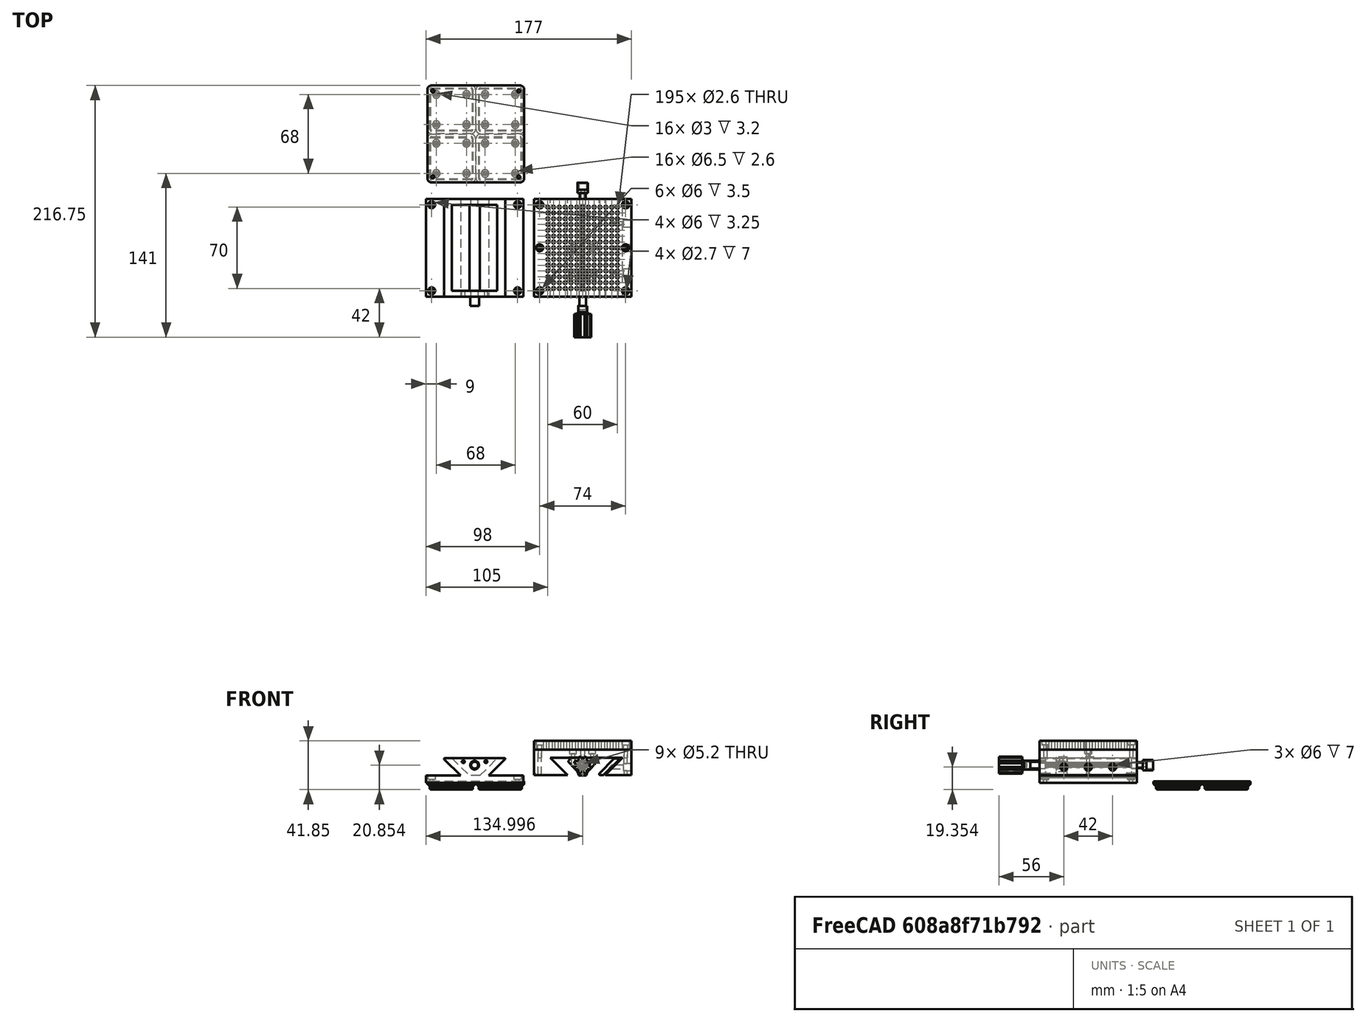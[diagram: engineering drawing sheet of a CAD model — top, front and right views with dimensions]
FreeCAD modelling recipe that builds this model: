
FCSTD DOCUMENT  (FreeCAD 1.0R39109 (Git))
Label: Linear Stage  v5
License: All rights reserved
LicenseURL: https://en.wikipedia.org/wiki/All_rights_reserved
objects: Sketcher::SketchObject×59, PartDesign::Pocket×30, PartDesign::Pad×26, PartDesign::Chamfer×17, PartDesign::Plane×11, PartDesign::ShapeBinder×10, PartDesign::Body×10, PartDesign::Fillet×6, PartDesign::Hole×3, PartDesign::FeatureBase×2, PartDesign::Point×1, Part::Part2DObjectPython×1, Part::Helix×1, PartDesign::AdditivePipe×1, PartDesign::FeaturePython×1, App::VarSet×1
note: 407 computed .brp shape members not serialized (recipe doc carries the construction recipe); baked Part::Feature solids carry a one-line shape summary decoded from their .brp

FEATURE [Sketcher::SketchObject] Sketch
  ArcFitTolerance = 1e-06
  AttachmentSupport = -> [XZ_Plane]
  FullyConstrained = true
  MakeInternals = false
  MapMode = 5
  Placement = pos=(0,0,0) rot=(1,0,0;1.5708rad)
  sketch-geometry (8):
    g0: LineSegment StartX=0 StartY=0 StartZ=0 EndX=84 EndY=0 EndZ=0
    g1: LineSegment StartX=0 StartY=0 StartZ=0 EndX=0 EndY=5 EndZ=0
    g2: LineSegment StartX=84 StartY=0 StartZ=0 EndX=84 EndY=5 EndZ=0
    g3: LineSegment StartX=0 StartY=5 StartZ=0 EndX=30 EndY=5 EndZ=0
    g4: LineSegment StartX=84 StartY=5 StartZ=0 EndX=54 EndY=5 EndZ=0
    g5: LineSegment StartX=30 StartY=5 StartZ=0 EndX=15 EndY=20 EndZ=0
    g6: LineSegment StartX=54 StartY=5 StartZ=0 EndX=69 EndY=20 EndZ=0
    g7: LineSegment StartX=15 StartY=20 StartZ=0 EndX=69 EndY=20 EndZ=0
  constraints (24):
    c: Distance(g0) = 84
    c: Distance(g1) = 5
    c: Coincident(g1,g0)
    c: PointOnObject(g1,g-2)
    c: Vertical(g1)
    c: Distance(g2) = 5
    c: Vertical(g2)
    c: Tangent(g0,g-1)
    c: PointOnObject(g2,g0)
    c: PointOnObject(g0,g2)
    c: Coincident(g3,g1)
    c: Horizontal(g3)
    c: Coincident(g4,g2)
    c: Horizontal(g4)
    c: DistanceX(g3,g3) = 30
    c: DistanceX(g4,g4) = 30
    c: Angle(g-1,g5) = 2.35619
    c: Coincident(g5,g3)
    c: Angle(g-1,g6) = 0.785398
    c: Coincident(g6,g4)
    c: DistanceY(g-1,g5) = 20
    c: DistanceY(g-1,g6) = 20
    c: Coincident(g7,g5)
    c: Coincident(g7,g6)
FEATURE [PartDesign::Pad] Pad
  Direction = (0,-1,2e-16)
  Length = 5
  Length2 = 10
  Placement = pos=(0,0,0) rot=(1,0,0;1.5708rad)
  Profile = -> Sketch
  ReferenceAxis = -> Sketch [N_Axis]
  Refine = true
  Suppressed = false
  Type = 0
FEATURE [Sketcher::SketchObject] Sketch001
  ArcFitTolerance = 1e-06
  AttachmentSupport = -> [Pad]
  ExternalGeometry = -> [Pad]
  FullyConstrained = true
  MakeInternals = false
  MapMode = 5
  Placement = pos=(0,-5,0) rot=(1,0,0;1.5708rad)
  sketch-geometry (14):
    g0: LineSegment StartX=15 StartY=20 StartZ=0 EndX=22.5 EndY=20 EndZ=0
    g1: LineSegment [constr] StartX=30 StartY=5 StartZ=0 EndX=37.5 EndY=5 EndZ=0
    g2: LineSegment StartX=22.5 StartY=20 StartZ=0 EndX=37.5 EndY=5 EndZ=0
    g3: LineSegment StartX=69 StartY=20 StartZ=0 EndX=61.5 EndY=20 EndZ=0
    g4: LineSegment [constr] StartX=54 StartY=5 StartZ=0 EndX=46.5 EndY=5 EndZ=0
    g5: LineSegment StartX=46.5 StartY=5 StartZ=0 EndX=61.5 EndY=20 EndZ=0
    g6: LineSegment StartX=46.5 StartY=5 StartZ=0 EndX=37.5 EndY=5 EndZ=0
    g7: LineSegment StartX=15 StartY=20 StartZ=0 EndX=30 EndY=5 EndZ=0
    g8: LineSegment StartX=30 StartY=5 StartZ=0 EndX=0 EndY=5 EndZ=0
    g9: LineSegment StartX=0 StartY=5 StartZ=0 EndX=0 EndY=0 EndZ=0
    g10: LineSegment StartX=0 StartY=0 StartZ=0 EndX=84 EndY=0 EndZ=0
    g11: LineSegment StartX=84 StartY=0 StartZ=0 EndX=84 EndY=5 EndZ=0
    g12: LineSegment StartX=84 StartY=5 StartZ=0 EndX=54 EndY=5 EndZ=0
    g13: LineSegment StartX=54 StartY=5 StartZ=0 EndX=69 EndY=20 EndZ=0
  constraints (32):
    c: Distance(g0) = 7.5
    c: Coincident(g0,g-4)
    c: PointOnObject(g0,g-3)
    c: Distance(g1) = 7.5
    c: Coincident(g1,g-5)
    c: Horizontal(g1)
    c: Coincident(g2,g0)
    c: Coincident(g2,g1)
    c: Distance(g3) = 7.5
    c: Coincident(g3,g-3)
    c: PointOnObject(g3,g-3)
    c: Distance(g4) = 7.5
    c: Coincident(g4,g-6)
    c: Horizontal(g4)
    c: Coincident(g5,g4)
    c: Coincident(g5,g3)
    c: Coincident(g6,g4)
    c: Coincident(g6,g1)
    c: Coincident(g7,g0)
    c: Coincident(g7,g1)
    c: Coincident(g8,g1)
    c: Coincident(g8,g-8)
    c: Coincident(g9,g8)
    c: Coincident(g9,g-1)
    c: Coincident(g10,g9)
    c: Coincident(g10,g-9)
    c: Coincident(g11,g10)
    c: Coincident(g11,g-7)
    c: Coincident(g12,g11)
    c: Coincident(g12,g4)
    c: Coincident(g13,g4)
    c: Coincident(g13,g3)
FEATURE [PartDesign::Pad] Pad001
  BaseFeature = -> Pad
  Direction = (0,-1,2e-16)
  Length = 74
  Length2 = 10
  Placement = pos=(0,0,0) rot=(1,0,0;1.5708rad)
  Profile = -> Sketch001
  ReferenceAxis = -> Sketch001 [N_Axis]
  Refine = true
  Suppressed = false
  Type = 0
FEATURE [Sketcher::SketchObject] Sketch002
  ArcFitTolerance = 1e-06
  AttachmentSupport = -> [Pad001]
  ExternalGeometry = -> [Pad001]
  FullyConstrained = true
  MakeInternals = false
  MapMode = 5
  Placement = pos=(0,-5,0) rot=(1,0,0;1.5708rad)
  sketch-geometry (2):
    g0: LineSegment [constr] StartX=42 StartY=20 StartZ=0 EndX=42 EndY=14 EndZ=0
    g1: Circle CenterX=42 CenterY=14 CenterZ=0 NormalX=0 NormalY=0 NormalZ=1 AngleXU=0 Radius=3
  constraints (5):
    c: Distance(g0) = 6
    c: Symmetric(g-3,g-3,g0)
    c: Vertical(g0)
    c: Diameter(g1) = 6
    c: Coincident(g1,g0)
FEATURE [PartDesign::Hole] Hole
  BaseFeature = -> Pad001
  CustomThreadClearance = 0
  Depth = 25
  DepthType = 0
  Diameter = 6
  DrillForDepth = false
  DrillPoint = 1
  DrillPointAngle = 118
  HoleCutCountersinkAngle = 90
  HoleCutCustomValues = false
  HoleCutDepth = 0
  HoleCutDiameter = 6.1
  HoleCutType = 0
  ModelThread = false
  Placement = pos=(0,0,0) rot=(1,0,0;1.5708rad)
  Profile = -> Sketch002
  Refine = true
  Suppressed = false
  Tapered = false
  TaperedAngle = 90
  ThreadClass = 0
  ThreadDepth = 25
  ThreadDepthType = 0
  ThreadDirection = 0
  ThreadFit = 0
  ThreadSize = 0
  ThreadType = 0
  Threaded = false
  UseCustomThreadClearance = false
FEATURE [Sketcher::SketchObject] Sketch003
  ArcFitTolerance = 1e-06
  AttachmentSupport = -> [Hole]
  ExternalGeometry = -> [Hole]
  FullyConstrained = true
  MakeInternals = false
  MapMode = 5
  Placement = pos=(0,-79,1.74e-14) rot=(1,0,0;1.5708rad)
  sketch-geometry (16):
    g0: LineSegment StartX=15 StartY=20 StartZ=0 EndX=69 EndY=20 EndZ=0
    g1: LineSegment StartX=15 StartY=20 StartZ=0 EndX=30 EndY=5 EndZ=0
    g2: LineSegment StartX=30 StartY=5 StartZ=0 EndX=0 EndY=5 EndZ=0
    g3: LineSegment StartX=0 StartY=5 StartZ=0 EndX=0 EndY=0 EndZ=0
    g4: LineSegment StartX=0 StartY=0 StartZ=0 EndX=84 EndY=0 EndZ=0
    g5: LineSegment StartX=84 StartY=0 StartZ=0 EndX=84 EndY=5 EndZ=0
    g6: LineSegment StartX=84 StartY=5 StartZ=0 EndX=54 EndY=5 EndZ=0
    g7: LineSegment StartX=54 StartY=5 StartZ=0 EndX=69 EndY=20 EndZ=0
    g8: LineSegment [constr] StartX=42 StartY=20 StartZ=0 EndX=42 EndY=14 EndZ=0
    g9: Circle CenterX=42 CenterY=14 CenterZ=0 NormalX=0 NormalY=0 NormalZ=1 AngleXU=0 Radius=3
    g10: LineSegment [constr] StartX=42 StartY=14 StartZ=0 EndX=22.5 EndY=20 EndZ=0
    g11: LineSegment [constr] StartX=42 StartY=14 StartZ=0 EndX=61.5 EndY=20 EndZ=0
    g12: GeomPoint [constr] X=32.25 Y=17 Z=0
    g13: GeomPoint [constr] X=51.75 Y=17 Z=0
    g14: Circle CenterX=32.25 CenterY=17 CenterZ=0 NormalX=0 NormalY=0 NormalZ=1 AngleXU=0 Radius=1.25
    g15: Circle CenterX=51.75 CenterY=17 CenterZ=0 NormalX=0 NormalY=0 NormalZ=1 AngleXU=0 Radius=1.25
  constraints (31):
    c: Coincident(g0,g-4)
    c: Coincident(g0,g-11)
    c: Coincident(g1,g0)
    c: Coincident(g1,g-5)
    c: Coincident(g2,g1)
    c: Coincident(g2,g-6)
    c: Coincident(g3,g2)
    c: Coincident(g3,g-1)
    c: Coincident(g4,g3)
    c: Coincident(g4,g-8)
    c: Coincident(g5,g4)
    c: Coincident(g5,g-9)
    c: Coincident(g6,g5)
    c: Coincident(g6,g-10)
    c: Coincident(g7,g6)
    c: Coincident(g7,g0)
    c: Distance(g8) = 6
    c: Symmetric(g0,g0,g8)
    c: Vertical(g8)
    c: Diameter(g9) = 6
    c: Coincident(g9,g8)
    c: Coincident(g10,g8)
    c: Coincident(g10,g-14)
    c: Coincident(g11,g8)
    c: Coincident(g11,g-12)
    c: Symmetric(g10,g10,g12)
    c: Symmetric(g11,g11,g13)
    c: Diameter(g14) = 2.5
    c: Coincident(g14,g12)
    c: Diameter(g15) = 2.5
    c: Coincident(g15,g13)
FEATURE [PartDesign::Pad] Pad002
  BaseFeature = -> Hole
  Direction = (0,-1,2e-16)
  Length = 5
  Length2 = 10
  Placement = pos=(0,0,0) rot=(1,0,0;1.5708rad)
  Profile = -> Sketch003
  ReferenceAxis = -> Sketch003 [N_Axis]
  Refine = true
  Suppressed = false
  Type = 0
FEATURE [PartDesign::Plane] DatumPlane
  AttachmentSupport = -> [Pad002]
  Length = 131.586
  MapMode = 5
  Placement = pos=(0,0,-5e-16) rot=(1,0,0;3.14159rad)
  ResizeMode = 0
  Width = 139.586
FEATURE [Sketcher::SketchObject] Sketch004
  ArcFitTolerance = 1e-06
  AttachmentSupport = -> [Pad002]
  ExternalGeometry = -> [Pad002]
  FullyConstrained = true
  MakeInternals = false
  MapMode = 5
  Placement = pos=(0,0,-5e-16) rot=(1,0,0;3.14159rad)
  sketch-geometry (23):
    g0: LineSegment [constr] StartX=0 StartY=84 StartZ=0 EndX=84 EndY=0 EndZ=0
    g1: LineSegment [constr] StartX=41.75 StartY=41.75 StartZ=0 EndX=42.25 EndY=41.75 EndZ=0
    g2: LineSegment [constr] StartX=42.25 StartY=41.75 StartZ=0 EndX=42.25 EndY=42.25 EndZ=0
    g3: LineSegment [constr] StartX=42.25 StartY=42.25 StartZ=0 EndX=41.75 EndY=42.25 EndZ=0
    g4: LineSegment [constr] StartX=41.75 StartY=42.25 StartZ=0 EndX=41.75 EndY=41.75 EndZ=0
    g5: GeomPoint [constr] X=42 Y=42 Z=0
    g6: LineSegment [constr] StartX=0 StartY=0 StartZ=0 EndX=84 EndY=84 EndZ=0
    g7: LineSegment StartX=42.25 StartY=42.25 StartZ=0 EndX=83.75 EndY=42.25 EndZ=0
    g8: LineSegment StartX=83.75 StartY=42.25 StartZ=0 EndX=83.75 EndY=83.75 EndZ=0
    g9: LineSegment StartX=83.75 StartY=83.75 StartZ=0 EndX=42.25 EndY=83.75 EndZ=0
    g10: LineSegment StartX=42.25 StartY=83.75 StartZ=0 EndX=42.25 EndY=42.25 EndZ=0
    g11: LineSegment StartX=41.75 StartY=42.25 StartZ=0 EndX=41.75 EndY=83.75 EndZ=0
    g12: LineSegment StartX=41.75 StartY=83.75 StartZ=0 EndX=0.25 EndY=83.75 EndZ=0
    g13: LineSegment StartX=0.25 StartY=83.75 StartZ=0 EndX=0.25 EndY=42.25 EndZ=0
    g14: LineSegment StartX=0.25 StartY=42.25 StartZ=0 EndX=41.75 EndY=42.25 EndZ=0
    g15: LineSegment StartX=42.25 StartY=41.75 StartZ=0 EndX=42.25 EndY=0.25 EndZ=0
    g16: LineSegment StartX=42.25 StartY=0.25 StartZ=0 EndX=83.75 EndY=0.25 EndZ=0
    g17: LineSegment StartX=83.75 StartY=0.25 StartZ=0 EndX=83.75 EndY=41.75 EndZ=0
    g18: LineSegment StartX=83.75 StartY=41.75 StartZ=0 EndX=42.25 EndY=41.75 EndZ=0
    g19: LineSegment StartX=41.75 StartY=41.75 StartZ=0 EndX=0.25 EndY=41.75 EndZ=0
    g20: LineSegment StartX=0.25 StartY=41.75 StartZ=0 EndX=0.25 EndY=0.25 EndZ=0
    g21: LineSegment StartX=0.25 StartY=0.25 StartZ=0 EndX=41.75 EndY=0.25 EndZ=0
    g22: LineSegment StartX=41.75 StartY=0.25 StartZ=0 EndX=41.75 EndY=41.75 EndZ=0
  constraints (61):
    c: Coincident(g0,g-6)
    c: Coincident(g0,g-5)
    c: Coincident(g1,g2)
    c: Coincident(g2,g3)
    c: Coincident(g3,g4)
    c: Coincident(g4,g1)
    c: Horizontal(g1)
    c: Horizontal(g3)
    c: Vertical(g2)
    c: Vertical(g4)
    c: Symmetric(g3,g1,g5)
    c: Distance(g2,g4) = 0.5
    c: Distance(g1,g3) = 0.5
    c: PointOnObject(g5,g0)
    c: Coincident(g6,g-1)
    c: Coincident(g6,g-4)
    c: PointOnObject(g5,g6)
    c: Coincident(g7,g8)
    c: Coincident(g8,g9)
    c: Coincident(g9,g10)
    c: Coincident(g10,g7)
    c: Horizontal(g7)
    c: Horizontal(g9)
    c: Vertical(g8)
    c: Vertical(g10)
    c: Distance(g8,g10) = 41.5
    c: Coincident(g7,g2)
    c: PointOnObject(g8,g6)
    c: Coincident(g11,g12)
    c: Coincident(g12,g13)
    c: Coincident(g13,g14)
    c: Coincident(g14,g11)
    c: Vertical(g11)
    c: Vertical(g13)
    c: Horizontal(g12)
    c: Horizontal(g14)
    c: Distance(g11,g13) = 41.5
    c: Coincident(g11,g3)
    c: PointOnObject(g12,g0)
    c: Coincident(g15,g16)
    c: Coincident(g16,g17)
    c: Coincident(g17,g18)
    c: Coincident(g18,g15)
    c: Vertical(g15)
    c: Vertical(g17)
    c: Horizontal(g16)
    c: Horizontal(g18)
    c: Distance(g15,g17) = 41.5
    c: Coincident(g15,g1)
    c: PointOnObject(g16,g0)
    c: Coincident(g19,g20)
    c: Coincident(g20,g21)
    c: Coincident(g21,g22)
    c: Coincident(g22,g19)
    c: Horizontal(g19)
    c: Horizontal(g21)
    c: Vertical(g20)
    c: Vertical(g22)
    c: Distance(g20,g22) = 41.5
    c: Coincident(g19,g1)
    c: PointOnObject(g20,g6)
FEATURE [PartDesign::Pad] Pad003
  BaseFeature = -> Pad002
  Direction = (0,0,-1)
  Length = 1
  Length2 = 10
  Placement = pos=(0,0,0) rot=(1,0,0;1.5708rad)
  Profile = -> Sketch004
  ReferenceAxis = -> Sketch004 [N_Axis]
  Refine = true
  Suppressed = false
  Type = 0
FEATURE [PartDesign::Plane] DatumPlane001
  AttachmentSupport = -> [Pad003]
  Length = 131.586
  MapMode = 5
  Placement = pos=(0,0,-1) rot=(1,0,0;3.14159rad)
  ResizeMode = 0
  Width = 139.586
FEATURE [Sketcher::SketchObject] Sketch005
  ArcFitTolerance = 1e-06
  AttachmentSupport = -> [DatumPlane001]
  ExternalGeometry = -> [Pad003]
  FullyConstrained = true
  MakeInternals = false
  MapMode = 5
  Placement = pos=(0,0,-1) rot=(1,0,0;3.14159rad)
  sketch-geometry (28):
    g0: LineSegment [constr] StartX=41.75 StartY=42.25 StartZ=0 EndX=0.25 EndY=83.75 EndZ=0
    g1: GeomPoint [constr] X=21 Y=63 Z=0
    g2: LineSegment StartX=2.4 StartY=44.4 StartZ=0 EndX=39.6 EndY=44.4 EndZ=0
    g3: LineSegment StartX=39.6 StartY=44.4 StartZ=0 EndX=39.6 EndY=81.6 EndZ=0
    g4: LineSegment StartX=39.6 StartY=81.6 StartZ=0 EndX=2.4 EndY=81.6 EndZ=0
    g5: LineSegment StartX=2.4 StartY=81.6 StartZ=0 EndX=2.4 EndY=44.4 EndZ=0
    g6: GeomPoint [constr] X=21 Y=63 Z=0
    g7: LineSegment [constr] StartX=42.25 StartY=83.75 StartZ=0 EndX=83.75 EndY=42.25 EndZ=0
    g8: LineSegment [constr] StartX=83.75 StartY=41.75 StartZ=0 EndX=42.25 EndY=0.25 EndZ=0
    g9: LineSegment [constr] StartX=41.75 StartY=0.25 StartZ=0 EndX=0.25 EndY=41.75 EndZ=0
    g10: GeomPoint [constr] X=63 Y=63 Z=0
    g11: GeomPoint [constr] X=63 Y=21 Z=0
    g12: GeomPoint [constr] X=21 Y=21 Z=0
    g13: LineSegment StartX=44.4 StartY=44.4 StartZ=0 EndX=81.6 EndY=44.4 EndZ=0
    g14: LineSegment StartX=81.6 StartY=44.4 StartZ=0 EndX=81.6 EndY=81.6 EndZ=0
    g15: LineSegment StartX=81.6 StartY=81.6 StartZ=0 EndX=44.4 EndY=81.6 EndZ=0
    g16: LineSegment StartX=44.4 StartY=81.6 StartZ=0 EndX=44.4 EndY=44.4 EndZ=0
    g17: GeomPoint [constr] X=63 Y=63 Z=0
    g18: LineSegment StartX=44.4 StartY=2.4 StartZ=0 EndX=81.6 EndY=2.4 EndZ=0
    g19: LineSegment StartX=81.6 StartY=2.4 StartZ=0 EndX=81.6 EndY=39.6 EndZ=0
    g20: LineSegment StartX=81.6 StartY=39.6 StartZ=0 EndX=44.4 EndY=39.6 EndZ=0
    g21: LineSegment StartX=44.4 StartY=39.6 StartZ=0 EndX=44.4 EndY=2.4 EndZ=0
    g22: GeomPoint [constr] X=63 Y=21 Z=0
    g23: LineSegment StartX=2.4 StartY=2.4 StartZ=0 EndX=39.6 EndY=2.4 EndZ=0
    g24: LineSegment StartX=39.6 StartY=2.4 StartZ=0 EndX=39.6 EndY=39.6 EndZ=0
    g25: LineSegment StartX=39.6 StartY=39.6 StartZ=0 EndX=2.4 EndY=39.6 EndZ=0
    g26: LineSegment StartX=2.4 StartY=39.6 StartZ=0 EndX=2.4 EndY=2.4 EndZ=0
    g27: GeomPoint [constr] X=21 Y=21 Z=0
  constraints (60):
    c: Coincident(g0,g-14)
    c: Coincident(g0,g-16)
    c: Symmetric(g0,g0,g1)
    c: Coincident(g2,g3)
    c: Coincident(g3,g4)
    c: Coincident(g4,g5)
    c: Coincident(g5,g2)
    c: Horizontal(g2)
    c: Horizontal(g4)
    c: Vertical(g3)
    c: Vertical(g5)
    c: Symmetric(g4,g2,g6)
    c: Distance(g3,g5) = 37.2
    c: Distance(g2,g4) = 37.2
    c: Coincident(g6,g1)
    c: Coincident(g7,g-18)
    c: Coincident(g7,g-17)
    c: Coincident(g8,g-9)
    c: Coincident(g8,g-10)
    c: Coincident(g9,g-4)
    c: Coincident(g9,g-6)
    c: Symmetric(g7,g7,g10)
    c: Symmetric(g8,g8,g11)
    c: Symmetric(g9,g9,g12)
    c: Coincident(g13,g14)
    c: Coincident(g14,g15)
    c: Coincident(g15,g16)
    c: Coincident(g16,g13)
    c: Horizontal(g13)
    c: Horizontal(g15)
    c: Vertical(g14)
    c: Vertical(g16)
    c: Symmetric(g15,g13,g17)
    c: Distance(g14,g16) = 37.2
    c: Distance(g13,g15) = 37.2
    c: Coincident(g17,g10)
    c: Coincident(g18,g19)
    c: Coincident(g19,g20)
    c: Coincident(g20,g21)
    c: Coincident(g21,g18)
    c: Horizontal(g18)
    c: Horizontal(g20)
    c: Vertical(g19)
    c: Vertical(g21)
    c: Symmetric(g20,g18,g22)
    c: Distance(g19,g21) = 37.2
    c: Coincident(g22,g11)
    c: PointOnObject(g19,g8)
    c: Coincident(g23,g24)
    c: Coincident(g24,g25)
    c: Coincident(g25,g26)
    c: Coincident(g26,g23)
    c: Horizontal(g23)
    c: Horizontal(g25)
    c: Vertical(g24)
    c: Vertical(g26)
    c: Symmetric(g25,g23,g27)
    c: Distance(g24,g26) = 37.2
    c: Distance(g23,g25) = 37.2
    c: Coincident(g27,g12)
FEATURE [PartDesign::Pad] Pad004
  BaseFeature = -> Pad003
  Direction = (0,0,-1)
  Length = 3.5
  Length2 = 10
  Placement = pos=(0,0,0) rot=(1,0,0;1.5708rad)
  Profile = -> Sketch005
  ReferenceAxis = -> Sketch005 [N_Axis]
  Refine = true
  Suppressed = false
  Type = 0
FEATURE [PartDesign::Chamfer] Chamfer
  Angle = 45
  Base = -> Pad004 [Edge114]
  BaseFeature = -> Pad004
  ChamferType = 0
  FlipDirection = false
  Placement = pos=(0,0,0) rot=(1,0,0;1.5708rad)
  Refine = true
  Size = 7
  Size2 = 1
  SupportTransform = false
  Suppressed = false
  UseAllEdges = false
FEATURE [PartDesign::Chamfer] Chamfer001
  Angle = 45
  Base = -> Chamfer [Edge23]
  BaseFeature = -> Chamfer
  ChamferType = 0
  FlipDirection = false
  Placement = pos=(0,0,0) rot=(1,0,0;1.5708rad)
  Refine = true
  Size = 7
  Size2 = 1
  SupportTransform = false
  Suppressed = false
  UseAllEdges = false
FEATURE [PartDesign::Chamfer] Chamfer002
  Angle = 45
  Base = -> Chamfer001 [Edge136,Edge28,Edge143,Edge22,Edge135,Edge128,Edge144,Edge148,Edge140,Edge127,Edge132,Edge138,Edge26,Edge130]
  BaseFeature = -> Chamfer001
  ChamferType = 0
  FlipDirection = false
  Placement = pos=(0,0,0) rot=(1,0,0;1.5708rad)
  Refine = true
  Size = 7
  Size2 = 1
  SupportTransform = false
  Suppressed = false
  UseAllEdges = false
FEATURE [PartDesign::Chamfer] Chamfer003
  Angle = 45
  Base = -> Chamfer002 [Edge77,Edge79,Edge93,Edge81,Edge95,Edge38,Edge76,Edge32,Edge92,Edge84,Edge97,Edge85,Edge87,Edge89,Edge35]
  BaseFeature = -> Chamfer002
  ChamferType = 0
  FlipDirection = false
  Placement = pos=(0,0,0) rot=(1,0,0;1.5708rad)
  Refine = true
  Size = 8
  Size2 = 1
  SupportTransform = false
  Suppressed = false
  UseAllEdges = false
FEATURE [PartDesign::Chamfer] Chamfer004
  Angle = 45
  Base = -> Chamfer003 [Edge231]
  BaseFeature = -> Chamfer003
  ChamferType = 0
  FlipDirection = false
  Placement = pos=(0,0,0) rot=(1,0,0;1.5708rad)
  Refine = true
  Size = 7
  Size2 = 1
  SupportTransform = false
  Suppressed = false
  UseAllEdges = false
FEATURE [PartDesign::Chamfer] Chamfer005
  Angle = 45
  Base = -> Chamfer004 [Edge1,Edge2,Edge4,Edge6,Edge8,Edge7,Edge5,Edge3]
  BaseFeature = -> Chamfer004
  ChamferType = 0
  FlipDirection = false
  Placement = pos=(0,0,0) rot=(1,0,0;1.5708rad)
  Refine = true
  Size = 2
  Size2 = 1
  SupportTransform = false
  Suppressed = false
  UseAllEdges = false
FEATURE [PartDesign::Chamfer] Chamfer006
  Angle = 45
  Base = -> Chamfer005 [Edge60,Edge64,Edge62,Edge58,Edge55,Edge50,Edge52,Edge56]
  BaseFeature = -> Chamfer005
  ChamferType = 0
  FlipDirection = false
  Placement = pos=(0,0,0) rot=(1,0,0;1.5708rad)
  Refine = true
  Size = 0.8
  Size2 = 1
  SupportTransform = false
  Suppressed = false
  UseAllEdges = false
FEATURE [PartDesign::Chamfer] Chamfer007
  Angle = 45
  Base = -> Chamfer006 [Edge207,Edge208,Edge205,Edge206,Edge204,Edge202,Edge203,Edge201]
  BaseFeature = -> Chamfer006
  ChamferType = 0
  FlipDirection = false
  Placement = pos=(0,0,0) rot=(1,0,0;1.5708rad)
  Refine = true
  Size = 2
  Size2 = 1
  SupportTransform = false
  Suppressed = false
  UseAllEdges = false
FEATURE [PartDesign::Chamfer] Chamfer008
  Angle = 45
  Base = -> Chamfer007 [Edge63,Edge64,Edge60,Edge57,Edge52,Edge50,Edge55,Edge59]
  BaseFeature = -> Chamfer007
  ChamferType = 0
  FlipDirection = false
  Placement = pos=(0,0,0) rot=(1,0,0;1.5708rad)
  Refine = true
  Size = 0.8
  Size2 = 1
  SupportTransform = false
  Suppressed = false
  UseAllEdges = false
FEATURE [PartDesign::Chamfer] Chamfer009
  Angle = 45
  Base = -> Chamfer008 [Edge179,Edge177,Edge178,Edge181,Edge180,Edge182,Edge184,Edge183]
  BaseFeature = -> Chamfer008
  ChamferType = 0
  FlipDirection = false
  Placement = pos=(0,0,0) rot=(1,0,0;1.5708rad)
  Refine = true
  Size = 2
  Size2 = 1
  SupportTransform = false
  Suppressed = false
  UseAllEdges = false
FEATURE [PartDesign::Chamfer] Chamfer010
  Angle = 45
  Base = -> Chamfer009 [Edge55,Edge58,Edge62,Edge64,Edge61,Edge56,Edge53,Edge50]
  BaseFeature = -> Chamfer009
  ChamferType = 0
  FlipDirection = false
  Placement = pos=(0,0,0) rot=(1,0,0;1.5708rad)
  Refine = true
  Size = 0.8
  Size2 = 1
  SupportTransform = false
  Suppressed = false
  UseAllEdges = false
FEATURE [PartDesign::Chamfer] Chamfer011
  Angle = 45
  Base = -> Chamfer010 [Edge203,Edge205,Edge201,Edge202,Edge204,Edge206,Edge208,Edge207]
  BaseFeature = -> Chamfer010
  ChamferType = 0
  FlipDirection = false
  Placement = pos=(0,0,0) rot=(1,0,0;1.5708rad)
  Refine = true
  Size = 2
  Size2 = 1
  SupportTransform = false
  Suppressed = false
  UseAllEdges = false
FEATURE [PartDesign::Chamfer] Chamfer012
  Angle = 45
  Base = -> Chamfer011 [Edge62,Edge59,Edge54,Edge50,Edge53,Edge56,Edge61,Edge64]
  BaseFeature = -> Chamfer011
  ChamferType = 0
  FlipDirection = false
  Placement = pos=(0,0,0) rot=(1,0,0;1.5708rad)
  Refine = true
  Size = 0.8
  Size2 = 1
  SupportTransform = false
  Suppressed = false
  UseAllEdges = false
FEATURE [PartDesign::Fillet] Fillet
  Base = -> Chamfer012 [Edge188,Edge187]
  BaseFeature = -> Chamfer012
  Placement = pos=(0,0,0) rot=(1,0,0;1.5708rad)
  Radius = 0.5
  Refine = true
  SupportTransform = false
  Suppressed = false
  UseAllEdges = false
FEATURE [PartDesign::ShapeBinder] ShapeBinder
  Support = -> [Fillet]
  TraceSupport = false
FEATURE [PartDesign::ShapeBinder] CopyFillet
  Placement = pos=(0,-5,2e-15) rot=(0,0,1;0rad)
  TraceSupport = false
FEATURE [PartDesign::Plane] DatumPlane002
  AttachmentSupport = -> [CopyFillet]
  Length = 111.71
  MapMode = 5
  Placement = pos=(0,-84,2e-15) rot=(1,0,0;1.5708rad)
  ResizeMode = 0
  Width = 63.9806
FEATURE [Sketcher::SketchObject] Sketch006
  ArcFitTolerance = 1e-06
  AttachmentSupport = -> [DatumPlane002]
  ExternalGeometry = -> [ShapeBinder]
  FullyConstrained = true
  MakeInternals = false
  MapMode = 5
  Placement = pos=(0,-84,2e-15) rot=(1,0,0;1.5708rad)
  sketch-geometry (16):
    g0: LineSegment [constr] StartX=68.1465 StartY=19.1464 StartZ=0 EndX=69 EndY=20 EndZ=0
    g1: LineSegment [constr] StartX=67.7929 StartY=20 StartZ=0 EndX=69 EndY=20 EndZ=0
    g2: LineSegment [constr] StartX=69 StartY=20 StartZ=0 EndX=69.5 EndY=20 EndZ=0
    g3: LineSegment [constr] StartX=69.5 StartY=20 StartZ=0 EndX=74.5 EndY=20 EndZ=0
    g4: LineSegment [constr] StartX=54 StartY=5 StartZ=0 EndX=54.5 EndY=5 EndZ=0
    g5: LineSegment [constr] StartX=54.5 StartY=5 StartZ=0 EndX=59.5 EndY=5 EndZ=0
    g6: LineSegment [constr] StartX=59.5 StartY=5 StartZ=0 EndX=74.5 EndY=20 EndZ=0
    g7: LineSegment [constr] StartX=54.5 StartY=5 StartZ=0 EndX=69.5 EndY=20 EndZ=0
    g8: LineSegment [constr] StartX=59.5 StartY=5 StartZ=0 EndX=59.8536 EndY=5.35355 EndZ=0
    g9: LineSegment [constr] StartX=54.5 StartY=5 StartZ=0 EndX=54.8536 EndY=5.35355 EndZ=0
    g10: LineSegment [constr] StartX=74.5 StartY=20 StartZ=0 EndX=74.1465 EndY=19.6464 EndZ=0
    g11: LineSegment [constr] StartX=69.5 StartY=20 StartZ=0 EndX=69.1465 EndY=19.6464 EndZ=0
    g12: LineSegment StartX=54.8536 StartY=5.35355 StartZ=0 EndX=59.8536 EndY=5.35355 EndZ=0
    g13: LineSegment StartX=59.8536 StartY=5.35355 StartZ=0 EndX=74.1465 EndY=19.6464 EndZ=0
    g14: LineSegment StartX=74.1465 StartY=19.6464 StartZ=0 EndX=69.1465 EndY=19.6464 EndZ=0
    g15: LineSegment StartX=69.1465 StartY=19.6464 StartZ=0 EndX=54.8536 EndY=5.35355 EndZ=0
  constraints (41):
    c: Coincident(g0,g-3)
    c: Coincident(g1,g-4)
    c: Coincident(g1,g0)
    c: Angle(g-4,g1) = 3.14159
    c: Angle(g-3,g0) = 3.14159
    c: Distance(g2) = 0.5
    c: Coincident(g2,g0)
    c: Horizontal(g2)
    c: Distance(g3) = 5
    c: Coincident(g3,g2)
    c: Horizontal(g3)
    c: Distance(g4) = 0.5
    c: Coincident(g4,g-3)
    c: Horizontal(g4)
    c: Distance(g5) = 5
    c: Coincident(g5,g4)
    c: Horizontal(g5)
    c: Coincident(g6,g5)
    c: Coincident(g6,g3)
    c: Coincident(g7,g4)
    c: Coincident(g7,g2)
    c: Distance(g8) = 0.5
    c: Coincident(g8,g5)
    c: PointOnObject(g8,g6)
    c: Distance(g9) = 0.5
    c: Coincident(g9,g4)
    c: PointOnObject(g9,g7)
    c: Distance(g10) = 0.5
    c: Coincident(g10,g3)
    c: PointOnObject(g10,g6)
    c: Distance(g11) = 0.5
    c: Coincident(g11,g2)
    c: PointOnObject(g11,g7)
    c: Coincident(g12,g9)
    c: Coincident(g12,g8)
    c: Coincident(g13,g8)
    c: Coincident(g13,g10)
    c: Coincident(g14,g10)
    c: Coincident(g14,g11)
    c: Coincident(g15,g11)
    c: Coincident(g15,g9)
FEATURE [PartDesign::Pad] Pad005
  Direction = (0,-1,2e-16)
  Length = 84
  Length2 = 10
  Placement = pos=(0,-84,2e-15) rot=(1,0,0;1.5708rad)
  Profile = -> Sketch006
  ReferenceAxis = -> Sketch006 [N_Axis]
  Refine = true
  Reversed = true
  Suppressed = false
  Type = 0
FEATURE [PartDesign::Plane] DatumPlane003
  AttachmentSupport = -> [Pad005]
  Length = 125.801
  MapMode = 5
  Placement = pos=(27.25,-84,-27.25) rot=(0.92388,0,0.382683;3.14159rad)
  ResizeMode = 0
  Width = 130.341
FEATURE [Sketcher::SketchObject] Sketch007
  ArcFitTolerance = 1e-06
  AttachmentSupport = -> [DatumPlane003]
  ExternalGeometry = -> [Pad005]
  FullyConstrained = true
  MakeInternals = false
  MapMode = 5
  Placement = pos=(27.25,-84,-27.25) rot=(0.92388,0,0.382683;3.14159rad)
  sketch-geometry (8):
    g0: LineSegment [constr] StartX=46.1084 StartY=-42 StartZ=0 EndX=66.3216 EndY=-42 EndZ=0
    g1: LineSegment [constr] StartX=56.215 StartY=-42 StartZ=0 EndX=56.215 EndY=-1.42e-14 EndZ=0
    g2: LineSegment [constr] StartX=56.215 StartY=-42 StartZ=0 EndX=56.215 EndY=-84 EndZ=0
    g3: GeomPoint [constr] X=56.215 Y=-63 Z=0
    g4: GeomPoint [constr] X=56.215 Y=-21 Z=0
    g5: Circle CenterX=56.215 CenterY=-21 CenterZ=0 NormalX=0 NormalY=0 NormalZ=1 AngleXU=0 Radius=1.55
    g6: Circle CenterX=56.215 CenterY=-42 CenterZ=0 NormalX=0 NormalY=0 NormalZ=1 AngleXU=0 Radius=1.55
    g7: Circle CenterX=56.215 CenterY=-63 CenterZ=0 NormalX=0 NormalY=0 NormalZ=1 AngleXU=0 Radius=1.55
  constraints (14):
    c: Symmetric(g-4,g-4,g0)
    c: Symmetric(g-3,g-3,g0)
    c: Symmetric(g0,g0,g1)
    c: Symmetric(g-5,g-5,g1)
    c: Coincident(g2,g1)
    c: Symmetric(g-6,g-6,g2)
    c: Symmetric(g2,g2,g3)
    c: Symmetric(g1,g1,g4)
    c: Diameter(g5) = 3.1
    c: Coincident(g5,g4)
    c: Diameter(g6) = 3.1
    c: Coincident(g6,g1)
    c: Diameter(g7) = 3.1
    c: Coincident(g7,g3)
FEATURE [PartDesign::Pocket] Pocket
  BaseFeature = -> Pad005
  Direction = (-0.707107,0,0.707107)
  Length = 1
  Length2 = 5
  Placement = pos=(0,-84,2e-15) rot=(1,0,0;1.5708rad)
  Profile = -> Sketch007
  ReferenceAxis = -> Sketch007 [N_Axis]
  Refine = true
  Suppressed = false
  Type = 0
FEATURE [PartDesign::Fillet] Fillet001
  Base = -> Pocket [Edge5,Edge10,Edge1,Edge2]
  BaseFeature = -> Pocket
  Placement = pos=(0,-84,2e-15) rot=(1,0,0;1.5708rad)
  Radius = 1
  Refine = true
  SupportTransform = false
  Suppressed = false
  UseAllEdges = false
FEATURE [PartDesign::Fillet] Fillet002
  Base = -> Fillet001 [Edge24,Edge25,Edge23]
  BaseFeature = -> Fillet001
  Placement = pos=(0,-84,2e-15) rot=(1,0,0;1.5708rad)
  Radius = 0.3
  Refine = true
  SupportTransform = false
  Suppressed = false
  UseAllEdges = false
FEATURE [PartDesign::Fillet] Fillet003
  Base = -> Fillet002 [Edge31,Edge37,Edge39]
  BaseFeature = -> Fillet002
  Placement = pos=(0,-84,2e-15) rot=(1,0,0;1.5708rad)
  Radius = 0.3
  Refine = true
  SupportTransform = false
  Suppressed = false
  UseAllEdges = false
FEATURE [PartDesign::Body] Body001  label="Shim"
  AllowCompound = false
  Group = -> [ShapeBinder,DatumPlane002,CopyFillet,Sketch006,Pad005,DatumPlane003,Sketch007,Pocket,Fillet001,Fillet002,Fillet003]
  Origin = -> Origin001
  Tip = -> Fillet003
FEATURE [PartDesign::ShapeBinder] ShapeBinder001
  Support = -> [Fillet]
  TraceSupport = false
FEATURE [PartDesign::ShapeBinder] CopyFillet001
  Placement = pos=(0,-5,2e-15) rot=(0,0,1;0rad)
  TraceSupport = false
FEATURE [PartDesign::Plane] DatumPlane004
  AttachmentSupport = -> [CopyFillet001]
  Length = 124.108
  MapMode = 5
  Placement = pos=(0,-84,2e-15) rot=(1,0,0;1.5708rad)
  ResizeMode = 0
  Width = 67.4619
FEATURE [Sketcher::SketchObject] Sketch008
  ArcFitTolerance = 1e-06
  AttachmentSupport = -> [DatumPlane004]
  ExternalGeometry = -> [ShapeBinder001]
  FullyConstrained = true
  MakeInternals = false
  MapMode = 5
  Placement = pos=(0,-84,2e-15) rot=(1,0,0;1.5708rad)
  sketch-geometry (21):
    g0: LineSegment [constr] StartX=54 StartY=5 StartZ=0 EndX=61 EndY=5 EndZ=0
    g1: LineSegment [constr] StartX=68.1465 StartY=19.1464 StartZ=0 EndX=69 EndY=20 EndZ=0
    g2: LineSegment [constr] StartX=67.7929 StartY=20 StartZ=0 EndX=69 EndY=20 EndZ=0
    g3: LineSegment [constr] StartX=69 StartY=20 StartZ=0 EndX=76 EndY=20 EndZ=0
    g4: LineSegment [constr] StartX=61 StartY=5 StartZ=0 EndX=61.3536 EndY=5.35355 EndZ=0
    g5: LineSegment [constr] StartX=76 StartY=20 StartZ=0 EndX=76.3536 EndY=20.3536 EndZ=0
    g6: LineSegment StartX=76.3536 StartY=20.3536 StartZ=0 EndX=61.3536 EndY=5.35355 EndZ=0
    g7: LineSegment [constr] StartX=84 StartY=5 StartZ=0 EndX=84 EndY=5.5 EndZ=0
    g8: LineSegment StartX=61.3536 StartY=5.35355 StartZ=0 EndX=84 EndY=5.35355 EndZ=0
    g9: LineSegment StartX=84 StartY=5.35355 StartZ=0 EndX=84 EndY=25.3536 EndZ=0
    g10: LineSegment [constr] StartX=30 StartY=5 StartZ=0 EndX=29.5 EndY=5 EndZ=0
    g11: LineSegment [constr] StartX=16.2071 StartY=20 StartZ=0 EndX=14.5 EndY=20 EndZ=0
    g12: LineSegment [constr] StartX=29.5 StartY=5 StartZ=0 EndX=14.5 EndY=20 EndZ=0
    g13: LineSegment [constr] StartX=14.5 StartY=20 StartZ=0 EndX=14.1465 EndY=20.3536 EndZ=0
    g14: LineSegment [constr] StartX=29.5 StartY=5 StartZ=0 EndX=29.1464 EndY=5.35355 EndZ=0
    g15: LineSegment StartX=29.1464 StartY=5.35355 StartZ=0 EndX=14.1465 EndY=20.3536 EndZ=0
    g16: LineSegment [constr] StartX=0 StartY=5 StartZ=0 EndX=0 EndY=15 EndZ=0
    g17: LineSegment StartX=29.1464 StartY=5.35355 StartZ=0 EndX=0 EndY=5.35355 EndZ=0
    g18: LineSegment StartX=0 StartY=5.35355 StartZ=0 EndX=0 EndY=25.3536 EndZ=0
    g19: LineSegment StartX=0 StartY=25.3536 StartZ=0 EndX=84 EndY=25.3536 EndZ=0
    g20: LineSegment StartX=14.1465 StartY=20.3536 StartZ=0 EndX=76.3536 EndY=20.3536 EndZ=0
  constraints (58):
    c: Distance(g0) = 7
    c: Coincident(g0,g-8)
    c: PointOnObject(g0,g-8)
    c: Coincident(g1,g-7)
    c: Coincident(g2,g-6)
    c: Coincident(g2,g1)
    c: Parallel(g2,g-6)
    c: Parallel(g1,g-7)
    c: Distance(g3) = 7
    c: Coincident(g3,g1)
    c: Parallel(g3,g-6)
    c: Distance(g4) = 0.5
    c: Coincident(g4,g0)
    c: Parallel(g-7,g4)
    c: Distance(g5) = 0.5
    c: Coincident(g5,g3)
    c: Parallel(g5,g1)
    c: Coincident(g6,g5)
    c: Coincident(g6,g4)
    c: Distance(g7) = 0.5
    c: Coincident(g7,g-9)
    c: Vertical(g7)
    c: Coincident(g8,g4)
    c: PointOnObject(g8,g7)
    c: Horizontal(g8)
    c: Distance(g9) = 20
    c: Coincident(g9,g8)
    c: Vertical(g9)
    c: Distance(g10) = 0.5
    c: Coincident(g10,g-5)
    c: PointOnObject(g10,g-3)
    c: Coincident(g11,g-6)
    c: Horizontal(g11)
    c: Coincident(g12,g10)
    c: PointOnObject(g12,g11)
    c: Parallel(g12,g-5)
    c: PointOnObject(g11,g12)
    c: Distance(g13) = 0.5
    c: Coincident(g13,g11)
    c: Parallel(g12,g13)
    c: Distance(g14) = 0.5
    c: Coincident(g14,g10)
    c: PointOnObject(g14,g12)
    c: Coincident(g15,g14)
    c: Coincident(g15,g13)
    c: Distance(g16) = 10
    c: Coincident(g16,g-4)
    c: PointOnObject(g16,g-2)
    c: Coincident(g17,g14)
    c: PointOnObject(g17,g16)
    c: Parallel(g17,g-3)
    c: Distance(g18) = 20
    c: Coincident(g18,g17)
    c: PointOnObject(g18,g-2)
    c: Coincident(g19,g18)
    c: Coincident(g19,g9)
    c: Coincident(g20,g13)
    c: Coincident(g20,g5)
FEATURE [PartDesign::Pad] Pad006
  Direction = (0,-1,2e-16)
  Length = 84
  Length2 = 10
  Placement = pos=(0,-84,2e-15) rot=(1,0,0;1.5708rad)
  Profile = -> Sketch008
  ReferenceAxis = -> Sketch008 [N_Axis]
  Refine = true
  Reversed = true
  Suppressed = false
  Type = 0
FEATURE [Sketcher::SketchObject] Sketch009
  ArcFitTolerance = 1e-06
  AttachmentSupport = -> [Pad006]
  ExternalGeometry = -> [Pad006]
  FullyConstrained = true
  MakeInternals = false
  MapMode = 5
  Placement = pos=(84,-84,2e-15) rot=(0.707107,0,0.707107;3.14159rad)
  sketch-geometry (11):
    g0: GeomPoint [constr] X=25.3536 Y=-42 Z=0
    g1: GeomPoint [constr] X=5.35355 Y=-42 Z=0
    g2: LineSegment [constr] StartX=5.35355 StartY=-42 StartZ=0 EndX=25.3536 EndY=-42 EndZ=0
    g3: LineSegment [constr] StartX=5.35355 StartY=-42 StartZ=0 EndX=12.3536 EndY=-42 EndZ=0
    g4: LineSegment [constr] StartX=12.3536 StartY=-42 StartZ=0 EndX=12.3536 EndY=-7.1e-15 EndZ=0
    g5: LineSegment [constr] StartX=12.3536 StartY=-42 StartZ=0 EndX=12.3536 EndY=-84 EndZ=0
    g6: GeomPoint [constr] X=12.3536 Y=-21 Z=0
    g7: GeomPoint [constr] X=12.3536 Y=-63 Z=0
    g8: Circle CenterX=12.3536 CenterY=-21 CenterZ=0 NormalX=0 NormalY=0 NormalZ=1 AngleXU=0 Radius=1.5
    g9: Circle CenterX=12.3536 CenterY=-42 CenterZ=0 NormalX=0 NormalY=0 NormalZ=1 AngleXU=0 Radius=1.5
    g10: Circle CenterX=12.3536 CenterY=-63 CenterZ=0 NormalX=0 NormalY=0 NormalZ=1 AngleXU=0 Radius=1.5
  constraints (21):
    c: Symmetric(g-3,g-3,g0)
    c: Symmetric(g-5,g-5,g1)
    c: Coincident(g2,g1)
    c: Coincident(g2,g0)
    c: Distance(g3) = 7
    c: Coincident(g3,g1)
    c: PointOnObject(g3,g2)
    c: Coincident(g4,g3)
    c: PointOnObject(g4,g-6)
    c: Parallel(g4,g-5)
    c: Coincident(g5,g3)
    c: PointOnObject(g5,g-4)
    c: Vertical(g5)
    c: Symmetric(g4,g4,g6)
    c: Symmetric(g5,g5,g7)
    c: Diameter(g8) = 3
    c: Coincident(g8,g6)
    c: Diameter(g9) = 3
    c: Coincident(g9,g3)
    c: Diameter(g10) = 3
    c: Coincident(g10,g7)
FEATURE [PartDesign::Pocket] Pocket001
  BaseFeature = -> Pad006
  Direction = (-1,0,2e-16)
  Length = 20
  Length2 = 5
  Placement = pos=(0,-84,2e-15) rot=(1,0,0;1.5708rad)
  Profile = -> Sketch009
  ReferenceAxis = -> Sketch009 [N_Axis]
  Refine = true
  Suppressed = false
  Type = 0
FEATURE [Sketcher::SketchObject] Sketch010
  ArcFitTolerance = 1e-06
  AttachmentSupport = -> [Pocket001]
  ExternalGeometry = -> [Pocket001]
  FullyConstrained = true
  MakeInternals = false
  MapMode = 5
  Placement = pos=(7.71195e-08,-84,20.3536) rot=(1,0,0;3.14159rad)
  sketch-geometry (8):
    g0: LineSegment [constr] StartX=14.1465 StartY=0 StartZ=0 EndX=41.9965 EndY=0 EndZ=0
    g1: LineSegment [constr] StartX=41.9965 StartY=0 StartZ=0 EndX=41.9965 EndY=-84 EndZ=0
    g2: GeomPoint [constr] X=41.9965 Y=-42 Z=0
    g3: LineSegment StartX=35.4965 StartY=-47 StartZ=0 EndX=48.4965 EndY=-47 EndZ=0
    g4: LineSegment StartX=48.4965 StartY=-47 StartZ=0 EndX=48.4965 EndY=-37 EndZ=0
    g5: LineSegment StartX=48.4965 StartY=-37 StartZ=0 EndX=35.4965 EndY=-37 EndZ=0
    g6: LineSegment StartX=35.4965 StartY=-37 StartZ=0 EndX=35.4965 EndY=-47 EndZ=0
    g7: GeomPoint [constr] X=41.9965 Y=-42 Z=0
  constraints (19):
    c: Distance(g0) = 27.85
    c: Coincident(g0,g-3)
    c: PointOnObject(g0,g-3)
    c: Coincident(g1,g0)
    c: PointOnObject(g1,g-4)
    c: Vertical(g1)
    c: Symmetric(g1,g1,g2)
    c: Coincident(g3,g4)
    c: Coincident(g4,g5)
    c: Coincident(g5,g6)
    c: Coincident(g6,g3)
    c: Horizontal(g3)
    c: Horizontal(g5)
    c: Vertical(g4)
    c: Vertical(g6)
    c: Symmetric(g5,g3,g7)
    c: Distance(g4,g6) = 13
    c: Distance(g3,g5) = 10
    c: Coincident(g7,g2)
FEATURE [PartDesign::Pocket] Pocket002
  BaseFeature = -> Pocket001
  Direction = (3.78899e-09,0,1)
  Length = 0.5
  Length2 = 5
  Placement = pos=(0,-84,2e-15) rot=(1,0,0;1.5708rad)
  Profile = -> Sketch010
  ReferenceAxis = -> Sketch010 [N_Axis]
  Refine = true
  Suppressed = false
  Type = 0
FEATURE [Sketcher::SketchObject] Sketch011
  ArcFitTolerance = 1e-06
  AttachmentSupport = -> [Pocket002]
  ExternalGeometry = -> [Pocket002]
  FullyConstrained = true
  MakeInternals = false
  MapMode = 5
  Placement = pos=(7.9014e-08,-84,20.8536) rot=(1,0,0;3.14159rad)
  sketch-geometry (2):
    g0: LineSegment [constr] StartX=41.9965 StartY=-37 StartZ=0 EndX=41.9965 EndY=-47 EndZ=0
    g1: Circle CenterX=41.9965 CenterY=-42 CenterZ=0 NormalX=0 NormalY=0 NormalZ=1 AngleXU=0 Radius=1.55
  constraints (4):
    c: Symmetric(g-3,g-3,g0)
    c: Symmetric(g-5,g-5,g0)
    c: Diameter(g1) = 3.1
    c: Symmetric(g0,g0,g1)
FEATURE [PartDesign::Pocket] Pocket003
  BaseFeature = -> Pocket002
  Direction = (3.78899e-09,0,1)
  Length = 5
  Length2 = 5
  Placement = pos=(0,-84,2e-15) rot=(1,0,0;1.5708rad)
  Profile = -> Sketch011
  ReferenceAxis = -> Sketch011 [N_Axis]
  Refine = true
  Suppressed = false
  Type = 0
FEATURE [Sketcher::SketchObject] Sketch012
  ArcFitTolerance = 1e-06
  AttachmentSupport = -> [Pocket003]
  ExternalGeometry = -> [Pocket003]
  FullyConstrained = true
  MakeInternals = false
  MapMode = 5
  Placement = pos=(7.11416e-08,-84,25.3536) rot=(0,0,1;3.14159rad)
  sketch-geometry (20):
    g0: LineSegment [constr] StartX=-84 StartY=1.42e-14 StartZ=0 EndX=-84 EndY=-5 EndZ=0
    g1: LineSegment [constr] StartX=-84 StartY=-5 StartZ=0 EndX=-79 EndY=-5 EndZ=0
    g2: LineSegment [constr] StartX=-79 StartY=-5 StartZ=0 EndX=-79 EndY=1.42e-14 EndZ=0
    g3: LineSegment [constr] StartX=-79 StartY=1.42e-14 StartZ=0 EndX=-84 EndY=1.42e-14 EndZ=0
    g4: LineSegment [constr] StartX=-84 StartY=-84 StartZ=0 EndX=-79 EndY=-84 EndZ=0
    g5: LineSegment [constr] StartX=-79 StartY=-84 StartZ=0 EndX=-79 EndY=-79 EndZ=0
    g6: LineSegment [constr] StartX=-79 StartY=-79 StartZ=0 EndX=-84 EndY=-79 EndZ=0
    g7: LineSegment [constr] StartX=-84 StartY=-79 StartZ=0 EndX=-84 EndY=-84 EndZ=0
    g8: LineSegment [constr] StartX=0 StartY=0 StartZ=0 EndX=-5 EndY=0 EndZ=0
    g9: LineSegment [constr] StartX=-5 StartY=0 StartZ=0 EndX=-5 EndY=-5 EndZ=0
    g10: LineSegment [constr] StartX=-5 StartY=-5 StartZ=0 EndX=0 EndY=-5 EndZ=0
    g11: LineSegment [constr] StartX=0 StartY=-5 StartZ=0 EndX=0 EndY=0 EndZ=0
    g12: LineSegment [constr] StartX=7.11416e-08 StartY=-84 StartZ=0 EndX=7.11416e-08 EndY=-79 EndZ=0
    g13: LineSegment [constr] StartX=7.11416e-08 StartY=-79 StartZ=0 EndX=-5 EndY=-79 EndZ=0
    g14: LineSegment [constr] StartX=-5 StartY=-79 StartZ=0 EndX=-5 EndY=-84 EndZ=0
    g15: LineSegment [constr] StartX=-5 StartY=-84 StartZ=0 EndX=7.11416e-08 EndY=-84 EndZ=0
    g16: Circle CenterX=-79 CenterY=-5 CenterZ=0 NormalX=0 NormalY=0 NormalZ=1 AngleXU=0 Radius=1.35
    g17: Circle CenterX=-79 CenterY=-79 CenterZ=0 NormalX=0 NormalY=0 NormalZ=1 AngleXU=0 Radius=1.35
    g18: Circle CenterX=-5 CenterY=-79 CenterZ=0 NormalX=0 NormalY=0 NormalZ=1 AngleXU=0 Radius=1.35
    g19: Circle CenterX=-5 CenterY=-5 CenterZ=0 NormalX=0 NormalY=0 NormalZ=1 AngleXU=0 Radius=1.35
  constraints (52):
    c: Coincident(g0,g1)
    c: Coincident(g1,g2)
    c: Coincident(g2,g3)
    c: Coincident(g3,g0)
    c: Vertical(g0)
    c: Vertical(g2)
    c: Horizontal(g1)
    c: Horizontal(g3)
    c: Distance(g0,g2) = 5
    c: Distance(g1,g3) = 5
    c: Coincident(g0,g-4)
    c: Coincident(g4,g5)
    c: Coincident(g5,g6)
    c: Coincident(g6,g7)
    c: Coincident(g7,g4)
    c: Horizontal(g4)
    c: Horizontal(g6)
    c: Vertical(g5)
    c: Vertical(g7)
    c: Distance(g5,g7) = 5
    c: Distance(g4,g6) = 5
    c: Coincident(g4,g-6)
    c: Coincident(g8,g9)
    c: Coincident(g9,g10)
    c: Coincident(g10,g11)
    c: Coincident(g11,g8)
    c: Horizontal(g8)
    c: Horizontal(g10)
    c: Vertical(g9)
    c: Vertical(g11)
    c: Distance(g9,g11) = 5
    c: Distance(g8,g10) = 5
    c: Coincident(g8,g-1)
    c: Coincident(g12,g13)
    c: Coincident(g13,g14)
    c: Coincident(g14,g15)
    c: Coincident(g15,g12)
    c: Vertical(g12)
    c: Vertical(g14)
    c: Horizontal(g13)
    c: Horizontal(g15)
    c: Distance(g12,g14) = 5
    c: Distance(g13,g15) = 5
    c: Coincident(g12,g-6)
    c: Diameter(g16) = 2.7
    c: Coincident(g16,g1)
    c: Diameter(g17) = 2.7
    c: Coincident(g17,g5)
    c: Diameter(g18) = 2.7
    c: Coincident(g18,g13)
    c: Diameter(g19) = 2.7
    c: Coincident(g19,g9)
FEATURE [PartDesign::Pocket] Pocket004
  BaseFeature = -> Pocket003
  Direction = (-2.80598e-09,0,-1)
  Length = 5
  Length2 = 5
  Placement = pos=(0,-84,2e-15) rot=(1,0,0;1.5708rad)
  Profile = -> Sketch012
  ReferenceAxis = -> Sketch012 [N_Axis]
  Refine = true
  Suppressed = false
  Type = 0
FEATURE [Sketcher::SketchObject] Sketch013
  ArcFitTolerance = 1e-06
  AttachmentSupport = -> [Pocket004]
  ExternalGeometry = -> [Pocket004]
  FullyConstrained = true
  MakeInternals = false
  MapMode = 5
  Placement = pos=(7.11416e-08,-84,25.3536) rot=(0,0,1;3.14159rad)
  sketch-geometry (4):
    g0: LineSegment [constr] StartX=7.11416e-08 StartY=-42 StartZ=0 EndX=-5 EndY=-42 EndZ=0
    g1: Circle CenterX=-5 CenterY=-42 CenterZ=0 NormalX=0 NormalY=0 NormalZ=1 AngleXU=0 Radius=1.35
    g2: LineSegment [constr] StartX=-84 StartY=-42 StartZ=0 EndX=-79 EndY=-42 EndZ=0
    g3: Circle CenterX=-79 CenterY=-42 CenterZ=0 NormalX=0 NormalY=0 NormalZ=1 AngleXU=0 Radius=1.35
  constraints (10):
    c: Distance(g0) = 5
    c: Symmetric(g-3,g-3,g0)
    c: Horizontal(g0)
    c: Diameter(g1) = 2.7
    c: Coincident(g1,g0)
    c: Distance(g2) = 5
    c: Symmetric(g-4,g-4,g2)
    c: Horizontal(g2)
    c: Diameter(g3) = 2.7
    c: Coincident(g3,g2)
FEATURE [PartDesign::Pocket] Pocket005
  BaseFeature = -> Pocket004
  Direction = (-2.80598e-09,0,-1)
  Length = 22
  Length2 = 5
  Placement = pos=(0,-84,2e-15) rot=(1,0,0;1.5708rad)
  Profile = -> Sketch013
  ReferenceAxis = -> Sketch013 [N_Axis]
  Refine = true
  Suppressed = false
  Type = 0
FEATURE [PartDesign::ShapeBinder] ShapeBinder002
  Support = -> [Pocket005]
  TraceSupport = false
FEATURE [PartDesign::ShapeBinder] CopyPocket005
  Placement = pos=(0,-84,2e-15) rot=(1,0,0;1.5708rad)
  TraceSupport = false
FEATURE [PartDesign::Plane] DatumPlane005
  AttachmentSupport = -> [CopyPocket005]
  Length = 91.117
  MapMode = 5
  Placement = pos=(7.9014e-08,-84,20.8536) rot=(1,0,0;3.14159rad)
  ResizeMode = 0
  Width = 126.87
FEATURE [Sketcher::SketchObject] Sketch014
  ArcFitTolerance = 1e-06
  AttachmentSupport = -> [DatumPlane005]
  ExternalGeometry = -> [ShapeBinder002]
  FullyConstrained = true
  MakeInternals = false
  MapMode = 5
  Placement = pos=(7.9014e-08,-84,20.8536) rot=(1,0,0;3.14159rad)
  sketch-geometry (6):
    g0: Circle CenterX=41.9965 CenterY=-42 CenterZ=0 NormalX=0 NormalY=0 NormalZ=1 AngleXU=0 Radius=1.35
    g1: LineSegment StartX=35.7465 StartY=-46.75 StartZ=0 EndX=48.2465 EndY=-46.75 EndZ=0
    g2: LineSegment StartX=48.2465 StartY=-46.75 StartZ=0 EndX=48.2465 EndY=-37.25 EndZ=0
    g3: LineSegment StartX=48.2465 StartY=-37.25 StartZ=0 EndX=35.7465 EndY=-37.25 EndZ=0
    g4: LineSegment StartX=35.7465 StartY=-37.25 StartZ=0 EndX=35.7465 EndY=-46.75 EndZ=0
    g5: GeomPoint [constr] X=41.9965 Y=-42 Z=0
  constraints (14):
    c: Diameter(g0) = 2.7
    c: Coincident(g0,g-4)
    c: Coincident(g1,g2)
    c: Coincident(g2,g3)
    c: Coincident(g3,g4)
    c: Coincident(g4,g1)
    c: Horizontal(g1)
    c: Horizontal(g3)
    c: Vertical(g2)
    c: Vertical(g4)
    c: Symmetric(g3,g1,g5)
    c: Distance(g2,g4) = 12.5
    c: Distance(g1,g3) = 9.5
    c: Coincident(g5,g0)
FEATURE [PartDesign::Pad] Pad007
  Direction = (-3.78899e-09,0,-1)
  Length = 3
  Length2 = 10
  Placement = pos=(7.9014e-08,-84,20.8536) rot=(1,0,0;3.14159rad)
  Profile = -> Sketch014
  ReferenceAxis = -> Sketch014 [N_Axis]
  Refine = true
  Suppressed = false
  Type = 0
FEATURE [Sketcher::SketchObject] Sketch015
  ArcFitTolerance = 1e-06
  AttachmentSupport = -> [Pad007]
  ExternalGeometry = -> [Pad007]
  FullyConstrained = true
  MakeInternals = false
  MapMode = 5
  Placement = pos=(6.7647e-08,-84,17.8536) rot=(1,0,0;3.14159rad)
  sketch-geometry (4):
    g0: LineSegment StartX=35.7465 StartY=-37.25 StartZ=0 EndX=35.7465 EndY=-46.75 EndZ=0
    g1: LineSegment StartX=35.7465 StartY=-46.75 StartZ=0 EndX=48.2465 EndY=-46.75 EndZ=0
    g2: LineSegment StartX=48.2465 StartY=-46.75 StartZ=0 EndX=48.2465 EndY=-37.25 EndZ=0
    g3: LineSegment StartX=48.2465 StartY=-37.25 StartZ=0 EndX=35.7465 EndY=-37.25 EndZ=0
  constraints (10):
    c: Coincident(g0,g1)
    c: Coincident(g1,g2)
    c: Coincident(g2,g3)
    c: Coincident(g3,g0)
    c: Vertical(g0)
    c: Vertical(g2)
    c: Horizontal(g1)
    c: Horizontal(g3)
    c: Coincident(g0,g-6)
    c: Coincident(g1,g-5)
FEATURE [PartDesign::Pad] Pad008
  BaseFeature = -> Pad007
  Direction = (-3.78899e-09,0,-1)
  Length = 8
  Length2 = 10
  Placement = pos=(7.9014e-08,-84,20.8536) rot=(1,0,0;3.14159rad)
  Profile = -> Sketch015
  ReferenceAxis = -> Sketch015 [N_Axis]
  Refine = true
  Suppressed = false
  Type = 0
FEATURE [Sketcher::SketchObject] Sketch016
  ArcFitTolerance = 1e-06
  AttachmentSupport = -> [Pad008]
  ExternalGeometry = -> [Pad008]
  FullyConstrained = true
  MakeInternals = false
  MapMode = 5
  Placement = pos=(7.9014e-08,-46.75,20.8536) rot=(0,0.707107,-0.707107;3.14159rad)
  sketch-geometry (2):
    g0: LineSegment [constr] StartX=-41.9965 StartY=0 StartZ=0 EndX=-41.9965 EndY=7 EndZ=0
    g1: Circle CenterX=-41.9965 CenterY=7 CenterZ=0 NormalX=0 NormalY=0 NormalZ=1 AngleXU=0 Radius=2.5
  constraints (5):
    c: Distance(g0) = 7
    c: Symmetric(g-6,g-6,g0)
    c: Vertical(g0)
    c: Diameter(g1) = 5
    c: Coincident(g1,g0)
FEATURE [PartDesign::Hole] Hole001
  BaseFeature = -> Pad008
  CustomThreadClearance = 0
  Depth = 12.72
  DepthType = 0
  Diameter = 4.2
  DrillForDepth = false
  DrillPoint = 1
  DrillPointAngle = 118
  HoleCutCountersinkAngle = 90
  HoleCutCustomValues = false
  HoleCutDepth = 0
  HoleCutDiameter = 6.1
  HoleCutType = 0
  ModelThread = false
  Placement = pos=(7.9014e-08,-84,20.8536) rot=(1,0,0;3.14159rad)
  Profile = -> Sketch016
  Refine = true
  Suppressed = false
  Tapered = false
  TaperedAngle = 90
  ThreadClass = 0
  ThreadDepth = 12.72
  ThreadDepthType = 0
  ThreadDirection = 0
  ThreadFit = 0
  ThreadSize = 13
  ThreadType = 1
  Threaded = true
  UseCustomThreadClearance = false
FEATURE [Sketcher::SketchObject] Sketch017
  ArcFitTolerance = 1e-06
  AttachmentSupport = -> [Hole001]
  ExternalGeometry = -> [Hole001]
  FullyConstrained = true
  MakeInternals = false
  MapMode = 5
  Placement = pos=(7.9014e-08,-46.75,20.8536) rot=(0,0.707107,-0.707107;3.14159rad)
  sketch-geometry (4):
    g0: LineSegment [constr] StartX=-48.2465 StartY=0 StartZ=0 EndX=-48.2465 EndY=2.5 EndZ=0
    g1: LineSegment [constr] StartX=-35.7465 StartY=0 StartZ=0 EndX=-35.7465 EndY=2.5 EndZ=0
    g2: Circle CenterX=-48.2465 CenterY=2.5 CenterZ=0 NormalX=0 NormalY=0 NormalZ=1 AngleXU=0 Radius=1
    g3: Circle CenterX=-35.7465 CenterY=2.5 CenterZ=0 NormalX=0 NormalY=0 NormalZ=1 AngleXU=0 Radius=1
  constraints (10):
    c: Distance(g0) = 2.5
    c: Coincident(g0,g-6)
    c: PointOnObject(g0,g-3)
    c: Distance(g1) = 2.5
    c: Coincident(g1,g-6)
    c: PointOnObject(g1,g-5)
    c: Diameter(g2) = 2
    c: Coincident(g2,g0)
    c: Diameter(g3) = 2
    c: Coincident(g3,g1)
FEATURE [PartDesign::Pocket] Pocket006
  BaseFeature = -> Hole001
  Direction = (0,1,2e-16)
  Length = 10
  Length2 = 5
  Placement = pos=(7.9014e-08,-84,20.8536) rot=(1,0,0;3.14159rad)
  Profile = -> Sketch017
  ReferenceAxis = -> Sketch017 [N_Axis]
  Refine = true
  Suppressed = false
  Type = 0
FEATURE [PartDesign::Chamfer] Chamfer013
  Angle = 45
  Base = -> Pocket006 [Edge30,Edge29]
  BaseFeature = -> Pocket006
  ChamferType = 0
  FlipDirection = false
  Placement = pos=(7.9014e-08,-84,20.8536) rot=(1,0,0;3.14159rad)
  Refine = true
  Size = 3
  Size2 = 1
  SupportTransform = false
  Suppressed = false
  UseAllEdges = false
FEATURE [PartDesign::Body] Body003  label="PlateThreadBlock"
  AllowCompound = false
  Group = -> [ShapeBinder002,DatumPlane005,CopyPocket005,Sketch014,Pad007,Sketch015,Pad008,Sketch016,Hole001,Sketch017,Pocket006,Chamfer013]
  Origin = -> Origin003
  Tip = -> Chamfer013
FEATURE [PartDesign::FeatureBase] Clone
  BaseFeature = -> Body003
  Suppressed = false
FEATURE [Sketcher::SketchObject] Sketch018
  ArcFitTolerance = 1e-06
  AttachmentSupport = -> [Clone]
  ExternalGeometry = -> [Clone]
  FullyConstrained = true
  MakeInternals = false
  MapMode = 5
  Placement = pos=(0,-46.75,0) rot=(1,0,0;1.5708rad)
  sketch-geometry (1):
    g0: Circle CenterX=41.9965 CenterY=13.8536 CenterZ=0 NormalX=0 NormalY=0 NormalZ=1 AngleXU=0 Radius=2.5
  constraints (2):
    c: Diameter(g0) = 5
    c: Coincident(g0,g-3)
FEATURE [PartDesign::Hole] Hole002
  BaseFeature = -> Clone
  CustomThreadClearance = 0.2
  Depth = 25
  DepthType = 0
  Diameter = 5.2
  DrillForDepth = false
  DrillPoint = 1
  DrillPointAngle = 118
  HoleCutCountersinkAngle = 90
  HoleCutCustomValues = false
  HoleCutDepth = 0
  HoleCutDiameter = 6.1
  HoleCutType = 0
  ModelThread = true
  Profile = -> Sketch018
  Refine = true
  Suppressed = false
  Tapered = false
  TaperedAngle = 90
  ThreadClass = 0
  ThreadDepth = 25
  ThreadDepthType = 0
  ThreadDirection = 0
  ThreadFit = 0
  ThreadSize = 14
  ThreadType = 1
  Threaded = true
  UseCustomThreadClearance = true
FEATURE [PartDesign::ShapeBinder] ShapeBinder003
  Placement = pos=(0,-84,2e-14) rot=(1,0,0;1.5708rad)
  Support = -> [Fillet]
  TraceSupport = false
FEATURE [PartDesign::Plane] DatumPlane006
  AttachmentSupport = -> [ShapeBinder003]
  Length = 62.1898
  MapMode = 11
  Placement = pos=(42,-84,14) rot=(0.57735,-0.57735,0.57735;2.0944rad)
  ResizeMode = 0
  Width = 86.4857
FEATURE [Sketcher::SketchObject] Sketch019
  ArcFitTolerance = 1e-06
  AttachmentSupport = -> [DatumPlane006]
  ExternalGeometry = -> [ShapeBinder003]
  FullyConstrained = true
  MakeInternals = false
  MapMode = 5
  Placement = pos=(42,-84,14) rot=(0.57735,-0.57735,0.57735;2.0944rad)
  sketch-geometry (1):
    g0: Circle CenterX=0 CenterY=0 CenterZ=0 NormalX=0 NormalY=0 NormalZ=1 AngleXU=0 Radius=2.9
  constraints (2):
    c: Diameter(g0) = 5.8
    c: Coincident(g0,g-1)
FEATURE [PartDesign::Pad] Pad009
  Direction = (0,-1,0)
  Length = 5
  Length2 = 10
  Placement = pos=(42,-84,14) rot=(0.57735,-0.57735,0.57735;2.0944rad)
  Profile = -> Sketch019
  ReferenceAxis = -> Sketch019 [N_Axis]
  Refine = true
  Reversed = true
  Suppressed = false
  Type = 0
FEATURE [Sketcher::SketchObject] Sketch020
  ArcFitTolerance = 1e-06
  AttachmentSupport = -> [Pad009]
  ExternalGeometry = -> [Pad009]
  FullyConstrained = true
  MakeInternals = false
  MapMode = 5
  Placement = pos=(42,-84,14) rot=(0.57735,-0.57735,0.57735;2.0944rad)
  sketch-geometry (1):
    g0: Circle CenterX=0 CenterY=0 CenterZ=0 NormalX=0 NormalY=0 NormalZ=1 AngleXU=0 Radius=3
  constraints (2):
    c: Diameter(g0) = 6
    c: Coincident(g0,g-1)
FEATURE [PartDesign::Pad] Pad010
  BaseFeature = -> Pad009
  Direction = (0,-1,0)
  Length = 15
  Length2 = 10
  Placement = pos=(42,-84,14) rot=(0.57735,-0.57735,0.57735;2.0944rad)
  Profile = -> Sketch020
  ReferenceAxis = -> Sketch020 [N_Axis]
  Refine = true
  Suppressed = false
  Type = 0
FEATURE [Sketcher::SketchObject] Sketch021
  ArcFitTolerance = 1e-06
  AttachmentSupport = -> [Pad010]
  ExternalGeometry = -> [Pad010]
  FullyConstrained = true
  MakeInternals = false
  MapMode = 5
  Placement = pos=(42,-99,14) rot=(0.57735,-0.57735,0.57735;2.0944rad)
  sketch-geometry (1):
    g0: Circle CenterX=0 CenterY=0 CenterZ=0 NormalX=0 NormalY=0 NormalZ=1 AngleXU=0 Radius=7.5
  constraints (2):
    c: Diameter(g0) = 15
    c: Coincident(g0,g-1)
FEATURE [PartDesign::Pad] Pad011
  BaseFeature = -> Pad010
  Direction = (0,-1,0)
  Length = 20
  Length2 = 10
  Placement = pos=(42,-84,14) rot=(0.57735,-0.57735,0.57735;2.0944rad)
  Profile = -> Sketch021
  ReferenceAxis = -> Sketch021 [N_Axis]
  Refine = true
  Suppressed = false
  Type = 0
FEATURE [Sketcher::SketchObject] Sketch022
  ArcFitTolerance = 1e-06
  AttachmentSupport = -> [Pad011]
  ExternalGeometry = -> [Pad011]
  FullyConstrained = true
  MakeInternals = false
  MapMode = 5
  Placement = pos=(42,-119,14) rot=(0.57735,-0.57735,0.57735;2.0944rad)
  sketch-geometry (17):
    g0: LineSegment [constr] StartX=-5.29923e-11 StartY=5.2929e-11 StartZ=0 EndX=-5.29923e-11 EndY=7.5 EndZ=0
    g1: LineSegment [constr] StartX=-5.29923e-11 StartY=5.2929e-11 StartZ=0 EndX=7.5 EndY=5.2929e-11 EndZ=0
    g2: LineSegment [constr] StartX=-5.29923e-11 StartY=5.2929e-11 StartZ=0 EndX=-5.29923e-11 EndY=-7.5 EndZ=0
    g3: LineSegment [constr] StartX=-5.29923e-11 StartY=5.2929e-11 StartZ=0 EndX=-7.5 EndY=5.2929e-11 EndZ=0
    g4: LineSegment [constr] StartX=-5.29923e-11 StartY=5.2929e-11 StartZ=0 EndX=-5.3033 EndY=5.3033 EndZ=0
    g5: LineSegment [constr] StartX=-5.29923e-11 StartY=5.2929e-11 StartZ=0 EndX=5.3033 EndY=5.3033 EndZ=0
    g6: LineSegment [constr] StartX=-5.29923e-11 StartY=5.2929e-11 StartZ=0 EndX=5.3033 EndY=-5.3033 EndZ=0
    g7: LineSegment [constr] StartX=-5.29923e-11 StartY=5.2929e-11 StartZ=0 EndX=-5.3033 EndY=-5.3033 EndZ=0
    g8: Circle CenterX=-5.3033 CenterY=5.3033 CenterZ=0 NormalX=0 NormalY=0 NormalZ=1 AngleXU=0 Radius=1.34e-13
    g9: Circle CenterX=-5.3033 CenterY=5.3033 CenterZ=0 NormalX=0 NormalY=0 NormalZ=1 AngleXU=0 Radius=1.75
    g10: Circle CenterX=-7.5 CenterY=5.2929e-11 CenterZ=0 NormalX=0 NormalY=0 NormalZ=1 AngleXU=0 Radius=1.75
    g11: Circle CenterX=-5.3033 CenterY=-5.3033 CenterZ=0 NormalX=0 NormalY=0 NormalZ=1 AngleXU=0 Radius=1.75
    g12: Circle CenterX=-5.29923e-11 CenterY=-7.5 CenterZ=0 NormalX=0 NormalY=0 NormalZ=1 AngleXU=0 Radius=1.75
    g13: Circle CenterX=5.3033 CenterY=-5.3033 CenterZ=0 NormalX=0 NormalY=0 NormalZ=1 AngleXU=0 Radius=1.75
    g14: Circle CenterX=7.5 CenterY=5.2929e-11 CenterZ=0 NormalX=0 NormalY=0 NormalZ=1 AngleXU=0 Radius=1.75
    g15: Circle CenterX=5.3033 CenterY=5.3033 CenterZ=0 NormalX=0 NormalY=0 NormalZ=1 AngleXU=0 Radius=1.75
    g16: Circle CenterX=-5.29923e-11 CenterY=7.5 CenterZ=0 NormalX=0 NormalY=0 NormalZ=1 AngleXU=0 Radius=1.75
  constraints (42):
    c: Coincident(g0,g-1)
    c: PointOnObject(g0,g-3)
    c: Vertical(g0)
    c: Coincident(g1,g0)
    c: PointOnObject(g1,g-3)
    c: Horizontal(g1)
    c: Coincident(g2,g0)
    c: PointOnObject(g2,g-3)
    c: Vertical(g2)
    c: Coincident(g3,g0)
    c: PointOnObject(g3,g-3)
    c: Horizontal(g3)
    c: Angle(g-1,g4) = 2.35619
    c: Coincident(g4,g0)
    c: PointOnObject(g4,g-3)
    c: Angle(g-1,g5) = 0.785398
    c: Coincident(g5,g0)
    c: PointOnObject(g5,g-3)
    c: Angle(g-1,g6) = -0.785398
    c: Coincident(g6,g0)
    c: PointOnObject(g6,g-3)
    c: Angle(g-1,g7) = -2.35619
    c: Coincident(g7,g0)
    c: PointOnObject(g7,g-3)
    c: Coincident(g8,g4)
    c: Tangent(g8,g-3)
    c: Diameter(g9) = 3.5
    c: Coincident(g9,g4)
    c: Diameter(g10) = 3.5
    c: Coincident(g10,g3)
    c: Diameter(g11) = 3.5
    c: Coincident(g11,g7)
    c: Diameter(g12) = 3.5
    c: Coincident(g12,g2)
    c: Diameter(g13) = 3.5
    c: Coincident(g13,g6)
    c: Diameter(g14) = 3.5
    c: Coincident(g14,g1)
    c: Diameter(g15) = 3.5
    c: Coincident(g15,g5)
    c: Diameter(g16) = 3.5
    c: Coincident(g16,g0)
FEATURE [PartDesign::Pocket] Pocket007
  BaseFeature = -> Pad011
  Direction = (0,1,0)
  Length = 50
  Length2 = 5
  Placement = pos=(42,-84,14) rot=(0.57735,-0.57735,0.57735;2.0944rad)
  Profile = -> Sketch022
  ReferenceAxis = -> Sketch022 [N_Axis]
  Refine = true
  Suppressed = false
  Type = 1
FEATURE [PartDesign::Fillet] Fillet004
  Base = -> Pocket007 [Edge23]
  BaseFeature = -> Pocket007
  Placement = pos=(42,-84,14) rot=(0.57735,-0.57735,0.57735;2.0944rad)
  Radius = 4
  Refine = true
  SupportTransform = false
  Suppressed = false
  UseAllEdges = false
FEATURE [PartDesign::Point] DatumPoint
  AttacherType = Attacher::AttachEnginePoint
  AttachmentSupport = -> [Fillet004]
  MapMode = 36
  Placement = pos=(42,-79,14) rot=(0.707107,0,0.707107;3.14159rad)
FEATURE [Part::Part2DObjectPython] VThreadProfile  # Draft 2D object (typed FeaturePython)
  Area = 21.5626
  Closed = true
  Continuity = C2
  Deviation = 0.1
  Height = 74
  Helix = Helix
  Instructions = Expand this with the ... button to view instructions | Sweep this object along a helix of the same pitch to produce your thread. | It is recommended to make the helix in the ThreadProfile workbench. | If there is an active Body the ThreadProfile object will be put into it.,If not it can be dragged and dropped into the body later. | If there is an active Body when the helix is made there will be made a ShapeBinder for it | For internal threads you will need to cut the Sweep object out of a cylinder, or if using Part Design sweep it as a Subtractive Pipe. | Always use Frenet mode | I have provided some presets, but it is possible there could be some errors.  Double check for mission critical applications. | Also, the tolerances might be different from what you wish to have.  I believe the internal minor diameters are all minimum and the external are all maximum.
  InternalOrExternal = 1
  MakeFace = true
  MinorDiameter = 4.773
  Parameterization = 1
  Pitch = 1
  Placement = pos=(42,-79,14) rot=(1,0,0;-1.5708rad)
  Points = (66) [(2.37314,0.228827,0),(2.31975,0.451556,0),(2.25136,0.667864,0),(2.16643,0.876642,0),(2.06474,1.07659,0),(1.94661,1.26636,0),(1.81267,1.44463,0),+59 more]
  Presets = 16
  Quality = 11
  ThreadCount = 74
  Variants = 0
  Version = 1.92
  external2S_data = [-0.00461051,-0.00886426,-0.0128148,-0.0165028,-0.0199596,-0.0232105,-0.0262759,-0.0291725,-0.0319145,-0.0345137,-0.0369805,-0.0393235,-0.0415505,-0.0436681,-0.0456823,-0.0475981,-0.0494204,-0.0511532,-0.0528003,-0.0543649,-0.0558502,+698 more]
  external3S_data = [-0.00677828,-0.0128149,-0.0182584,-0.0232106,-0.0277444,-0.0319145,-0.0357632,-0.0393236,-0.0426227,-0.0456823,-0.0485208,-0.0511533,-0.0535928,-0.0558503,-0.0579353,-0.059856,-0.0616195,-0.0632319,-0.0646984,-0.0660239,-0.0672123,+698 more]
  external45_data = [-0.00137363,-0.00271738,-0.00403219,-0.00531893,-0.00657844,-0.00781148,-0.00901878,-0.010201,-0.0113589,-0.012493,-0.0136039,-0.0146921,-0.0157583,-0.0168028,-0.0178261,-0.0188288,-0.0198112,-0.0207738,-0.0217169,-0.0226409,-0.0235462,+698 more]
  external_data = [-0.00235387,-0.00461052,-0.00677828,-0.00886428,-0.0108747,-0.0128149,-0.0146895,-0.0165028,-0.0182584,-0.0199597,-0.0216095,-0.0232106,-0.0247653,-0.0262759,-0.0277444,-0.0291725,-0.0305621,-0.0319145,-0.0332313,-0.0345138,-0.0357632,+698 more]
  internal2S_data = [0,0,0,0,0,0,0,0,0,0,0,0,0,0,0,0,0,0,0,0,0,0,0,0,0,0,0,0,0,0,0,0,0,0,0,0,0,0,0,0,0,0,0,0,0,0,0,0,0,0,0,0,0,0,0,0,0,0,0,0,0,0,0,0,0,0,0,0,0,0,0,0,0,0,0,0,0,0,0,0,0,0,0,0,0,0,0,0,0,0,0.00481128,0.00962256,0.0144338,0.0192451,0.0240564,+624 more]
  internal3S_data = [0,0,0,0,0,0,0,0,0,0,0,0,0,0,0,0,0,0,0,0,0,0,0,0,0,0,0,0,0,0,0,0,0,0,0,0,0,0,0,0,0,0,0,0,0,0,0,0,0,0,0,0,0,0,0,0,0,0,0,0,0.00721688,0.0144338,0.0216506,0.0288675,0.0360844,0.0433013,0.0505181,0.057735,0.0649519,0.0721688,0.0793857,0.0866025,+647 more]
  internal45_data = [0,0,0,0,0,0,0,0,0,0,0,0,0,0,0,0,0,0,0,0,0,0,0,0,0,0,0,0,0,0,0,0,0,0,0,0,0,0,0,0,0,0,0,0,0,0,0,0,0,0,0,0,0,0,0,0,0,0,0,0,0,0,0,0,0,0,0,0,0,0,0,0,0,0,0,0,0,0,0,0,0,0,0,0,0,0,0,0,0,0,0,0,0,0,0,0,0,0,0,0,0,0,0,0,0,0,0,0,0,0,0,0,0,0,0,0,0,0,0,0,+599 more]
  internal_data = [0,0,0,0,0,0,0,0,0,0,0,0,0,0,0,0,0,0,0,0,0,0,0,0,0,0,0,0,0,0,0,0,0,0,0,0,0,0,0,0,0,0,0,0,0,0,0,0,0,0,0,0,0,0,0,0,0,0,0,0,0,0,0,0,0,0,0,0,0,0,0,0,0,0,0,0,0,0,0,0,0,0,0,0,0,0,0,0,0,0,0,0,0,0,0,0,0,0,0,0,0,0,0,0,0,0,0,0,0,0,0,0,0,0,0,0,0,0,0,0,+599 more]
  preset_names = <blob: 3959 chars omitted>
  presets_data = [0,0,0,2.20878,24.1173,24.6888,0.25,0.693,0.729,0.25,0.793,0.829,0.25,0.893,0.929,0.3,1.032,1.075,0.35,1.171,1.221,0.35,1.371,1.421,0.4,1.509,1.567,0.45,1.648,1.713,0.45,1.948,2.013,0.5,2.387,2.459,0.6,2.764,2.85,0.7,3.141,3.242,0.75,3.58,+712 more]
FEATURE [Part::Helix] Helix
  Angle = 0
  AttacherType = Attacher::AttachEngine3D
  Height = 74
  Length = 470.808
  LocalCoord = 0
  Pitch = 1
  Placement = pos=(42,-79,14) rot=(1,0,0;-1.5708rad)
  Radius = 1
  SegmentLength = 1
  Style = 0
  expr: AttachmentOffset = VThreadProfile.AttachmentOffset
  expr: AttachmentSupport = VThreadProfile.AttachmentSupport
  expr: Height = VThreadProfile.ThreadCount * VThreadProfile.Pitch
  expr: MapMode = VThreadProfile.MapMode
  expr: MapPathParameter = VThreadProfile.MapPathParameter
  expr: MapReversed = VThreadProfile.MapReversed
  expr: Pitch = VThreadProfile.Pitch
  expr: SegmentLength = 1
FEATURE [PartDesign::AdditivePipe] AdditivePipe
  AuxilleryCurvelinear = true
  AuxillerySpineTangent = false
  BaseFeature = -> Fillet004
  Binormal = (0,0,0)
  Mode = 2
  Placement = pos=(42,-84,14) rot=(0.57735,-0.57735,0.57735;2.0944rad)
  Profile = -> VThreadProfile
  Refine = true
  Spine = -> Helix [Edge1,Edge2,Edge3,Edge4,Edge5,Edge6,Edge7,Edge8,Edge9,Edge10,Edge11,Edge12,Edge13,Edge14,Edge15,Edge16,Edge17,Edge18,Edge19,Edge20,Edge21,Edge22,Edge23,Edge24,Edge25,Edge26,Edge27,Edge28,Edge29,Edge30,Edge31,Edge32,Edge33,Edge34,Edge35,Edge36,Edge37,Edge38,Edge39,Edge40,+34 more]
  SpineTangent = false
  Suppressed = false
  Transformation = 0
  Transition = 0
FEATURE [PartDesign::ShapeBinder] ShapeBinder004
  Support = -> [Fillet]
  TraceSupport = false
FEATURE [PartDesign::Plane] DatumPlane007
  AttachmentSupport = -> [AdditivePipe]
  Length = 62.19
  MapMode = 5
  Placement = pos=(42.0014,-4.99998,14) rot=(0.577354,0.577344,0.577354;4.18878rad)
  ResizeMode = 0
  Width = 86.4884
FEATURE [Sketcher::SketchObject] Sketch023
  ArcFitTolerance = 1e-06
  AttachmentSupport = -> [DatumPlane007]
  FullyConstrained = true
  MakeInternals = false
  MapMode = 5
  Placement = pos=(42.0014,-4.99998,14) rot=(0.577354,0.577344,0.577354;4.18878rad)
  sketch-geometry (1):
    g0: Circle CenterX=0 CenterY=0 CenterZ=0 NormalX=0 NormalY=0 NormalZ=1 AngleXU=0 Radius=2.9
  constraints (2):
    c: Diameter(g0) = 5.8
    c: Coincident(g0,g-1)
FEATURE [PartDesign::Pad] Pad012
  BaseFeature = -> AdditivePipe
  Direction = (1.755e-05,1,1.0234e-10)
  Length = 10
  Length2 = 10
  Placement = pos=(42,-84,14) rot=(0.57735,-0.57735,0.57735;2.0944rad)
  Profile = -> Sketch023
  ReferenceAxis = -> Sketch023 [N_Axis]
  Refine = true
  Suppressed = false
  Type = 0
FEATURE [PartDesign::ShapeBinder] CopyPocket008
  Placement = pos=(42,-84,14) rot=(0.57735,-0.57735,0.57735;2.0944rad)
  TraceSupport = false
FEATURE [PartDesign::Plane] DatumPlane008
  AttachmentSupport = -> [CopyPocket008]
  Length = 61.9575
  MapMode = 5
  Placement = pos=(41.9985,5.00002,14) rot=(-0.577347,-0.577357,-0.577347;2.09438rad)
  ResizeMode = 0
  Width = 83.4479
FEATURE [Sketcher::SketchObject] Sketch025
  ArcFitTolerance = 1e-06
  AttachmentSupport = -> [DatumPlane008]
  ExternalGeometry = -> [CopyPocket008]
  FullyConstrained = true
  MakeInternals = false
  MapMode = 5
  Placement = pos=(41.9985,5.00002,14) rot=(-0.577347,-0.577357,-0.577347;2.09438rad)
  sketch-geometry (2):
    g0: Circle CenterX=0 CenterY=0 CenterZ=0 NormalX=0 NormalY=0 NormalZ=1 AngleXU=0 Radius=1.55
    g1: Circle CenterX=0 CenterY=0 CenterZ=0 NormalX=0 NormalY=0 NormalZ=1 AngleXU=0 Radius=4.5
  constraints (4):
    c: Diameter(g0) = 3.1
    c: Coincident(g0,g-1)
    c: Diameter(g1) = 9
    c: Coincident(g1,g0)
FEATURE [PartDesign::Pad] Pad013
  Direction = (-1.75232e-05,1,-4.99912e-10)
  Length = 3
  Length2 = 10
  Placement = pos=(41.9985,5.00002,14) rot=(-0.577347,-0.577357,-0.577347;2.09438rad)
  Profile = -> Sketch025
  ReferenceAxis = -> Sketch025 [N_Axis]
  Refine = true
  Suppressed = false
  Type = 0
FEATURE [PartDesign::Plane] DatumPlane009
  AttachmentSupport = -> [Pad013]
  Length = 61.9575
  MapMode = 5
  Placement = pos=(41.9984,8.00002,14) rot=(-0.577347,-0.577357,-0.577347;2.09438rad)
  ResizeMode = 0
  Width = 83.4479
FEATURE [Sketcher::SketchObject] Sketch026
  ArcFitTolerance = 1e-06
  AttachmentSupport = -> [DatumPlane009]
  ExternalGeometry = -> [Pad013]
  FullyConstrained = true
  MakeInternals = false
  MapMode = 5
  Placement = pos=(41.9984,8.00002,14) rot=(-0.577347,-0.577357,-0.577347;2.09438rad)
  sketch-geometry (2):
    g0: Circle CenterX=0 CenterY=0 CenterZ=0 NormalX=0 NormalY=0 NormalZ=1 AngleXU=0 Radius=4.50001
    g1: Circle CenterX=0 CenterY=0 CenterZ=0 NormalX=0 NormalY=0 NormalZ=1 AngleXU=0 Radius=3.1
  constraints (4):
    c: Coincident(g0,g-1)
    c: Tangent(g0,g-3)
    c: Diameter(g1) = 6.2
    c: Coincident(g1,g0)
FEATURE [PartDesign::Pad] Pad014
  BaseFeature = -> Pad013
  Direction = (-1.75232e-05,1,-4.99912e-10)
  Length = 6
  Length2 = 10
  Placement = pos=(41.9985,5.00002,14) rot=(-0.577347,-0.577357,-0.577347;2.09438rad)
  Profile = -> Sketch026
  ReferenceAxis = -> Sketch026 [N_Axis]
  Refine = true
  Suppressed = false
  Type = 0
FEATURE [PartDesign::Chamfer] Chamfer014
  Angle = 45
  Base = -> Pad014 [Edge11]
  BaseFeature = -> Pad014
  ChamferType = 0
  FlipDirection = false
  Placement = pos=(41.9985,5.00002,14) rot=(-0.577347,-0.577357,-0.577347;2.09438rad)
  Refine = true
  Size = 0.5
  Size2 = 1
  SupportTransform = false
  Suppressed = false
  UseAllEdges = false
FEATURE [PartDesign::Body] Body006  label="Adjustor Cap"
  AllowCompound = false
  Group = -> [DatumPlane008,CopyPocket008,Sketch025,Pad013,DatumPlane009,Sketch026,Pad014,Chamfer014]
  Origin = -> Origin006
  Tip = -> Chamfer014
FEATURE [Sketcher::SketchObject] Sketch027
  ArcFitTolerance = 1e-06
  AttachmentSupport = -> [Fillet]
  ExternalGeometry = -> [Fillet]
  FullyConstrained = true
  MakeInternals = false
  MapMode = 5
  Placement = pos=(0,-84,0) rot=(1,0,0;1.5708rad)
  sketch-geometry (2):
    g0: Circle CenterX=42 CenterY=14 CenterZ=0 NormalX=0 NormalY=0 NormalZ=1 AngleXU=0 Radius=3.125
    g1: Circle CenterX=42 CenterY=14 CenterZ=0 NormalX=0 NormalY=0 NormalZ=1 AngleXU=0 Radius=3.75
  constraints (4):
    c: Coincident(g0,g-3)
    c: Diameter(g1) = 7.5
    c: Coincident(g1,g0)
    c: Diameter(g0) = 6.25
FEATURE [PartDesign::Pad] Pad015
  BaseFeature = -> Fillet
  Direction = (0,-1,2e-16)
  Length = 8
  Length2 = 10
  Placement = pos=(0,0,0) rot=(1,0,0;1.5708rad)
  Profile = -> Sketch027
  ReferenceAxis = -> Sketch027 [N_Axis]
  Refine = true
  Suppressed = false
  Type = 0
FEATURE [PartDesign::Fillet] Fillet005
  Base = -> Pad015 [Edge70]
  BaseFeature = -> Pad015
  Placement = pos=(0,0,0) rot=(1,0,0;1.5708rad)
  Radius = 2
  Refine = true
  SupportTransform = false
  Suppressed = false
  UseAllEdges = false
FEATURE [Sketcher::SketchObject] Sketch030
  ArcFitTolerance = 1e-06
  AttachmentSupport = -> [Pocket005]
  ExternalGeometry = -> [Pocket005]
  FullyConstrained = true
  MakeInternals = false
  MapMode = 5
  Placement = pos=(7.11416e-08,-84,25.3536) rot=(0,0,1;3.14159rad)
  sketch-geometry (11):
    g0: LineSegment StartX=-84 StartY=0 StartZ=0 EndX=-84 EndY=-84 EndZ=0
    g1: LineSegment StartX=-84 StartY=-84 StartZ=0 EndX=7.11416e-08 EndY=-84 EndZ=0
    g2: LineSegment StartX=7.11416e-08 StartY=-84 StartZ=0 EndX=7.11416e-08 EndY=0 EndZ=0
    g3: LineSegment StartX=7.11416e-08 StartY=0 StartZ=0 EndX=-84 EndY=0 EndZ=0
    g4: Circle CenterX=-79 CenterY=-5 CenterZ=0 NormalX=0 NormalY=0 NormalZ=1 AngleXU=0 Radius=1.35
    g5: Circle CenterX=-79 CenterY=-42 CenterZ=0 NormalX=0 NormalY=0 NormalZ=1 AngleXU=0 Radius=1.35
    g6: Circle CenterX=-79 CenterY=-79 CenterZ=0 NormalX=0 NormalY=0 NormalZ=1 AngleXU=0 Radius=1.35
    g7: Circle CenterX=-41.9965 CenterY=-42 CenterZ=0 NormalX=0 NormalY=0 NormalZ=1 AngleXU=0 Radius=1.55
    g8: Circle CenterX=-5 CenterY=-5 CenterZ=0 NormalX=0 NormalY=0 NormalZ=1 AngleXU=0 Radius=1.35
    g9: Circle CenterX=-5 CenterY=-42 CenterZ=0 NormalX=0 NormalY=0 NormalZ=1 AngleXU=0 Radius=1.35
    g10: Circle CenterX=-5 CenterY=-79 CenterZ=0 NormalX=0 NormalY=0 NormalZ=1 AngleXU=0 Radius=1.35
  constraints (24):
    c: Coincident(g0,g1)
    c: Coincident(g1,g2)
    c: Coincident(g2,g3)
    c: Coincident(g3,g0)
    c: Vertical(g0)
    c: Vertical(g2)
    c: Horizontal(g1)
    c: Horizontal(g3)
    c: Coincident(g0,g-7)
    c: Coincident(g1,g-6)
    c: Coincident(g4,g-3)
    c: Equal(g4,g-3)
    c: Coincident(g5,g-10)
    c: Equal(g5,g-10)
    c: Coincident(g6,g-12)
    c: Equal(g6,g-12)
    c: Coincident(g7,g-9)
    c: Equal(g7,g-9)
    c: Coincident(g8,g-11)
    c: Equal(g8,g-11)
    c: Coincident(g9,g-8)
    c: Equal(g9,g-8)
    c: Coincident(g10,g-13)
    c: Equal(g10,g-13)
FEATURE [PartDesign::Pad] Pad016
  BaseFeature = -> Pocket005
  Direction = (2.80598e-09,0,1)
  Length = 2
  Length2 = 10
  Placement = pos=(0,-84,2e-15) rot=(1,0,0;1.5708rad)
  Profile = -> Sketch030
  ReferenceAxis = -> Sketch030 [N_Axis]
  Refine = true
  Suppressed = false
  Type = 0
FEATURE [Sketcher::SketchObject] Sketch031
  ArcFitTolerance = 1e-06
  AttachmentSupport = -> [Pad016]
  ExternalGeometry = -> [Pad016]
  FullyConstrained = true
  MakeInternals = false
  MapMode = 5
  Placement = pos=(7.67535e-08,-84,27.3536) rot=(0,0,1;3.14159rad)
  sketch-geometry (1):
    g0: Circle CenterX=-41.9965 CenterY=-42 CenterZ=0 NormalX=0 NormalY=0 NormalZ=1 AngleXU=0 Radius=3
  constraints (2):
    c: Diameter(g0) = 6
    c: Coincident(g0,g-3)
FEATURE [PartDesign::Pocket] Pocket011
  BaseFeature = -> Pad016
  Direction = (-2.80598e-09,0,-1)
  Length = 4
  Length2 = 5
  Placement = pos=(0,-84,2e-15) rot=(1,0,0;1.5708rad)
  Profile = -> Sketch031
  ReferenceAxis = -> Sketch031 [N_Axis]
  Refine = true
  Suppressed = false
  Type = 0
FEATURE [PartDesign::ShapeBinder] CopyPocket011
  Placement = pos=(0,-84,2e-15) rot=(1,0,0;1.5708rad)
  TraceSupport = false
FEATURE [PartDesign::Plane] DatumPlane010
  AttachmentSupport = -> [CopyPocket011]
  Length = 130.8
  MapMode = 5
  Placement = pos=(7.67535e-08,-84,27.3536) rot=(0,0,1;3.14159rad)
  ResizeMode = 0
  Width = 130.8
FEATURE [Sketcher::SketchObject] Sketch032
  ArcFitTolerance = 1e-06
  AttachmentSupport = -> [DatumPlane010]
  ExternalGeometry = -> [CopyPocket011]
  FullyConstrained = true
  MakeInternals = false
  MapMode = 5
  Placement = pos=(7.67535e-08,-84,27.3536) rot=(0,0,1;3.14159rad)
  sketch-geometry (10):
    g0: Circle CenterX=-79 CenterY=-42 CenterZ=0 NormalX=0 NormalY=0 NormalZ=1 AngleXU=0 Radius=3
    g1: Circle CenterX=-5 CenterY=-42 CenterZ=0 NormalX=0 NormalY=0 NormalZ=1 AngleXU=0 Radius=3
    g2: LineSegment StartX=-84 StartY=0 StartZ=0 EndX=-84 EndY=-84 EndZ=0
    g3: LineSegment StartX=-84 StartY=-84 StartZ=0 EndX=7.11416e-08 EndY=-84 EndZ=0
    g4: LineSegment StartX=7.11416e-08 StartY=-84 StartZ=0 EndX=7.11416e-08 EndY=0 EndZ=0
    g5: LineSegment StartX=7.11416e-08 StartY=0 StartZ=0 EndX=-84 EndY=0 EndZ=0
    g6: Circle CenterX=-79 CenterY=-5 CenterZ=0 NormalX=0 NormalY=0 NormalZ=1 AngleXU=0 Radius=1.6
    g7: Circle CenterX=-79 CenterY=-79 CenterZ=0 NormalX=0 NormalY=0 NormalZ=1 AngleXU=0 Radius=1.6
    g8: Circle CenterX=-5 CenterY=-5 CenterZ=0 NormalX=0 NormalY=0 NormalZ=1 AngleXU=0 Radius=1.6
    g9: Circle CenterX=-5 CenterY=-79 CenterZ=0 NormalX=0 NormalY=0 NormalZ=1 AngleXU=0 Radius=1.6
  constraints (22):
    c: Diameter(g0) = 6
    c: Coincident(g0,g-8)
    c: Diameter(g1) = 6
    c: Coincident(g1,g-10)
    c: Coincident(g2,g3)
    c: Coincident(g3,g4)
    c: Coincident(g4,g5)
    c: Coincident(g5,g2)
    c: Vertical(g2)
    c: Vertical(g4)
    c: Horizontal(g3)
    c: Horizontal(g5)
    c: Coincident(g2,g-4)
    c: Coincident(g3,g-6)
    c: Diameter(g6) = 3.2
    c: Coincident(g6,g-9)
    c: Coincident(g7,g-7)
    c: Diameter(g7) = 3.2
    c: Coincident(g8,g-12)
    c: Coincident(g9,g-11)
    c: Diameter(g9) = 3.2
    c: Diameter(g8) = 3.2
FEATURE [PartDesign::Pad] Pad017
  Direction = (2.80598e-09,0,1)
  Length = 4
  Length2 = 10
  Placement = pos=(7.67535e-08,-84,27.3536) rot=(0,0,1;3.14159rad)
  Profile = -> Sketch032
  ReferenceAxis = -> Sketch032 [N_Axis]
  Refine = true
  Suppressed = false
  Type = 0
FEATURE [Sketcher::SketchObject] Sketch033
  ArcFitTolerance = 1e-06
  AttachmentSupport = -> [Pad017]
  ExternalGeometry = -> [Pad017]
  FullyConstrained = true
  MakeInternals = false
  MapMode = 5
  Placement = pos=(8.79774e-08,-84,31.3536) rot=(0,0,1;3.14159rad)
  sketch-geometry (10):
    g0: Circle CenterX=-79 CenterY=-42 CenterZ=0 NormalX=0 NormalY=0 NormalZ=1 AngleXU=0 Radius=3
    g1: Circle CenterX=-5 CenterY=-42 CenterZ=0 NormalX=0 NormalY=0 NormalZ=1 AngleXU=0 Radius=3
    g2: Circle CenterX=-5 CenterY=-5 CenterZ=0 NormalX=0 NormalY=0 NormalZ=1 AngleXU=0 Radius=3
    g3: Circle CenterX=-5 CenterY=-79 CenterZ=0 NormalX=0 NormalY=0 NormalZ=1 AngleXU=0 Radius=3
    g4: Circle CenterX=-79 CenterY=-79 CenterZ=0 NormalX=0 NormalY=0 NormalZ=1 AngleXU=0 Radius=3
    g5: Circle CenterX=-79 CenterY=-5 CenterZ=0 NormalX=0 NormalY=0 NormalZ=1 AngleXU=0 Radius=3
    g6: LineSegment StartX=-84 StartY=0 StartZ=0 EndX=-84 EndY=-84 EndZ=0
    g7: LineSegment StartX=-84 StartY=-84 StartZ=0 EndX=7.11416e-08 EndY=-84 EndZ=0
    g8: LineSegment StartX=7.11416e-08 StartY=-84 StartZ=0 EndX=7.11416e-08 EndY=0 EndZ=0
    g9: LineSegment StartX=7.11416e-08 StartY=0 StartZ=0 EndX=-84 EndY=0 EndZ=0
  constraints (22):
    c: Coincident(g0,g-8)
    c: Equal(g0,g-8)
    c: Coincident(g1,g-11)
    c: Equal(g1,g-11)
    c: Diameter(g2) = 6
    c: Coincident(g2,g-10)
    c: Diameter(g3) = 6
    c: Coincident(g3,g-12)
    c: Diameter(g4) = 6
    c: Coincident(g4,g-7)
    c: Diameter(g5) = 6
    c: Coincident(g5,g-9)
    c: Coincident(g6,g7)
    c: Coincident(g7,g8)
    c: Coincident(g8,g9)
    c: Coincident(g9,g6)
    c: Vertical(g6)
    c: Vertical(g8)
    c: Horizontal(g7)
    c: Horizontal(g9)
    c: Coincident(g6,g-4)
    c: Coincident(g7,g-6)
FEATURE [PartDesign::Pad] Pad018
  BaseFeature = -> Pad017
  Direction = (2.80598e-09,0,1)
  Length = 3.5
  Length2 = 10
  Placement = pos=(7.67535e-08,-84,27.3536) rot=(0,0,1;3.14159rad)
  Profile = -> Sketch033
  ReferenceAxis = -> Sketch033 [N_Axis]
  Refine = true
  Suppressed = false
  Type = 0
FEATURE [Sketcher::SketchObject] Sketch034
  ArcFitTolerance = 1e-06
  AttachmentSupport = -> [Pad018]
  ExternalGeometry = -> [Pad018]
  FullyConstrained = false
  MakeInternals = false
  MapMode = 5
  Placement = pos=(9.77984e-08,-84,34.8536) rot=(0,0,1;3.14159rad)
  sketch-geometry (212):
    g0: LineSegment [constr] StartX=-42 StartY=-7.1e-15 StartZ=0 EndX=-42 EndY=-84 EndZ=0
    g1: GeomPoint X=-42 Y=-42 Z=0
    g2: Circle CenterX=-42 CenterY=-42 CenterZ=0 NormalX=0 NormalY=0 NormalZ=1 AngleXU=0 Radius=1.3
    g3: Circle CenterX=-37 CenterY=-42 CenterZ=0 NormalX=0 NormalY=0 NormalZ=1 AngleXU=0 Radius=1.3
    g4: Circle CenterX=-32 CenterY=-42 CenterZ=0 NormalX=0 NormalY=0 NormalZ=1 AngleXU=0 Radius=1.3
    g5: Circle CenterX=-27 CenterY=-42 CenterZ=0 NormalX=0 NormalY=0 NormalZ=1 AngleXU=0 Radius=1.3
    g6: Circle CenterX=-22 CenterY=-42 CenterZ=0 NormalX=0 NormalY=0 NormalZ=1 AngleXU=0 Radius=1.3
    g7: Circle CenterX=-17 CenterY=-42 CenterZ=0 NormalX=0 NormalY=0 NormalZ=1 AngleXU=0 Radius=1.3
    g8: Circle CenterX=-12 CenterY=-42 CenterZ=0 NormalX=0 NormalY=0 NormalZ=1 AngleXU=0 Radius=1.3
    g9: GeomPoint X=-42 Y=-37 Z=0
    g10: Circle CenterX=-42 CenterY=-37 CenterZ=0 NormalX=0 NormalY=0 NormalZ=1 AngleXU=0 Radius=1.3
    g11: Circle CenterX=-37 CenterY=-37 CenterZ=0 NormalX=0 NormalY=0 NormalZ=1 AngleXU=0 Radius=1.3
    g12: Circle CenterX=-32 CenterY=-37 CenterZ=0 NormalX=0 NormalY=0 NormalZ=1 AngleXU=0 Radius=1.3
    g13: Circle CenterX=-27 CenterY=-37 CenterZ=0 NormalX=0 NormalY=0 NormalZ=1 AngleXU=0 Radius=1.3
    g14: Circle CenterX=-22 CenterY=-37 CenterZ=0 NormalX=0 NormalY=0 NormalZ=1 AngleXU=0 Radius=1.3
    g15: Circle CenterX=-17 CenterY=-37 CenterZ=0 NormalX=0 NormalY=0 NormalZ=1 AngleXU=0 Radius=1.3
    g16: Circle CenterX=-12 CenterY=-37 CenterZ=0 NormalX=0 NormalY=0 NormalZ=1 AngleXU=0 Radius=1.3
    g17: GeomPoint X=-42 Y=-32 Z=0
    g18: Circle CenterX=-42 CenterY=-32 CenterZ=0 NormalX=0 NormalY=0 NormalZ=1 AngleXU=0 Radius=1.3
    g19: Circle CenterX=-37 CenterY=-32 CenterZ=0 NormalX=0 NormalY=0 NormalZ=1 AngleXU=0 Radius=1.3
    g20: Circle CenterX=-32 CenterY=-32 CenterZ=0 NormalX=0 NormalY=0 NormalZ=1 AngleXU=0 Radius=1.3
    g21: Circle CenterX=-27 CenterY=-32 CenterZ=0 NormalX=0 NormalY=0 NormalZ=1 AngleXU=0 Radius=1.3
    g22: Circle CenterX=-22 CenterY=-32 CenterZ=0 NormalX=0 NormalY=0 NormalZ=1 AngleXU=0 Radius=1.3
    g23: Circle CenterX=-17 CenterY=-32 CenterZ=0 NormalX=0 NormalY=0 NormalZ=1 AngleXU=0 Radius=1.3
    g24: Circle CenterX=-12 CenterY=-32 CenterZ=0 NormalX=0 NormalY=0 NormalZ=1 AngleXU=0 Radius=1.3
    g25: GeomPoint X=-42 Y=-27 Z=0
    g26: Circle CenterX=-42 CenterY=-27 CenterZ=0 NormalX=0 NormalY=0 NormalZ=1 AngleXU=0 Radius=1.3
    g27: Circle CenterX=-37 CenterY=-27 CenterZ=0 NormalX=0 NormalY=0 NormalZ=1 AngleXU=0 Radius=1.3
    g28: Circle CenterX=-32 CenterY=-27 CenterZ=0 NormalX=0 NormalY=0 NormalZ=1 AngleXU=0 Radius=1.3
    g29: Circle CenterX=-27 CenterY=-27 CenterZ=0 NormalX=0 NormalY=0 NormalZ=1 AngleXU=0 Radius=1.3
    g30: Circle CenterX=-22 CenterY=-27 CenterZ=0 NormalX=0 NormalY=0 NormalZ=1 AngleXU=0 Radius=1.3
    g31: Circle CenterX=-17 CenterY=-27 CenterZ=0 NormalX=0 NormalY=0 NormalZ=1 AngleXU=0 Radius=1.3
    g32: Circle CenterX=-12 CenterY=-27 CenterZ=0 NormalX=0 NormalY=0 NormalZ=1 AngleXU=0 Radius=1.3
    g33: GeomPoint X=-42 Y=-22 Z=0
    g34: Circle CenterX=-42 CenterY=-22 CenterZ=0 NormalX=0 NormalY=0 NormalZ=1 AngleXU=0 Radius=1.3
    g35: Circle CenterX=-37 CenterY=-22 CenterZ=0 NormalX=0 NormalY=0 NormalZ=1 AngleXU=0 Radius=1.3
    g36: Circle CenterX=-32 CenterY=-22 CenterZ=0 NormalX=0 NormalY=0 NormalZ=1 AngleXU=0 Radius=1.3
    g37: Circle CenterX=-27 CenterY=-22 CenterZ=0 NormalX=0 NormalY=0 NormalZ=1 AngleXU=0 Radius=1.3
    g38: Circle CenterX=-22 CenterY=-22 CenterZ=0 NormalX=0 NormalY=0 NormalZ=1 AngleXU=0 Radius=1.3
    g39: Circle CenterX=-17 CenterY=-22 CenterZ=0 NormalX=0 NormalY=0 NormalZ=1 AngleXU=0 Radius=1.3
    g40: Circle CenterX=-12 CenterY=-22 CenterZ=0 NormalX=0 NormalY=0 NormalZ=1 AngleXU=0 Radius=1.3
    g41: GeomPoint X=-42 Y=-17 Z=0
    g42: Circle CenterX=-42 CenterY=-17 CenterZ=0 NormalX=0 NormalY=0 NormalZ=1 AngleXU=0 Radius=1.3
    g43: Circle CenterX=-37 CenterY=-17 CenterZ=0 NormalX=0 NormalY=0 NormalZ=1 AngleXU=0 Radius=1.3
    g44: Circle CenterX=-32 CenterY=-17 CenterZ=0 NormalX=0 NormalY=0 NormalZ=1 AngleXU=0 Radius=1.3
    g45: Circle CenterX=-27 CenterY=-17 CenterZ=0 NormalX=0 NormalY=0 NormalZ=1 AngleXU=0 Radius=1.3
    g46: Circle CenterX=-22 CenterY=-17 CenterZ=0 NormalX=0 NormalY=0 NormalZ=1 AngleXU=0 Radius=1.3
    g47: Circle CenterX=-17 CenterY=-17 CenterZ=0 NormalX=0 NormalY=0 NormalZ=1 AngleXU=0 Radius=1.3
    g48: Circle CenterX=-12 CenterY=-17 CenterZ=0 NormalX=0 NormalY=0 NormalZ=1 AngleXU=0 Radius=1.3
    g49: GeomPoint X=-42 Y=-12 Z=0
    g50: Circle CenterX=-42 CenterY=-12 CenterZ=0 NormalX=0 NormalY=0 NormalZ=1 AngleXU=0 Radius=1.3
    g51: Circle CenterX=-37 CenterY=-12 CenterZ=0 NormalX=0 NormalY=0 NormalZ=1 AngleXU=0 Radius=1.3
    g52: Circle CenterX=-32 CenterY=-12 CenterZ=0 NormalX=0 NormalY=0 NormalZ=1 AngleXU=0 Radius=1.3
    g53: Circle CenterX=-27 CenterY=-12 CenterZ=0 NormalX=0 NormalY=0 NormalZ=1 AngleXU=0 Radius=1.3
    g54: Circle CenterX=-22 CenterY=-12 CenterZ=0 NormalX=0 NormalY=0 NormalZ=1 AngleXU=0 Radius=1.3
    g55: Circle CenterX=-17 CenterY=-12 CenterZ=0 NormalX=0 NormalY=0 NormalZ=1 AngleXU=0 Radius=1.3
    g56: Circle CenterX=-12 CenterY=-12 CenterZ=0 NormalX=0 NormalY=0 NormalZ=1 AngleXU=0 Radius=1.3
    g57: GeomPoint X=-42 Y=-7 Z=0
    g58: Circle CenterX=-42 CenterY=-7 CenterZ=0 NormalX=0 NormalY=0 NormalZ=1 AngleXU=0 Radius=1.3
    g59: Circle CenterX=-37 CenterY=-7 CenterZ=0 NormalX=0 NormalY=0 NormalZ=1 AngleXU=0 Radius=1.3
    g60: Circle CenterX=-32 CenterY=-7 CenterZ=0 NormalX=0 NormalY=0 NormalZ=1 AngleXU=0 Radius=1.3
    g61: Circle CenterX=-27 CenterY=-7 CenterZ=0 NormalX=0 NormalY=0 NormalZ=1 AngleXU=0 Radius=1.3
    g62: Circle CenterX=-22 CenterY=-7 CenterZ=0 NormalX=0 NormalY=0 NormalZ=1 AngleXU=0 Radius=1.3
    g63: Circle CenterX=-17 CenterY=-7 CenterZ=0 NormalX=0 NormalY=0 NormalZ=1 AngleXU=0 Radius=1.3
    g64: Circle CenterX=-12 CenterY=-7 CenterZ=0 NormalX=0 NormalY=0 NormalZ=1 AngleXU=0 Radius=1.3
    g65: LineSegment [constr] StartX=-84 StartY=-42 StartZ=0 EndX=7.11416e-08 EndY=-42 EndZ=0
    g66: Circle CenterX=-47 CenterY=-42 CenterZ=0 NormalX=0 NormalY=0 NormalZ=1 AngleXU=0 Radius=1.3
    g67: Circle CenterX=-52 CenterY=-42 CenterZ=0 NormalX=0 NormalY=0 NormalZ=1 AngleXU=0 Radius=1.3
    g68: Circle CenterX=-57 CenterY=-42 CenterZ=0 NormalX=0 NormalY=0 NormalZ=1 AngleXU=0 Radius=1.3
    g69: Circle CenterX=-62 CenterY=-42 CenterZ=0 NormalX=0 NormalY=0 NormalZ=1 AngleXU=0 Radius=1.3
    g70: Circle CenterX=-67 CenterY=-42 CenterZ=0 NormalX=0 NormalY=0 NormalZ=1 AngleXU=0 Radius=1.3
    g71: Circle CenterX=-72 CenterY=-42 CenterZ=0 NormalX=0 NormalY=0 NormalZ=1 AngleXU=0 Radius=1.3
    g72: Circle CenterX=-47 CenterY=-37 CenterZ=0 NormalX=0 NormalY=0 NormalZ=1 AngleXU=0 Radius=1.3
    g73: Circle CenterX=-52 CenterY=-37 CenterZ=0 NormalX=0 NormalY=0 NormalZ=1 AngleXU=0 Radius=1.3
    g74: Circle CenterX=-57 CenterY=-37 CenterZ=0 NormalX=0 NormalY=0 NormalZ=1 AngleXU=0 Radius=1.3
    g75: Circle CenterX=-62 CenterY=-37 CenterZ=0 NormalX=0 NormalY=0 NormalZ=1 AngleXU=0 Radius=1.3
    g76: Circle CenterX=-67 CenterY=-37 CenterZ=0 NormalX=0 NormalY=0 NormalZ=1 AngleXU=0 Radius=1.3
    g77: Circle CenterX=-72 CenterY=-37 CenterZ=0 NormalX=0 NormalY=0 NormalZ=1 AngleXU=0 Radius=1.3
    g78: Circle CenterX=-47 CenterY=-32 CenterZ=0 NormalX=0 NormalY=0 NormalZ=1 AngleXU=0 Radius=1.3
    g79: Circle CenterX=-52 CenterY=-32 CenterZ=0 NormalX=0 NormalY=0 NormalZ=1 AngleXU=0 Radius=1.3
    g80: Circle CenterX=-57 CenterY=-32 CenterZ=0 NormalX=0 NormalY=0 NormalZ=1 AngleXU=0 Radius=1.3
    g81: Circle CenterX=-62 CenterY=-32 CenterZ=0 NormalX=0 NormalY=0 NormalZ=1 AngleXU=0 Radius=1.3
    g82: Circle CenterX=-67 CenterY=-32 CenterZ=0 NormalX=0 NormalY=0 NormalZ=1 AngleXU=0 Radius=1.3
    g83: Circle CenterX=-72 CenterY=-32 CenterZ=0 NormalX=0 NormalY=0 NormalZ=1 AngleXU=0 Radius=1.3
    g84: Circle CenterX=-47 CenterY=-27 CenterZ=0 NormalX=0 NormalY=0 NormalZ=1 AngleXU=0 Radius=1.3
    g85: Circle CenterX=-52 CenterY=-27 CenterZ=0 NormalX=0 NormalY=0 NormalZ=1 AngleXU=0 Radius=1.3
    g86: Circle CenterX=-57 CenterY=-27 CenterZ=0 NormalX=0 NormalY=0 NormalZ=1 AngleXU=0 Radius=1.3
    g87: Circle CenterX=-62 CenterY=-27 CenterZ=0 NormalX=0 NormalY=0 NormalZ=1 AngleXU=0 Radius=1.3
    g88: Circle CenterX=-67 CenterY=-27 CenterZ=0 NormalX=0 NormalY=0 NormalZ=1 AngleXU=0 Radius=1.3
    g89: Circle CenterX=-72 CenterY=-27 CenterZ=0 NormalX=0 NormalY=0 NormalZ=1 AngleXU=0 Radius=1.3
    g90: Circle CenterX=-47 CenterY=-22 CenterZ=0 NormalX=0 NormalY=0 NormalZ=1 AngleXU=0 Radius=1.3
    g91: Circle CenterX=-52 CenterY=-22 CenterZ=0 NormalX=0 NormalY=0 NormalZ=1 AngleXU=0 Radius=1.3
    g92: Circle CenterX=-57 CenterY=-22 CenterZ=0 NormalX=0 NormalY=0 NormalZ=1 AngleXU=0 Radius=1.3
    g93: Circle CenterX=-62 CenterY=-22 CenterZ=0 NormalX=0 NormalY=0 NormalZ=1 AngleXU=0 Radius=1.3
    g94: Circle CenterX=-67 CenterY=-22 CenterZ=0 NormalX=0 NormalY=0 NormalZ=1 AngleXU=0 Radius=1.3
    g95: Circle CenterX=-72 CenterY=-22 CenterZ=0 NormalX=0 NormalY=0 NormalZ=1 AngleXU=0 Radius=1.3
    g96: Circle CenterX=-47 CenterY=-17 CenterZ=0 NormalX=0 NormalY=0 NormalZ=1 AngleXU=0 Radius=1.3
    g97: Circle CenterX=-52 CenterY=-17 CenterZ=0 NormalX=0 NormalY=0 NormalZ=1 AngleXU=0 Radius=1.3
    g98: Circle CenterX=-57 CenterY=-17 CenterZ=0 NormalX=0 NormalY=0 NormalZ=1 AngleXU=0 Radius=1.3
    g99: Circle CenterX=-62 CenterY=-17 CenterZ=0 NormalX=0 NormalY=0 NormalZ=1 AngleXU=0 Radius=1.3
    g100: Circle CenterX=-67 CenterY=-17 CenterZ=0 NormalX=0 NormalY=0 NormalZ=1 AngleXU=0 Radius=1.3
    g101: Circle CenterX=-72 CenterY=-17 CenterZ=0 NormalX=0 NormalY=0 NormalZ=1 AngleXU=0 Radius=1.3
    g102: Circle CenterX=-47 CenterY=-12 CenterZ=0 NormalX=0 NormalY=0 NormalZ=1 AngleXU=0 Radius=1.3
    g103: Circle CenterX=-52 CenterY=-12 CenterZ=0 NormalX=0 NormalY=0 NormalZ=1 AngleXU=0 Radius=1.3
    g104: Circle CenterX=-57 CenterY=-12 CenterZ=0 NormalX=0 NormalY=0 NormalZ=1 AngleXU=0 Radius=1.3
    g105: Circle CenterX=-62 CenterY=-12 CenterZ=0 NormalX=0 NormalY=0 NormalZ=1 AngleXU=0 Radius=1.3
    g106: Circle CenterX=-67 CenterY=-12 CenterZ=0 NormalX=0 NormalY=0 NormalZ=1 AngleXU=0 Radius=1.3
    g107: Circle CenterX=-72 CenterY=-12 CenterZ=0 NormalX=0 NormalY=0 NormalZ=1 AngleXU=0 Radius=1.3
    g108: Circle CenterX=-47 CenterY=-7 CenterZ=0 NormalX=0 NormalY=0 NormalZ=1 AngleXU=0 Radius=1.3
    g109: Circle CenterX=-52 CenterY=-7 CenterZ=0 NormalX=0 NormalY=0 NormalZ=1 AngleXU=0 Radius=1.3
    g110: Circle CenterX=-57 CenterY=-7 CenterZ=0 NormalX=0 NormalY=0 NormalZ=1 AngleXU=0 Radius=1.3
    g111: Circle CenterX=-62 CenterY=-7 CenterZ=0 NormalX=0 NormalY=0 NormalZ=1 AngleXU=0 Radius=1.3
    g112: Circle CenterX=-67 CenterY=-7 CenterZ=0 NormalX=0 NormalY=0 NormalZ=1 AngleXU=0 Radius=1.3
    g113: Circle CenterX=-72 CenterY=-7 CenterZ=0 NormalX=0 NormalY=0 NormalZ=1 AngleXU=0 Radius=1.3
    g114: GeomPoint X=-42 Y=-47 Z=0
    g115: Circle CenterX=-42 CenterY=-47 CenterZ=0 NormalX=0 NormalY=0 NormalZ=1 AngleXU=0 Radius=1.3
    g116: Circle CenterX=-37 CenterY=-47 CenterZ=0 NormalX=0 NormalY=0 NormalZ=1 AngleXU=0 Radius=1.3
    g117: Circle CenterX=-32 CenterY=-47 CenterZ=0 NormalX=0 NormalY=0 NormalZ=1 AngleXU=0 Radius=1.3
    g118: Circle CenterX=-27 CenterY=-47 CenterZ=0 NormalX=0 NormalY=0 NormalZ=1 AngleXU=0 Radius=1.3
    g119: Circle CenterX=-22 CenterY=-47 CenterZ=0 NormalX=0 NormalY=0 NormalZ=1 AngleXU=0 Radius=1.3
    g120: Circle CenterX=-17 CenterY=-47 CenterZ=0 NormalX=0 NormalY=0 NormalZ=1 AngleXU=0 Radius=1.3
    g121: Circle CenterX=-12 CenterY=-47 CenterZ=0 NormalX=0 NormalY=0 NormalZ=1 AngleXU=0 Radius=1.3
    g122: GeomPoint X=-42 Y=-52 Z=0
    g123: Circle CenterX=-42 CenterY=-52 CenterZ=0 NormalX=0 NormalY=0 NormalZ=1 AngleXU=0 Radius=1.3
    g124: Circle CenterX=-37 CenterY=-52 CenterZ=0 NormalX=0 NormalY=0 NormalZ=1 AngleXU=0 Radius=1.3
    g125: Circle CenterX=-32 CenterY=-52 CenterZ=0 NormalX=0 NormalY=0 NormalZ=1 AngleXU=0 Radius=1.3
    g126: Circle CenterX=-27 CenterY=-52 CenterZ=0 NormalX=0 NormalY=0 NormalZ=1 AngleXU=0 Radius=1.3
    g127: Circle CenterX=-22 CenterY=-52 CenterZ=0 NormalX=0 NormalY=0 NormalZ=1 AngleXU=0 Radius=1.3
    g128: Circle CenterX=-17 CenterY=-52 CenterZ=0 NormalX=0 NormalY=0 NormalZ=1 AngleXU=0 Radius=1.3
    g129: Circle CenterX=-12 CenterY=-52 CenterZ=0 NormalX=0 NormalY=0 NormalZ=1 AngleXU=0 Radius=1.3
    g130: GeomPoint X=-42 Y=-57 Z=0
    g131: Circle CenterX=-42 CenterY=-57 CenterZ=0 NormalX=0 NormalY=0 NormalZ=1 AngleXU=0 Radius=1.3
    g132: Circle CenterX=-37 CenterY=-57 CenterZ=0 NormalX=0 NormalY=0 NormalZ=1 AngleXU=0 Radius=1.3
    g133: Circle CenterX=-32 CenterY=-57 CenterZ=0 NormalX=0 NormalY=0 NormalZ=1 AngleXU=0 Radius=1.3
    g134: Circle CenterX=-27 CenterY=-57 CenterZ=0 NormalX=0 NormalY=0 NormalZ=1 AngleXU=0 Radius=1.3
    g135: Circle CenterX=-22 CenterY=-57 CenterZ=0 NormalX=0 NormalY=0 NormalZ=1 AngleXU=0 Radius=1.3
    g136: Circle CenterX=-17 CenterY=-57 CenterZ=0 NormalX=0 NormalY=0 NormalZ=1 AngleXU=0 Radius=1.3
    g137: Circle CenterX=-12 CenterY=-57 CenterZ=0 NormalX=0 NormalY=0 NormalZ=1 AngleXU=0 Radius=1.3
    g138: GeomPoint X=-42 Y=-62 Z=0
    g139: Circle CenterX=-42 CenterY=-62 CenterZ=0 NormalX=0 NormalY=0 NormalZ=1 AngleXU=0 Radius=1.3
    g140: Circle CenterX=-37 CenterY=-62 CenterZ=0 NormalX=0 NormalY=0 NormalZ=1 AngleXU=0 Radius=1.3
    g141: Circle CenterX=-32 CenterY=-62 CenterZ=0 NormalX=0 NormalY=0 NormalZ=1 AngleXU=0 Radius=1.3
    g142: Circle CenterX=-27 CenterY=-62 CenterZ=0 NormalX=0 NormalY=0 NormalZ=1 AngleXU=0 Radius=1.3
    g143: Circle CenterX=-22 CenterY=-62 CenterZ=0 NormalX=0 NormalY=0 NormalZ=1 AngleXU=0 Radius=1.3
    g144: Circle CenterX=-17 CenterY=-62 CenterZ=0 NormalX=0 NormalY=0 NormalZ=1 AngleXU=0 Radius=1.3
    g145: Circle CenterX=-12 CenterY=-62 CenterZ=0 NormalX=0 NormalY=0 NormalZ=1 AngleXU=0 Radius=1.3
    g146: GeomPoint X=-42 Y=-67 Z=0
    g147: Circle CenterX=-42 CenterY=-67 CenterZ=0 NormalX=0 NormalY=0 NormalZ=1 AngleXU=0 Radius=1.3
    g148: Circle CenterX=-37 CenterY=-67 CenterZ=0 NormalX=0 NormalY=0 NormalZ=1 AngleXU=0 Radius=1.3
    g149: Circle CenterX=-32 CenterY=-67 CenterZ=0 NormalX=0 NormalY=0 NormalZ=1 AngleXU=0 Radius=1.3
    g150: Circle CenterX=-27 CenterY=-67 CenterZ=0 NormalX=0 NormalY=0 NormalZ=1 AngleXU=0 Radius=1.3
    g151: Circle CenterX=-22 CenterY=-67 CenterZ=0 NormalX=0 NormalY=0 NormalZ=1 AngleXU=0 Radius=1.3
    g152: Circle CenterX=-17 CenterY=-67 CenterZ=0 NormalX=0 NormalY=0 NormalZ=1 AngleXU=0 Radius=1.3
    g153: Circle CenterX=-12 CenterY=-67 CenterZ=0 NormalX=0 NormalY=0 NormalZ=1 AngleXU=0 Radius=1.3
    g154: GeomPoint X=-42 Y=-72 Z=0
    g155: Circle CenterX=-42 CenterY=-72 CenterZ=0 NormalX=0 NormalY=0 NormalZ=1 AngleXU=0 Radius=1.3
    g156: Circle CenterX=-37 CenterY=-72 CenterZ=0 NormalX=0 NormalY=0 NormalZ=1 AngleXU=0 Radius=1.3
    g157: Circle CenterX=-32 CenterY=-72 CenterZ=0 NormalX=0 NormalY=0 NormalZ=1 AngleXU=0 Radius=1.3
    g158: Circle CenterX=-27 CenterY=-72 CenterZ=0 NormalX=0 NormalY=0 NormalZ=1 AngleXU=0 Radius=1.3
    g159: Circle CenterX=-22 CenterY=-72 CenterZ=0 NormalX=0 NormalY=0 NormalZ=1 AngleXU=0 Radius=1.3
    g160: Circle CenterX=-17 CenterY=-72 CenterZ=0 NormalX=0 NormalY=0 NormalZ=1 AngleXU=0 Radius=1.3
    g161: Circle CenterX=-12 CenterY=-72 CenterZ=0 NormalX=0 NormalY=0 NormalZ=1 AngleXU=0 Radius=1.3
    g162: GeomPoint X=-42 Y=-77 Z=0
    g163: Circle CenterX=-42 CenterY=-77 CenterZ=0 NormalX=0 NormalY=0 NormalZ=1 AngleXU=0 Radius=1.3
    g164: Circle CenterX=-37 CenterY=-77 CenterZ=0 NormalX=0 NormalY=0 NormalZ=1 AngleXU=0 Radius=1.3
    g165: Circle CenterX=-32 CenterY=-77 CenterZ=0 NormalX=0 NormalY=0 NormalZ=1 AngleXU=0 Radius=1.3
    g166: Circle CenterX=-27 CenterY=-77 CenterZ=0 NormalX=0 NormalY=0 NormalZ=1 AngleXU=0 Radius=1.3
    g167: Circle CenterX=-22 CenterY=-77 CenterZ=0 NormalX=0 NormalY=0 NormalZ=1 AngleXU=0 Radius=1.3
    g168: Circle CenterX=-17 CenterY=-77 CenterZ=0 NormalX=0 NormalY=0 NormalZ=1 AngleXU=0 Radius=1.3
    g169: Circle CenterX=-12 CenterY=-77 CenterZ=0 NormalX=0 NormalY=0 NormalZ=1 AngleXU=0 Radius=1.3
    g170: Circle CenterX=-47 CenterY=-47 CenterZ=0 NormalX=0 NormalY=0 NormalZ=1 AngleXU=0 Radius=1.3
    g171: Circle CenterX=-52 CenterY=-47 CenterZ=0 NormalX=0 NormalY=0 NormalZ=1 AngleXU=0 Radius=1.3
    g172: Circle CenterX=-57 CenterY=-47 CenterZ=0 NormalX=0 NormalY=0 NormalZ=1 AngleXU=0 Radius=1.3
    g173: Circle CenterX=-62 CenterY=-47 CenterZ=0 NormalX=0 NormalY=0 NormalZ=1 AngleXU=0 Radius=1.3
    g174: Circle CenterX=-67 CenterY=-47 CenterZ=0 NormalX=0 NormalY=0 NormalZ=1 AngleXU=0 Radius=1.3
    g175: Circle CenterX=-72 CenterY=-47 CenterZ=0 NormalX=0 NormalY=0 NormalZ=1 AngleXU=0 Radius=1.3
    g176: Circle CenterX=-47 CenterY=-52 CenterZ=0 NormalX=0 NormalY=0 NormalZ=1 AngleXU=0 Radius=1.3
    g177: Circle CenterX=-52 CenterY=-52 CenterZ=0 NormalX=0 NormalY=0 NormalZ=1 AngleXU=0 Radius=1.3
    g178: Circle CenterX=-57 CenterY=-52 CenterZ=0 NormalX=0 NormalY=0 NormalZ=1 AngleXU=0 Radius=1.3
    g179: Circle CenterX=-62 CenterY=-52 CenterZ=0 NormalX=0 NormalY=0 NormalZ=1 AngleXU=0 Radius=1.3
    g180: Circle CenterX=-67 CenterY=-52 CenterZ=0 NormalX=0 NormalY=0 NormalZ=1 AngleXU=0 Radius=1.3
    g181: Circle CenterX=-72 CenterY=-52 CenterZ=0 NormalX=0 NormalY=0 NormalZ=1 AngleXU=0 Radius=1.3
    g182: Circle CenterX=-47 CenterY=-57 CenterZ=0 NormalX=0 NormalY=0 NormalZ=1 AngleXU=0 Radius=1.3
    g183: Circle CenterX=-52 CenterY=-57 CenterZ=0 NormalX=0 NormalY=0 NormalZ=1 AngleXU=0 Radius=1.3
    g184: Circle CenterX=-57 CenterY=-57 CenterZ=0 NormalX=0 NormalY=0 NormalZ=1 AngleXU=0 Radius=1.3
    g185: Circle CenterX=-62 CenterY=-57 CenterZ=0 NormalX=0 NormalY=0 NormalZ=1 AngleXU=0 Radius=1.3
    g186: Circle CenterX=-67 CenterY=-57 CenterZ=0 NormalX=0 NormalY=0 NormalZ=1 AngleXU=0 Radius=1.3
    g187: Circle CenterX=-72 CenterY=-57 CenterZ=0 NormalX=0 NormalY=0 NormalZ=1 AngleXU=0 Radius=1.3
    g188: Circle CenterX=-47 CenterY=-62 CenterZ=0 NormalX=0 NormalY=0 NormalZ=1 AngleXU=0 Radius=1.3
    g189: Circle CenterX=-52 CenterY=-62 CenterZ=0 NormalX=0 NormalY=0 NormalZ=1 AngleXU=0 Radius=1.3
    g190: Circle CenterX=-57 CenterY=-62 CenterZ=0 NormalX=0 NormalY=0 NormalZ=1 AngleXU=0 Radius=1.3
    g191: Circle CenterX=-62 CenterY=-62 CenterZ=0 NormalX=0 NormalY=0 NormalZ=1 AngleXU=0 Radius=1.3
    g192: Circle CenterX=-67 CenterY=-62 CenterZ=0 NormalX=0 NormalY=0 NormalZ=1 AngleXU=0 Radius=1.3
    g193: Circle CenterX=-72 CenterY=-62 CenterZ=0 NormalX=0 NormalY=0 NormalZ=1 AngleXU=0 Radius=1.3
    g194: Circle CenterX=-47 CenterY=-67 CenterZ=0 NormalX=0 NormalY=0 NormalZ=1 AngleXU=0 Radius=1.3
    g195: Circle CenterX=-52 CenterY=-67 CenterZ=0 NormalX=0 NormalY=0 NormalZ=1 AngleXU=0 Radius=1.3
    g196: Circle CenterX=-57 CenterY=-67 CenterZ=0 NormalX=0 NormalY=0 NormalZ=1 AngleXU=0 Radius=1.3
    g197: Circle CenterX=-62 CenterY=-67 CenterZ=0 NormalX=0 NormalY=0 NormalZ=1 AngleXU=0 Radius=1.3
    g198: Circle CenterX=-67 CenterY=-67 CenterZ=0 NormalX=0 NormalY=0 NormalZ=1 AngleXU=0 Radius=1.3
    g199: Circle CenterX=-72 CenterY=-67 CenterZ=0 NormalX=0 NormalY=0 NormalZ=1 AngleXU=0 Radius=1.3
    g200: Circle CenterX=-47 CenterY=-72 CenterZ=0 NormalX=0 NormalY=0 NormalZ=1 AngleXU=0 Radius=1.3
    g201: Circle CenterX=-52 CenterY=-72 CenterZ=0 NormalX=0 NormalY=0 NormalZ=1 AngleXU=0 Radius=1.3
    g202: Circle CenterX=-57 CenterY=-72 CenterZ=0 NormalX=0 NormalY=0 NormalZ=1 AngleXU=0 Radius=1.3
    g203: Circle CenterX=-62 CenterY=-72 CenterZ=0 NormalX=0 NormalY=0 NormalZ=1 AngleXU=0 Radius=1.3
    g204: Circle CenterX=-67 CenterY=-72 CenterZ=0 NormalX=0 NormalY=0 NormalZ=1 AngleXU=0 Radius=1.3
    g205: Circle CenterX=-72 CenterY=-72 CenterZ=0 NormalX=0 NormalY=0 NormalZ=1 AngleXU=0 Radius=1.3
    g206: Circle CenterX=-47 CenterY=-77 CenterZ=0 NormalX=0 NormalY=0 NormalZ=1 AngleXU=0 Radius=1.3
    g207: Circle CenterX=-52 CenterY=-77 CenterZ=0 NormalX=0 NormalY=0 NormalZ=1 AngleXU=0 Radius=1.3
    g208: Circle CenterX=-57 CenterY=-77 CenterZ=0 NormalX=0 NormalY=0 NormalZ=1 AngleXU=0 Radius=1.3
    g209: Circle CenterX=-62 CenterY=-77 CenterZ=0 NormalX=0 NormalY=0 NormalZ=1 AngleXU=0 Radius=1.3
    g210: Circle CenterX=-67 CenterY=-77 CenterZ=0 NormalX=0 NormalY=0 NormalZ=1 AngleXU=0 Radius=1.3
    g211: Circle CenterX=-72 CenterY=-77 CenterZ=0 NormalX=0 NormalY=0 NormalZ=1 AngleXU=0 Radius=1.3
  constraints (215):
    c: Symmetric(g-4,g-4,g0)
    c: Symmetric(g-6,g-6,g0)
    c: Symmetric(g0,g0,g1)
    c: Diameter(g2) = 2.6
    c: Coincident(g2,g1)
    c: Diameter(g3) = 2.6
    c: Diameter(g4) = 2.6
    c: Diameter(g5) = 2.6
    c: Diameter(g6) = 2.6
    c: Diameter(g7) = 2.6
    c: Diameter(g8) = 2.6
    c: Diameter(g10) = 2.6
    c: Diameter(g18) = 2.6
    c: Diameter(g26) = 2.6
    c: Diameter(g34) = 2.6
    c: Diameter(g42) = 2.6
    c: Diameter(g50) = 2.6
    c: Diameter(g58) = 2.6
    c: Coincident(g10,g9)
    c: Coincident(g18,g17)
    c: Coincident(g26,g25)
    c: Coincident(g34,g33)
    c: Coincident(g42,g41)
    c: Coincident(g50,g49)
    c: Coincident(g58,g57)
    c: Diameter(g11) = 2.6
    c: Diameter(g19) = 2.6
    c: Diameter(g27) = 2.6
    c: Diameter(g35) = 2.6
    c: Diameter(g43) = 2.6
    c: Diameter(g51) = 2.6
    c: Diameter(g59) = 2.6
    c: Diameter(g12) = 2.6
    c: Diameter(g20) = 2.6
    c: Diameter(g28) = 2.6
    c: Diameter(g36) = 2.6
    c: Diameter(g44) = 2.6
    c: Diameter(g52) = 2.6
    c: Diameter(g60) = 2.6
    c: Diameter(g13) = 2.6
    c: Diameter(g21) = 2.6
    c: Diameter(g29) = 2.6
    c: Diameter(g37) = 2.6
    c: Diameter(g45) = 2.6
    c: Diameter(g53) = 2.6
    c: Diameter(g61) = 2.6
    c: Diameter(g14) = 2.6
    c: Diameter(g22) = 2.6
    c: Diameter(g30) = 2.6
    c: Diameter(g38) = 2.6
    c: Diameter(g46) = 2.6
    c: Diameter(g54) = 2.6
    c: Diameter(g62) = 2.6
    c: Diameter(g15) = 2.6
    c: Diameter(g23) = 2.6
    c: Diameter(g31) = 2.6
    c: Diameter(g39) = 2.6
    c: Diameter(g47) = 2.6
    c: Diameter(g55) = 2.6
    c: Diameter(g63) = 2.6
    c: Diameter(g16) = 2.6
    c: Diameter(g24) = 2.6
    c: Diameter(g32) = 2.6
    c: Diameter(g40) = 2.6
    c: Diameter(g48) = 2.6
    c: Diameter(g56) = 2.6
    c: Diameter(g64) = 2.6
    c: Symmetric(g-3,g-3,g65)
    c: Symmetric(g-5,g-5,g65)
    c: Diameter(g66) = 2.6
    c: Diameter(g67) = 2.6
    c: Diameter(g68) = 2.6
    c: Diameter(g69) = 2.6
    c: Diameter(g70) = 2.6
    c: Diameter(g71) = 2.6
    c: Diameter(g72) = 2.6
    c: Diameter(g78) = 2.6
    c: Diameter(g84) = 2.6
    c: Diameter(g90) = 2.6
    c: Diameter(g96) = 2.6
    c: Diameter(g102) = 2.6
    c: Diameter(g108) = 2.6
    c: Diameter(g73) = 2.6
    c: Diameter(g79) = 2.6
    c: Diameter(g85) = 2.6
    c: Diameter(g91) = 2.6
    c: Diameter(g97) = 2.6
    c: Diameter(g103) = 2.6
    c: Diameter(g109) = 2.6
    c: Diameter(g74) = 2.6
    c: Diameter(g80) = 2.6
    c: Diameter(g86) = 2.6
    c: Diameter(g92) = 2.6
    c: Diameter(g98) = 2.6
    c: Diameter(g104) = 2.6
    c: Diameter(g110) = 2.6
    c: Diameter(g75) = 2.6
    c: Diameter(g81) = 2.6
    c: Diameter(g87) = 2.6
    c: Diameter(g93) = 2.6
    c: Diameter(g99) = 2.6
    c: Diameter(g105) = 2.6
    c: Diameter(g111) = 2.6
    c: Diameter(g76) = 2.6
    c: Diameter(g82) = 2.6
    c: Diameter(g88) = 2.6
    c: Diameter(g94) = 2.6
    c: Diameter(g100) = 2.6
    c: Diameter(g106) = 2.6
    c: Diameter(g112) = 2.6
    c: Diameter(g77) = 2.6
    c: Diameter(g83) = 2.6
    c: Diameter(g89) = 2.6
    c: Diameter(g95) = 2.6
    c: Diameter(g101) = 2.6
    c: Diameter(g107) = 2.6
    c: Diameter(g113) = 2.6
    c: Diameter(g115) = 2.6
    c: Diameter(g123) = 2.6
    c: Diameter(g131) = 2.6
    c: Diameter(g139) = 2.6
    c: Diameter(g147) = 2.6
    c: Diameter(g155) = 2.6
    c: Diameter(g163) = 2.6
    c: Coincident(g115,g114)
    c: Coincident(g123,g122)
    c: Coincident(g131,g130)
    c: Coincident(g139,g138)
    c: Coincident(g147,g146)
    c: Coincident(g155,g154)
    c: Coincident(g163,g162)
    c: Diameter(g116) = 2.6
    c: Diameter(g124) = 2.6
    c: Diameter(g132) = 2.6
    c: Diameter(g140) = 2.6
    c: Diameter(g148) = 2.6
    c: Diameter(g156) = 2.6
    c: Diameter(g164) = 2.6
    c: Diameter(g117) = 2.6
    c: Diameter(g125) = 2.6
    c: Diameter(g133) = 2.6
    c: Diameter(g141) = 2.6
    c: Diameter(g149) = 2.6
    c: Diameter(g157) = 2.6
    c: Diameter(g165) = 2.6
    c: Diameter(g118) = 2.6
    c: Diameter(g126) = 2.6
    c: Diameter(g134) = 2.6
    c: Diameter(g142) = 2.6
    c: Diameter(g150) = 2.6
    c: Diameter(g158) = 2.6
    c: Diameter(g166) = 2.6
    c: Diameter(g119) = 2.6
    c: Diameter(g127) = 2.6
    c: Diameter(g135) = 2.6
    c: Diameter(g143) = 2.6
    c: Diameter(g151) = 2.6
    c: Diameter(g159) = 2.6
    c: Diameter(g167) = 2.6
    c: Diameter(g120) = 2.6
    c: Diameter(g128) = 2.6
    c: Diameter(g136) = 2.6
    c: Diameter(g144) = 2.6
    c: Diameter(g152) = 2.6
    c: Diameter(g160) = 2.6
    c: Diameter(g168) = 2.6
    c: Diameter(g121) = 2.6
    c: Diameter(g129) = 2.6
    c: Diameter(g137) = 2.6
    c: Diameter(g145) = 2.6
    c: Diameter(g153) = 2.6
    c: Diameter(g161) = 2.6
    c: Diameter(g169) = 2.6
    c: Diameter(g170) = 2.6
    c: Diameter(g176) = 2.6
    c: Diameter(g182) = 2.6
    c: Diameter(g188) = 2.6
    c: Diameter(g194) = 2.6
    c: Diameter(g200) = 2.6
    c: Diameter(g206) = 2.6
    c: Diameter(g171) = 2.6
    c: Diameter(g177) = 2.6
    c: Diameter(g183) = 2.6
    c: Diameter(g189) = 2.6
    c: Diameter(g195) = 2.6
    c: Diameter(g201) = 2.6
    c: Diameter(g207) = 2.6
    c: Diameter(g172) = 2.6
    c: Diameter(g178) = 2.6
    c: Diameter(g184) = 2.6
    c: Diameter(g190) = 2.6
    c: Diameter(g196) = 2.6
    c: Diameter(g202) = 2.6
    c: Diameter(g208) = 2.6
    c: Diameter(g173) = 2.6
    c: Diameter(g179) = 2.6
    c: Diameter(g185) = 2.6
    c: Diameter(g191) = 2.6
    c: Diameter(g197) = 2.6
    c: Diameter(g203) = 2.6
    c: Diameter(g209) = 2.6
    c: Diameter(g174) = 2.6
    c: Diameter(g180) = 2.6
    c: Diameter(g186) = 2.6
    c: Diameter(g192) = 2.6
    c: Diameter(g198) = 2.6
    c: Diameter(g204) = 2.6
    c: Diameter(g210) = 2.6
    c: Diameter(g175) = 2.6
    c: Diameter(g181) = 2.6
    c: Diameter(g187) = 2.6
    c: Diameter(g193) = 2.6
    c: Diameter(g199) = 2.6
    c: Diameter(g205) = 2.6
    c: Diameter(g211) = 2.6
FEATURE [PartDesign::Pocket] Pocket012
  BaseFeature = -> Pad018
  Direction = (-2.80598e-09,0,-1)
  Length = 8
  Length2 = 5
  Placement = pos=(7.67535e-08,-84,27.3536) rot=(0,0,1;3.14159rad)
  Profile = -> Sketch034
  ReferenceAxis = -> Sketch034 [N_Axis]
  Refine = true
  Suppressed = false
  Type = 0
FEATURE [PartDesign::Body] Body008  label="Mounting Plate"
  AllowCompound = false
  Group = -> [DatumPlane010,CopyPocket011,Sketch032,Pad017,Sketch033,Pad018,Sketch034,Pocket012]
  Origin = -> Origin008
  Tip = -> Pocket012
FEATURE [Sketcher::SketchObject] Sketch035
  ArcFitTolerance = 1e-06
  AttachmentSupport = -> [Pad012]
  FullyConstrained = true
  MakeInternals = false
  MapMode = 5
  Placement = pos=(42.0016,5.00002,14) rot=(0.577354,0.577344,0.577354;4.18878rad)
  sketch-geometry (1):
    g0: Circle CenterX=0 CenterY=0 CenterZ=0 NormalX=0 NormalY=0 NormalZ=1 AngleXU=0 Radius=1.35
  constraints (2):
    c: Diameter(g0) = 2.7
    c: Coincident(g0,g-1)
FEATURE [PartDesign::Pocket] Pocket013
  BaseFeature = -> Pad012
  Direction = (-1.755e-05,-1,-1.0234e-10)
  Length = 5
  Length2 = 5
  Placement = pos=(42,-84,14) rot=(0.57735,-0.57735,0.57735;2.0944rad)
  Profile = -> Sketch035
  ReferenceAxis = -> Sketch035 [N_Axis]
  Refine = true
  Suppressed = false
  Type = 0
FEATURE [Sketcher::SketchObject] Sketch036
  ArcFitTolerance = 1e-06
  AttachmentSupport = -> [Pocket013]
  ExternalGeometry = -> [Pocket013]
  FullyConstrained = true
  MakeInternals = false
  MapMode = 5
  Placement = pos=(42.0016,5.00002,14) rot=(0.577354,0.577344,0.577354;4.18878rad)
  sketch-geometry (2):
    g0: Circle CenterX=0 CenterY=0 CenterZ=0 NormalX=0 NormalY=0 NormalZ=1 AngleXU=0 Radius=2.5
    g1: Circle CenterX=0 CenterY=0 CenterZ=0 NormalX=0 NormalY=0 NormalZ=1 AngleXU=0 Radius=2.9
  constraints (4):
    c: Diameter(g0) = 5
    c: Coincident(g0,g-1)
    c: Coincident(g1,g0)
    c: Tangent(g1,g-3)
FEATURE [PartDesign::Pocket] Pocket014
  BaseFeature = -> Pocket013
  Direction = (-1.755e-05,-1,-1.0234e-10)
  Length = 10
  Length2 = 5
  Placement = pos=(42,-84,14) rot=(0.57735,-0.57735,0.57735;2.0944rad)
  Profile = -> Sketch036
  ReferenceAxis = -> Sketch036 [N_Axis]
  Refine = true
  Suppressed = false
  Type = 0
FEATURE [Sketcher::SketchObject] Sketch037
  ArcFitTolerance = 1e-06
  AttachmentSupport = -> [Pocket011]
  ExternalGeometry = -> [Pocket011]
  FullyConstrained = true
  MakeInternals = false
  MapMode = 5
  Placement = pos=(84,-84,-1.80021e-08) rot=(0.707107,0,0.707107;3.14159rad)
  sketch-geometry (3):
    g0: Circle CenterX=12.3536 CenterY=-21 CenterZ=0 NormalX=0 NormalY=0 NormalZ=1 AngleXU=0 Radius=3
    g1: Circle CenterX=12.3536 CenterY=-42 CenterZ=0 NormalX=0 NormalY=0 NormalZ=1 AngleXU=0 Radius=3
    g2: Circle CenterX=12.3536 CenterY=-63 CenterZ=0 NormalX=0 NormalY=0 NormalZ=1 AngleXU=0 Radius=3
  constraints (6):
    c: Diameter(g0) = 6
    c: Coincident(g0,g-3)
    c: Diameter(g1) = 6
    c: Coincident(g1,g-4)
    c: Diameter(g2) = 6
    c: Coincident(g2,g-5)
FEATURE [PartDesign::Pocket] Pocket015
  BaseFeature = -> Pocket011
  Direction = (-1,0,2.14311e-10)
  Length = 7
  Length2 = 5
  Placement = pos=(0,-84,2e-15) rot=(1,0,0;1.5708rad)
  Profile = -> Sketch037
  ReferenceAxis = -> Sketch037 [N_Axis]
  Refine = true
  Suppressed = false
  Type = 0
FEATURE [Sketcher::SketchObject] Sketch038
  ArcFitTolerance = 1e-06
  AttachmentSupport = -> [Fillet005]
  ExternalGeometry = -> [Fillet005]
  FullyConstrained = false
  MakeInternals = false
  MapMode = 5
  Placement = pos=(0,0,0) rot=(0.707107,0,-0.707107;3.14159rad)
  sketch-geometry (332):
    g0: LineSegment [constr] StartX=-5 StartY=0 StartZ=0 EndX=-5 EndY=1 EndZ=0
    g1: LineSegment StartX=-5 StartY=1 StartZ=0 EndX=-3.00761 EndY=1.17431 EndZ=0
    g2: LineSegment StartX=-5 StartY=1 StartZ=0 EndX=-3.00761 EndY=0.825689 EndZ=0
    g3: LineSegment StartX=-3.00761 StartY=0.825689 StartZ=0 EndX=-3.00761 EndY=1.17431 EndZ=0
    g4: LineSegment [constr] StartX=-5 StartY=1 StartZ=0 EndX=-5 EndY=2 EndZ=0
    g5: LineSegment StartX=-5 StartY=2 StartZ=0 EndX=-3.00761 EndY=2.17431 EndZ=0
    g6: LineSegment StartX=-5 StartY=2 StartZ=0 EndX=-3.00761 EndY=1.82569 EndZ=0
    g7: LineSegment StartX=-3.00761 StartY=1.82569 StartZ=0 EndX=-3.00761 EndY=2.17431 EndZ=0
    g8: LineSegment [constr] StartX=-5 StartY=2 StartZ=0 EndX=-5 EndY=3 EndZ=0
    g9: LineSegment StartX=-5 StartY=3 StartZ=0 EndX=-3.00761 EndY=3.17431 EndZ=0
    g10: LineSegment StartX=-5 StartY=3 StartZ=0 EndX=-3.00761 EndY=2.82569 EndZ=0
    g11: LineSegment StartX=-3.00761 StartY=2.82569 StartZ=0 EndX=-3.00761 EndY=3.17431 EndZ=0
    g12: LineSegment [constr] StartX=-5 StartY=3 StartZ=0 EndX=-5 EndY=4 EndZ=0
    g13: LineSegment StartX=-5 StartY=4 StartZ=0 EndX=-3.00761 EndY=4.17431 EndZ=0
    g14: LineSegment StartX=-5 StartY=4 StartZ=0 EndX=-3.00761 EndY=3.82569 EndZ=0
    g15: LineSegment StartX=-3.00761 StartY=3.82569 StartZ=0 EndX=-3.00761 EndY=4.17431 EndZ=0
    g16: LineSegment [constr] StartX=-5 StartY=4 StartZ=0 EndX=-5 EndY=5 EndZ=0
    g17: LineSegment StartX=-5 StartY=5 StartZ=0 EndX=-3.00761 EndY=5.17431 EndZ=0
    g18: LineSegment StartX=-5 StartY=5 StartZ=0 EndX=-3.00761 EndY=4.82569 EndZ=0
    g19: LineSegment StartX=-3.00761 StartY=4.82569 StartZ=0 EndX=-3.00761 EndY=5.17431 EndZ=0
    g20: LineSegment [constr] StartX=-5 StartY=5 StartZ=0 EndX=-5 EndY=6 EndZ=0
    g21: LineSegment StartX=-5 StartY=6 StartZ=0 EndX=-3.00761 EndY=6.17431 EndZ=0
    g22: LineSegment StartX=-5 StartY=6 StartZ=0 EndX=-3.00761 EndY=5.82569 EndZ=0
    g23: LineSegment StartX=-3.00761 StartY=5.82569 StartZ=0 EndX=-3.00761 EndY=6.17431 EndZ=0
    g24: LineSegment [constr] StartX=-5 StartY=6 StartZ=0 EndX=-5 EndY=7 EndZ=0
    g25: LineSegment StartX=-5 StartY=7 StartZ=0 EndX=-3.00761 EndY=7.17431 EndZ=0
    g26: LineSegment StartX=-5 StartY=7 StartZ=0 EndX=-3.00761 EndY=6.82569 EndZ=0
    g27: LineSegment StartX=-3.00761 StartY=6.82569 StartZ=0 EndX=-3.00761 EndY=7.17431 EndZ=0
    g28: LineSegment [constr] StartX=-5 StartY=7 StartZ=0 EndX=-5 EndY=8 EndZ=0
    g29: LineSegment StartX=-5 StartY=8 StartZ=0 EndX=-3.00761 EndY=8.17431 EndZ=0
    g30: LineSegment StartX=-5 StartY=8 StartZ=0 EndX=-3.00761 EndY=7.82569 EndZ=0
    g31: LineSegment StartX=-3.00761 StartY=7.82569 StartZ=0 EndX=-3.00761 EndY=8.17431 EndZ=0
    g32: LineSegment [constr] StartX=-5 StartY=8 StartZ=0 EndX=-5 EndY=9 EndZ=0
    g33: LineSegment StartX=-5 StartY=9 StartZ=0 EndX=-3.00761 EndY=9.17431 EndZ=0
    g34: LineSegment StartX=-5 StartY=9 StartZ=0 EndX=-3.00761 EndY=8.82569 EndZ=0
    g35: LineSegment StartX=-3.00761 StartY=8.82569 StartZ=0 EndX=-3.00761 EndY=9.17431 EndZ=0
    g36: LineSegment [constr] StartX=-5 StartY=9 StartZ=0 EndX=-5 EndY=10 EndZ=0
    g37: LineSegment StartX=-5 StartY=10 StartZ=0 EndX=-3.00761 EndY=10.1743 EndZ=0
    g38: LineSegment StartX=-5 StartY=10 StartZ=0 EndX=-3.00761 EndY=9.82569 EndZ=0
    g39: LineSegment StartX=-3.00761 StartY=9.82569 StartZ=0 EndX=-3.00761 EndY=10.1743 EndZ=0
    g40: LineSegment [constr] StartX=-5 StartY=10 StartZ=0 EndX=-5 EndY=11 EndZ=0
    g41: LineSegment StartX=-5 StartY=11 StartZ=0 EndX=-3.00761 EndY=11.1743 EndZ=0
    g42: LineSegment StartX=-5 StartY=11 StartZ=0 EndX=-3.00761 EndY=10.8257 EndZ=0
    g43: LineSegment StartX=-3.00761 StartY=10.8257 StartZ=0 EndX=-3.00761 EndY=11.1743 EndZ=0
    g44: LineSegment [constr] StartX=-5 StartY=11 StartZ=0 EndX=-5 EndY=12 EndZ=0
    g45: LineSegment StartX=-5 StartY=12 StartZ=0 EndX=-3.00761 EndY=12.1743 EndZ=0
    g46: LineSegment StartX=-5 StartY=12 StartZ=0 EndX=-3.00761 EndY=11.8257 EndZ=0
    g47: LineSegment StartX=-3.00761 StartY=11.8257 StartZ=0 EndX=-3.00761 EndY=12.1743 EndZ=0
    g48: LineSegment [constr] StartX=-5 StartY=12 StartZ=0 EndX=-5 EndY=13 EndZ=0
    g49: LineSegment StartX=-5 StartY=13 StartZ=0 EndX=-3.00761 EndY=13.1743 EndZ=0
    g50: LineSegment StartX=-5 StartY=13 StartZ=0 EndX=-3.00761 EndY=12.8257 EndZ=0
    g51: LineSegment StartX=-3.00761 StartY=12.8257 StartZ=0 EndX=-3.00761 EndY=13.1743 EndZ=0
    g52: LineSegment [constr] StartX=-5 StartY=13 StartZ=0 EndX=-5 EndY=14 EndZ=0
    g53: LineSegment StartX=-5 StartY=14 StartZ=0 EndX=-3.00761 EndY=14.1743 EndZ=0
    g54: LineSegment StartX=-5 StartY=14 StartZ=0 EndX=-3.00761 EndY=13.8257 EndZ=0
    g55: LineSegment StartX=-3.00761 StartY=13.8257 StartZ=0 EndX=-3.00761 EndY=14.1743 EndZ=0
    g56: LineSegment [constr] StartX=-5 StartY=14 StartZ=0 EndX=-5 EndY=15 EndZ=0
    g57: LineSegment StartX=-5 StartY=15 StartZ=0 EndX=-3.00761 EndY=15.1743 EndZ=0
    g58: LineSegment StartX=-5 StartY=15 StartZ=0 EndX=-3.00761 EndY=14.8257 EndZ=0
    g59: LineSegment StartX=-3.00761 StartY=14.8257 StartZ=0 EndX=-3.00761 EndY=15.1743 EndZ=0
    g60: LineSegment [constr] StartX=-5 StartY=15 StartZ=0 EndX=-5 EndY=16 EndZ=0
    g61: LineSegment StartX=-5 StartY=16 StartZ=0 EndX=-3.00761 EndY=16.1743 EndZ=0
    g62: LineSegment StartX=-5 StartY=16 StartZ=0 EndX=-3.00761 EndY=15.8257 EndZ=0
    g63: LineSegment StartX=-3.00761 StartY=15.8257 StartZ=0 EndX=-3.00761 EndY=16.1743 EndZ=0
    g64: LineSegment [constr] StartX=-5 StartY=16 StartZ=0 EndX=-5 EndY=17 EndZ=0
    g65: LineSegment StartX=-5 StartY=17 StartZ=0 EndX=-3.00761 EndY=17.1743 EndZ=0
    g66: LineSegment StartX=-5 StartY=17 StartZ=0 EndX=-3.00761 EndY=16.8257 EndZ=0
    g67: LineSegment StartX=-3.00761 StartY=16.8257 StartZ=0 EndX=-3.00761 EndY=17.1743 EndZ=0
    g68: LineSegment [constr] StartX=-5 StartY=17 StartZ=0 EndX=-5 EndY=18 EndZ=0
    g69: LineSegment StartX=-5 StartY=18 StartZ=0 EndX=-3.00761 EndY=18.1743 EndZ=0
    g70: LineSegment StartX=-5 StartY=18 StartZ=0 EndX=-3.00761 EndY=17.8257 EndZ=0
    g71: LineSegment StartX=-3.00761 StartY=17.8257 StartZ=0 EndX=-3.00761 EndY=18.1743 EndZ=0
    g72: LineSegment [constr] StartX=-5 StartY=18 StartZ=0 EndX=-5 EndY=19 EndZ=0
    g73: LineSegment StartX=-5 StartY=19 StartZ=0 EndX=-3.00761 EndY=19.1743 EndZ=0
    g74: LineSegment StartX=-5 StartY=19 StartZ=0 EndX=-3.00761 EndY=18.8257 EndZ=0
    g75: LineSegment StartX=-3.00761 StartY=18.8257 StartZ=0 EndX=-3.00761 EndY=19.1743 EndZ=0
    g76: LineSegment [constr] StartX=-5 StartY=19 StartZ=0 EndX=-5 EndY=20 EndZ=0
    g77: LineSegment StartX=-5 StartY=20 StartZ=0 EndX=-3.00761 EndY=20.1743 EndZ=0
    g78: LineSegment StartX=-5 StartY=20 StartZ=0 EndX=-3.00761 EndY=19.8257 EndZ=0
    g79: LineSegment StartX=-3.00761 StartY=19.8257 StartZ=0 EndX=-3.00761 EndY=20.1743 EndZ=0
    g80: LineSegment [constr] StartX=-5 StartY=20 StartZ=0 EndX=-5 EndY=21 EndZ=0
    g81: LineSegment StartX=-5 StartY=21 StartZ=0 EndX=-3.00761 EndY=21.1743 EndZ=0
    g82: LineSegment StartX=-5 StartY=21 StartZ=0 EndX=-3.00761 EndY=20.8257 EndZ=0
    g83: LineSegment StartX=-3.00761 StartY=20.8257 StartZ=0 EndX=-3.00761 EndY=21.1743 EndZ=0
    g84: LineSegment [constr] StartX=-5 StartY=21 StartZ=0 EndX=-5 EndY=22 EndZ=0
    g85: LineSegment StartX=-5 StartY=22 StartZ=0 EndX=-3.00761 EndY=22.1743 EndZ=0
    g86: LineSegment StartX=-5 StartY=22 StartZ=0 EndX=-3.00761 EndY=21.8257 EndZ=0
    g87: LineSegment StartX=-3.00761 StartY=21.8257 StartZ=0 EndX=-3.00761 EndY=22.1743 EndZ=0
    g88: LineSegment [constr] StartX=-5 StartY=22 StartZ=0 EndX=-5 EndY=23 EndZ=0
    g89: LineSegment StartX=-5 StartY=23 StartZ=0 EndX=-3.00761 EndY=23.1743 EndZ=0
    g90: LineSegment StartX=-5 StartY=23 StartZ=0 EndX=-3.00761 EndY=22.8257 EndZ=0
    g91: LineSegment StartX=-3.00761 StartY=22.8257 StartZ=0 EndX=-3.00761 EndY=23.1743 EndZ=0
    g92: LineSegment [constr] StartX=-5 StartY=23 StartZ=0 EndX=-5 EndY=24 EndZ=0
    g93: LineSegment StartX=-5 StartY=24 StartZ=0 EndX=-3.00761 EndY=24.1743 EndZ=0
    g94: LineSegment StartX=-5 StartY=24 StartZ=0 EndX=-3.00761 EndY=23.8257 EndZ=0
    g95: LineSegment StartX=-3.00761 StartY=23.8257 StartZ=0 EndX=-3.00761 EndY=24.1743 EndZ=0
    g96: LineSegment [constr] StartX=-5 StartY=24 StartZ=0 EndX=-5 EndY=25 EndZ=0
    g97: LineSegment StartX=-5 StartY=25 StartZ=0 EndX=-3.00761 EndY=25.1743 EndZ=0
    g98: LineSegment StartX=-5 StartY=25 StartZ=0 EndX=-3.00761 EndY=24.8257 EndZ=0
    g99: LineSegment StartX=-3.00761 StartY=24.8257 StartZ=0 EndX=-3.00761 EndY=25.1743 EndZ=0
    g100: LineSegment [constr] StartX=-5 StartY=25 StartZ=0 EndX=-5 EndY=26 EndZ=0
    g101: LineSegment StartX=-5 StartY=26 StartZ=0 EndX=-3.00761 EndY=26.1743 EndZ=0
    g102: LineSegment StartX=-5 StartY=26 StartZ=0 EndX=-3.00761 EndY=25.8257 EndZ=0
    g103: LineSegment StartX=-3.00761 StartY=25.8257 StartZ=0 EndX=-3.00761 EndY=26.1743 EndZ=0
    g104: LineSegment [constr] StartX=-5 StartY=26 StartZ=0 EndX=-5 EndY=27 EndZ=0
    g105: LineSegment StartX=-5 StartY=27 StartZ=0 EndX=-3.00761 EndY=27.1743 EndZ=0
    g106: LineSegment StartX=-5 StartY=27 StartZ=0 EndX=-3.00761 EndY=26.8257 EndZ=0
    g107: LineSegment StartX=-3.00761 StartY=26.8257 StartZ=0 EndX=-3.00761 EndY=27.1743 EndZ=0
    g108: LineSegment [constr] StartX=-5 StartY=27 StartZ=0 EndX=-5 EndY=28 EndZ=0
    g109: LineSegment StartX=-5 StartY=28 StartZ=0 EndX=-3.00761 EndY=28.1743 EndZ=0
    g110: LineSegment StartX=-5 StartY=28 StartZ=0 EndX=-3.00761 EndY=27.8257 EndZ=0
    g111: LineSegment StartX=-3.00761 StartY=27.8257 StartZ=0 EndX=-3.00761 EndY=28.1743 EndZ=0
    g112: LineSegment [constr] StartX=-5 StartY=28 StartZ=0 EndX=-5 EndY=29 EndZ=0
    g113: LineSegment StartX=-5 StartY=29 StartZ=0 EndX=-3.00761 EndY=29.1743 EndZ=0
    g114: LineSegment StartX=-5 StartY=29 StartZ=0 EndX=-3.00761 EndY=28.8257 EndZ=0
    g115: LineSegment StartX=-3.00761 StartY=28.8257 StartZ=0 EndX=-3.00761 EndY=29.1743 EndZ=0
    g116: LineSegment [constr] StartX=-5 StartY=29 StartZ=0 EndX=-5 EndY=30 EndZ=0
    g117: LineSegment StartX=-5 StartY=30 StartZ=0 EndX=-3.00761 EndY=30.1743 EndZ=0
    g118: LineSegment StartX=-5 StartY=30 StartZ=0 EndX=-3.00761 EndY=29.8257 EndZ=0
    g119: LineSegment StartX=-3.00761 StartY=29.8257 StartZ=0 EndX=-3.00761 EndY=30.1743 EndZ=0
    g120: LineSegment [constr] StartX=-5 StartY=30 StartZ=0 EndX=-5 EndY=31 EndZ=0
    g121: LineSegment StartX=-5 StartY=31 StartZ=0 EndX=-3.00761 EndY=31.1743 EndZ=0
    g122: LineSegment StartX=-5 StartY=31 StartZ=0 EndX=-3.00761 EndY=30.8257 EndZ=0
    g123: LineSegment StartX=-3.00761 StartY=30.8257 StartZ=0 EndX=-3.00761 EndY=31.1743 EndZ=0
    g124: LineSegment [constr] StartX=-5 StartY=31 StartZ=0 EndX=-5 EndY=32 EndZ=0
    g125: LineSegment StartX=-5 StartY=32 StartZ=0 EndX=-3.00761 EndY=32.1743 EndZ=0
    g126: LineSegment StartX=-5 StartY=32 StartZ=0 EndX=-3.00761 EndY=31.8257 EndZ=0
    g127: LineSegment StartX=-3.00761 StartY=31.8257 StartZ=0 EndX=-3.00761 EndY=32.1743 EndZ=0
    g128: LineSegment [constr] StartX=-5 StartY=32 StartZ=0 EndX=-5 EndY=33 EndZ=0
    g129: LineSegment StartX=-5 StartY=33 StartZ=0 EndX=-3.00761 EndY=33.1743 EndZ=0
    g130: LineSegment StartX=-5 StartY=33 StartZ=0 EndX=-3.00761 EndY=32.8257 EndZ=0
    g131: LineSegment StartX=-3.00761 StartY=32.8257 StartZ=0 EndX=-3.00761 EndY=33.1743 EndZ=0
    g132: LineSegment [constr] StartX=-5 StartY=33 StartZ=0 EndX=-5 EndY=34 EndZ=0
    g133: LineSegment StartX=-5 StartY=34 StartZ=0 EndX=-3.00761 EndY=34.1743 EndZ=0
    g134: LineSegment StartX=-5 StartY=34 StartZ=0 EndX=-3.00761 EndY=33.8257 EndZ=0
    g135: LineSegment StartX=-3.00761 StartY=33.8257 StartZ=0 EndX=-3.00761 EndY=34.1743 EndZ=0
    g136: LineSegment [constr] StartX=-5 StartY=34 StartZ=0 EndX=-5 EndY=35 EndZ=0
    g137: LineSegment StartX=-5 StartY=35 StartZ=0 EndX=-3.00761 EndY=35.1743 EndZ=0
    g138: LineSegment StartX=-5 StartY=35 StartZ=0 EndX=-3.00761 EndY=34.8257 EndZ=0
    g139: LineSegment StartX=-3.00761 StartY=34.8257 StartZ=0 EndX=-3.00761 EndY=35.1743 EndZ=0
    g140: LineSegment [constr] StartX=-5 StartY=35 StartZ=0 EndX=-5 EndY=36 EndZ=0
    g141: LineSegment StartX=-5 StartY=36 StartZ=0 EndX=-3.00761 EndY=36.1743 EndZ=0
    g142: LineSegment StartX=-5 StartY=36 StartZ=0 EndX=-3.00761 EndY=35.8257 EndZ=0
    g143: LineSegment StartX=-3.00761 StartY=35.8257 StartZ=0 EndX=-3.00761 EndY=36.1743 EndZ=0
    g144: LineSegment [constr] StartX=-5 StartY=36 StartZ=0 EndX=-5 EndY=37 EndZ=0
    g145: LineSegment StartX=-5 StartY=37 StartZ=0 EndX=-3.00761 EndY=37.1743 EndZ=0
    g146: LineSegment StartX=-5 StartY=37 StartZ=0 EndX=-3.00761 EndY=36.8257 EndZ=0
    g147: LineSegment StartX=-3.00761 StartY=36.8257 StartZ=0 EndX=-3.00761 EndY=37.1743 EndZ=0
    g148: LineSegment [constr] StartX=-5 StartY=37 StartZ=0 EndX=-5 EndY=38 EndZ=0
    g149: LineSegment StartX=-5 StartY=38 StartZ=0 EndX=-3.00761 EndY=38.1743 EndZ=0
    g150: LineSegment StartX=-5 StartY=38 StartZ=0 EndX=-3.00761 EndY=37.8257 EndZ=0
    g151: LineSegment StartX=-3.00761 StartY=37.8257 StartZ=0 EndX=-3.00761 EndY=38.1743 EndZ=0
    g152: LineSegment [constr] StartX=-5 StartY=38 StartZ=0 EndX=-5 EndY=39 EndZ=0
    g153: LineSegment StartX=-5 StartY=39 StartZ=0 EndX=-3.00761 EndY=39.1743 EndZ=0
    g154: LineSegment StartX=-5 StartY=39 StartZ=0 EndX=-3.00761 EndY=38.8257 EndZ=0
    g155: LineSegment StartX=-3.00761 StartY=38.8257 StartZ=0 EndX=-3.00761 EndY=39.1743 EndZ=0
    g156: LineSegment [constr] StartX=-5 StartY=39 StartZ=0 EndX=-5 EndY=40 EndZ=0
    g157: LineSegment StartX=-5 StartY=40 StartZ=0 EndX=-3.00761 EndY=40.1743 EndZ=0
    g158: LineSegment StartX=-5 StartY=40 StartZ=0 EndX=-3.00761 EndY=39.8257 EndZ=0
    g159: LineSegment StartX=-3.00761 StartY=39.8257 StartZ=0 EndX=-3.00761 EndY=40.1743 EndZ=0
    g160: LineSegment [constr] StartX=-5 StartY=40 StartZ=0 EndX=-5 EndY=41 EndZ=0
    g161: LineSegment StartX=-5 StartY=41 StartZ=0 EndX=-3.00761 EndY=41.1743 EndZ=0
    g162: LineSegment StartX=-5 StartY=41 StartZ=0 EndX=-3.00761 EndY=40.8257 EndZ=0
    g163: LineSegment StartX=-3.00761 StartY=40.8257 StartZ=0 EndX=-3.00761 EndY=41.1743 EndZ=0
    g164: LineSegment [constr] StartX=-5 StartY=41 StartZ=0 EndX=-5 EndY=42 EndZ=0
    g165: LineSegment StartX=-5 StartY=42 StartZ=0 EndX=-3.00761 EndY=42.1743 EndZ=0
    g166: LineSegment StartX=-5 StartY=42 StartZ=0 EndX=-3.00761 EndY=41.8257 EndZ=0
    g167: LineSegment StartX=-3.00761 StartY=41.8257 StartZ=0 EndX=-3.00761 EndY=42.1743 EndZ=0
    g168: LineSegment [constr] StartX=-5 StartY=42 StartZ=0 EndX=-5 EndY=43 EndZ=0
    g169: LineSegment StartX=-5 StartY=43 StartZ=0 EndX=-3.00761 EndY=43.1743 EndZ=0
    g170: LineSegment StartX=-5 StartY=43 StartZ=0 EndX=-3.00761 EndY=42.8257 EndZ=0
    g171: LineSegment StartX=-3.00761 StartY=42.8257 StartZ=0 EndX=-3.00761 EndY=43.1743 EndZ=0
    g172: LineSegment [constr] StartX=-5 StartY=43 StartZ=0 EndX=-5 EndY=44 EndZ=0
    g173: LineSegment StartX=-5 StartY=44 StartZ=0 EndX=-3.00761 EndY=44.1743 EndZ=0
    g174: LineSegment StartX=-5 StartY=44 StartZ=0 EndX=-3.00761 EndY=43.8257 EndZ=0
    g175: LineSegment StartX=-3.00761 StartY=43.8257 StartZ=0 EndX=-3.00761 EndY=44.1743 EndZ=0
    g176: LineSegment [constr] StartX=-5 StartY=44 StartZ=0 EndX=-5 EndY=45 EndZ=0
    g177: LineSegment StartX=-5 StartY=45 StartZ=0 EndX=-3.00761 EndY=45.1743 EndZ=0
    g178: LineSegment StartX=-5 StartY=45 StartZ=0 EndX=-3.00761 EndY=44.8257 EndZ=0
    g179: LineSegment StartX=-3.00761 StartY=44.8257 StartZ=0 EndX=-3.00761 EndY=45.1743 EndZ=0
    g180: LineSegment [constr] StartX=-5 StartY=45 StartZ=0 EndX=-5 EndY=46 EndZ=0
    g181: LineSegment StartX=-5 StartY=46 StartZ=0 EndX=-3.00761 EndY=46.1743 EndZ=0
    g182: LineSegment StartX=-5 StartY=46 StartZ=0 EndX=-3.00761 EndY=45.8257 EndZ=0
    g183: LineSegment StartX=-3.00761 StartY=45.8257 StartZ=0 EndX=-3.00761 EndY=46.1743 EndZ=0
    g184: LineSegment [constr] StartX=-5 StartY=46 StartZ=0 EndX=-5 EndY=47 EndZ=0
    g185: LineSegment StartX=-5 StartY=47 StartZ=0 EndX=-3.00761 EndY=47.1743 EndZ=0
    g186: LineSegment StartX=-5 StartY=47 StartZ=0 EndX=-3.00761 EndY=46.8257 EndZ=0
    g187: LineSegment StartX=-3.00761 StartY=46.8257 StartZ=0 EndX=-3.00761 EndY=47.1743 EndZ=0
    g188: LineSegment [constr] StartX=-5 StartY=47 StartZ=0 EndX=-5 EndY=48 EndZ=0
    g189: LineSegment StartX=-5 StartY=48 StartZ=0 EndX=-3.00761 EndY=48.1743 EndZ=0
    g190: LineSegment StartX=-5 StartY=48 StartZ=0 EndX=-3.00761 EndY=47.8257 EndZ=0
    g191: LineSegment StartX=-3.00761 StartY=47.8257 StartZ=0 EndX=-3.00761 EndY=48.1743 EndZ=0
    g192: LineSegment [constr] StartX=-5 StartY=48 StartZ=0 EndX=-5 EndY=49 EndZ=0
    g193: LineSegment StartX=-5 StartY=49 StartZ=0 EndX=-3.00761 EndY=49.1743 EndZ=0
    g194: LineSegment StartX=-5 StartY=49 StartZ=0 EndX=-3.00761 EndY=48.8257 EndZ=0
    g195: LineSegment StartX=-3.00761 StartY=48.8257 StartZ=0 EndX=-3.00761 EndY=49.1743 EndZ=0
    g196: LineSegment [constr] StartX=-5 StartY=49 StartZ=0 EndX=-5 EndY=50 EndZ=0
    g197: LineSegment StartX=-5 StartY=50 StartZ=0 EndX=-3.00761 EndY=50.1743 EndZ=0
    g198: LineSegment StartX=-5 StartY=50 StartZ=0 EndX=-3.00761 EndY=49.8257 EndZ=0
    g199: LineSegment StartX=-3.00761 StartY=49.8257 StartZ=0 EndX=-3.00761 EndY=50.1743 EndZ=0
    g200: LineSegment [constr] StartX=-5 StartY=50 StartZ=0 EndX=-5 EndY=51 EndZ=0
    g201: LineSegment StartX=-5 StartY=51 StartZ=0 EndX=-3.00761 EndY=51.1743 EndZ=0
    g202: LineSegment StartX=-5 StartY=51 StartZ=0 EndX=-3.00761 EndY=50.8257 EndZ=0
    g203: LineSegment StartX=-3.00761 StartY=50.8257 StartZ=0 EndX=-3.00761 EndY=51.1743 EndZ=0
    g204: LineSegment [constr] StartX=-5 StartY=51 StartZ=0 EndX=-5 EndY=52 EndZ=0
    g205: LineSegment StartX=-5 StartY=52 StartZ=0 EndX=-3.00761 EndY=52.1743 EndZ=0
    g206: LineSegment StartX=-5 StartY=52 StartZ=0 EndX=-3.00761 EndY=51.8257 EndZ=0
    g207: LineSegment StartX=-3.00761 StartY=51.8257 StartZ=0 EndX=-3.00761 EndY=52.1743 EndZ=0
    g208: LineSegment [constr] StartX=-5 StartY=52 StartZ=0 EndX=-5 EndY=53 EndZ=0
    g209: LineSegment StartX=-5 StartY=53 StartZ=0 EndX=-3.00761 EndY=53.1743 EndZ=0
    g210: LineSegment StartX=-5 StartY=53 StartZ=0 EndX=-3.00761 EndY=52.8257 EndZ=0
    g211: LineSegment StartX=-3.00761 StartY=52.8257 StartZ=0 EndX=-3.00761 EndY=53.1743 EndZ=0
    g212: LineSegment [constr] StartX=-5 StartY=53 StartZ=0 EndX=-5 EndY=54 EndZ=0
    g213: LineSegment StartX=-5 StartY=54 StartZ=0 EndX=-3.00761 EndY=54.1743 EndZ=0
    g214: LineSegment StartX=-5 StartY=54 StartZ=0 EndX=-3.00761 EndY=53.8257 EndZ=0
    g215: LineSegment StartX=-3.00761 StartY=53.8257 StartZ=0 EndX=-3.00761 EndY=54.1743 EndZ=0
    g216: LineSegment [constr] StartX=-5 StartY=54 StartZ=0 EndX=-5 EndY=55 EndZ=0
    g217: LineSegment StartX=-5 StartY=55 StartZ=0 EndX=-3.00761 EndY=55.1743 EndZ=0
    g218: LineSegment StartX=-5 StartY=55 StartZ=0 EndX=-3.00761 EndY=54.8257 EndZ=0
    g219: LineSegment StartX=-3.00761 StartY=54.8257 StartZ=0 EndX=-3.00761 EndY=55.1743 EndZ=0
    g220: LineSegment [constr] StartX=-5 StartY=55 StartZ=0 EndX=-5 EndY=56 EndZ=0
    g221: LineSegment StartX=-5 StartY=56 StartZ=0 EndX=-3.00761 EndY=56.1743 EndZ=0
    g222: LineSegment StartX=-5 StartY=56 StartZ=0 EndX=-3.00761 EndY=55.8257 EndZ=0
    g223: LineSegment StartX=-3.00761 StartY=55.8257 StartZ=0 EndX=-3.00761 EndY=56.1743 EndZ=0
    g224: LineSegment [constr] StartX=-5 StartY=56 StartZ=0 EndX=-5 EndY=57 EndZ=0
    g225: LineSegment StartX=-5 StartY=57 StartZ=0 EndX=-3.00761 EndY=57.1743 EndZ=0
    g226: LineSegment StartX=-5 StartY=57 StartZ=0 EndX=-3.00761 EndY=56.8257 EndZ=0
    g227: LineSegment StartX=-3.00761 StartY=56.8257 StartZ=0 EndX=-3.00761 EndY=57.1743 EndZ=0
    g228: LineSegment [constr] StartX=-5 StartY=57 StartZ=0 EndX=-5 EndY=58 EndZ=0
    g229: LineSegment StartX=-5 StartY=58 StartZ=0 EndX=-3.00761 EndY=58.1743 EndZ=0
    g230: LineSegment StartX=-5 StartY=58 StartZ=0 EndX=-3.00761 EndY=57.8257 EndZ=0
    g231: LineSegment StartX=-3.00761 StartY=57.8257 StartZ=0 EndX=-3.00761 EndY=58.1743 EndZ=0
    g232: LineSegment [constr] StartX=-5 StartY=58 StartZ=0 EndX=-5 EndY=59 EndZ=0
    g233: LineSegment StartX=-5 StartY=59 StartZ=0 EndX=-3.00761 EndY=59.1743 EndZ=0
    g234: LineSegment StartX=-5 StartY=59 StartZ=0 EndX=-3.00761 EndY=58.8257 EndZ=0
    g235: LineSegment StartX=-3.00761 StartY=58.8257 StartZ=0 EndX=-3.00761 EndY=59.1743 EndZ=0
    g236: LineSegment [constr] StartX=-5 StartY=59 StartZ=0 EndX=-5 EndY=60 EndZ=0
    g237: LineSegment StartX=-5 StartY=60 StartZ=0 EndX=-3.00761 EndY=60.1743 EndZ=0
    g238: LineSegment StartX=-5 StartY=60 StartZ=0 EndX=-3.00761 EndY=59.8257 EndZ=0
    g239: LineSegment StartX=-3.00761 StartY=59.8257 StartZ=0 EndX=-3.00761 EndY=60.1743 EndZ=0
    g240: LineSegment [constr] StartX=-5 StartY=60 StartZ=0 EndX=-5 EndY=61 EndZ=0
    g241: LineSegment StartX=-5 StartY=61 StartZ=0 EndX=-3.00761 EndY=61.1743 EndZ=0
    g242: LineSegment StartX=-5 StartY=61 StartZ=0 EndX=-3.00761 EndY=60.8257 EndZ=0
    g243: LineSegment StartX=-3.00761 StartY=60.8257 StartZ=0 EndX=-3.00761 EndY=61.1743 EndZ=0
    g244: LineSegment [constr] StartX=-5 StartY=61 StartZ=0 EndX=-5 EndY=62 EndZ=0
    g245: LineSegment StartX=-5 StartY=62 StartZ=0 EndX=-3.00761 EndY=62.1743 EndZ=0
    g246: LineSegment StartX=-5 StartY=62 StartZ=0 EndX=-3.00761 EndY=61.8257 EndZ=0
    g247: LineSegment StartX=-3.00761 StartY=61.8257 StartZ=0 EndX=-3.00761 EndY=62.1743 EndZ=0
    g248: LineSegment [constr] StartX=-5 StartY=62 StartZ=0 EndX=-5 EndY=63 EndZ=0
    g249: LineSegment StartX=-5 StartY=63 StartZ=0 EndX=-3.00761 EndY=63.1743 EndZ=0
    g250: LineSegment StartX=-5 StartY=63 StartZ=0 EndX=-3.00761 EndY=62.8257 EndZ=0
    g251: LineSegment StartX=-3.00761 StartY=62.8257 StartZ=0 EndX=-3.00761 EndY=63.1743 EndZ=0
    g252: LineSegment [constr] StartX=-5 StartY=63 StartZ=0 EndX=-5 EndY=64 EndZ=0
    g253: LineSegment StartX=-5 StartY=64 StartZ=0 EndX=-3.00761 EndY=64.1743 EndZ=0
    g254: LineSegment StartX=-5 StartY=64 StartZ=0 EndX=-3.00761 EndY=63.8257 EndZ=0
    g255: LineSegment StartX=-3.00761 StartY=63.8257 StartZ=0 EndX=-3.00761 EndY=64.1743 EndZ=0
    g256: LineSegment [constr] StartX=-5 StartY=64 StartZ=0 EndX=-5 EndY=65 EndZ=0
    g257: LineSegment StartX=-5 StartY=65 StartZ=0 EndX=-3.00761 EndY=65.1743 EndZ=0
    g258: LineSegment StartX=-5 StartY=65 StartZ=0 EndX=-3.00761 EndY=64.8257 EndZ=0
    g259: LineSegment StartX=-3.00761 StartY=64.8257 StartZ=0 EndX=-3.00761 EndY=65.1743 EndZ=0
    g260: LineSegment [constr] StartX=-5 StartY=65 StartZ=0 EndX=-5 EndY=66 EndZ=0
    g261: LineSegment StartX=-5 StartY=66 StartZ=0 EndX=-3.00761 EndY=66.1743 EndZ=0
    g262: LineSegment StartX=-5 StartY=66 StartZ=0 EndX=-3.00761 EndY=65.8257 EndZ=0
    g263: LineSegment StartX=-3.00761 StartY=65.8257 StartZ=0 EndX=-3.00761 EndY=66.1743 EndZ=0
    g264: LineSegment [constr] StartX=-5 StartY=66 StartZ=0 EndX=-5 EndY=67 EndZ=0
    g265: LineSegment StartX=-5 StartY=67 StartZ=0 EndX=-3.00761 EndY=67.1743 EndZ=0
    g266: LineSegment StartX=-5 StartY=67 StartZ=0 EndX=-3.00761 EndY=66.8257 EndZ=0
    g267: LineSegment StartX=-3.00761 StartY=66.8257 StartZ=0 EndX=-3.00761 EndY=67.1743 EndZ=0
    g268: LineSegment [constr] StartX=-5 StartY=67 StartZ=0 EndX=-5 EndY=68 EndZ=0
    g269: LineSegment StartX=-5 StartY=68 StartZ=0 EndX=-3.00761 EndY=68.1743 EndZ=0
    g270: LineSegment StartX=-5 StartY=68 StartZ=0 EndX=-3.00761 EndY=67.8257 EndZ=0
    g271: LineSegment StartX=-3.00761 StartY=67.8257 StartZ=0 EndX=-3.00761 EndY=68.1743 EndZ=0
    g272: LineSegment [constr] StartX=-5 StartY=68 StartZ=0 EndX=-5 EndY=69 EndZ=0
    g273: LineSegment StartX=-5 StartY=69 StartZ=0 EndX=-3.00761 EndY=69.1743 EndZ=0
    g274: LineSegment StartX=-5 StartY=69 StartZ=0 EndX=-3.00761 EndY=68.8257 EndZ=0
    g275: LineSegment StartX=-3.00761 StartY=68.8257 StartZ=0 EndX=-3.00761 EndY=69.1743 EndZ=0
    g276: LineSegment [constr] StartX=-5 StartY=69 StartZ=0 EndX=-5 EndY=70 EndZ=0
    g277: LineSegment StartX=-5 StartY=70 StartZ=0 EndX=-3.00761 EndY=70.1743 EndZ=0
    g278: LineSegment StartX=-5 StartY=70 StartZ=0 EndX=-3.00761 EndY=69.8257 EndZ=0
    g279: LineSegment StartX=-3.00761 StartY=69.8257 StartZ=0 EndX=-3.00761 EndY=70.1743 EndZ=0
    g280: LineSegment [constr] StartX=-5 StartY=70 StartZ=0 EndX=-5 EndY=71 EndZ=0
    g281: LineSegment StartX=-5 StartY=71 StartZ=0 EndX=-3.00761 EndY=71.1743 EndZ=0
    g282: LineSegment StartX=-5 StartY=71 StartZ=0 EndX=-3.00761 EndY=70.8257 EndZ=0
    g283: LineSegment StartX=-3.00761 StartY=70.8257 StartZ=0 EndX=-3.00761 EndY=71.1743 EndZ=0
    g284: LineSegment [constr] StartX=-5 StartY=71 StartZ=0 EndX=-5 EndY=72 EndZ=0
    g285: LineSegment StartX=-5 StartY=72 StartZ=0 EndX=-3.00761 EndY=72.1743 EndZ=0
    g286: LineSegment StartX=-5 StartY=72 StartZ=0 EndX=-3.00761 EndY=71.8257 EndZ=0
    g287: LineSegment StartX=-3.00761 StartY=71.8257 StartZ=0 EndX=-3.00761 EndY=72.1743 EndZ=0
    g288: LineSegment [constr] StartX=-5 StartY=72 StartZ=0 EndX=-5 EndY=73 EndZ=0
    g289: LineSegment StartX=-5 StartY=73 StartZ=0 EndX=-3.00761 EndY=73.1743 EndZ=0
    g290: LineSegment StartX=-5 StartY=73 StartZ=0 EndX=-3.00761 EndY=72.8257 EndZ=0
    g291: LineSegment StartX=-3.00761 StartY=72.8257 StartZ=0 EndX=-3.00761 EndY=73.1743 EndZ=0
    g292: LineSegment [constr] StartX=-5 StartY=73 StartZ=0 EndX=-5 EndY=74 EndZ=0
    g293: LineSegment StartX=-5 StartY=74 StartZ=0 EndX=-3.00761 EndY=74.1743 EndZ=0
    g294: LineSegment StartX=-5 StartY=74 StartZ=0 EndX=-3.00761 EndY=73.8257 EndZ=0
    g295: LineSegment StartX=-3.00761 StartY=73.8257 StartZ=0 EndX=-3.00761 EndY=74.1743 EndZ=0
    g296: LineSegment [constr] StartX=-5 StartY=74 StartZ=0 EndX=-5 EndY=75 EndZ=0
    g297: LineSegment StartX=-5 StartY=75 StartZ=0 EndX=-3.00761 EndY=75.1743 EndZ=0
    g298: LineSegment StartX=-5 StartY=75 StartZ=0 EndX=-3.00761 EndY=74.8257 EndZ=0
    g299: LineSegment StartX=-3.00761 StartY=74.8257 StartZ=0 EndX=-3.00761 EndY=75.1743 EndZ=0
    g300: LineSegment [constr] StartX=-5 StartY=75 StartZ=0 EndX=-5 EndY=76 EndZ=0
    g301: LineSegment StartX=-5 StartY=76 StartZ=0 EndX=-3.00761 EndY=76.1743 EndZ=0
    g302: LineSegment StartX=-5 StartY=76 StartZ=0 EndX=-3.00761 EndY=75.8257 EndZ=0
    g303: LineSegment StartX=-3.00761 StartY=75.8257 StartZ=0 EndX=-3.00761 EndY=76.1743 EndZ=0
    g304: LineSegment [constr] StartX=-5 StartY=76 StartZ=0 EndX=-5 EndY=77 EndZ=0
    g305: LineSegment StartX=-5 StartY=77 StartZ=0 EndX=-3.00761 EndY=77.1743 EndZ=0
    g306: LineSegment StartX=-5 StartY=77 StartZ=0 EndX=-3.00761 EndY=76.8257 EndZ=0
    g307: LineSegment StartX=-3.00761 StartY=76.8257 StartZ=0 EndX=-3.00761 EndY=77.1743 EndZ=0
    g308: LineSegment [constr] StartX=-5 StartY=77 StartZ=0 EndX=-5 EndY=78 EndZ=0
    g309: LineSegment StartX=-5 StartY=78 StartZ=0 EndX=-3.00761 EndY=78.1743 EndZ=0
    g310: LineSegment StartX=-5 StartY=78 StartZ=0 EndX=-3.00761 EndY=77.8257 EndZ=0
    g311: LineSegment StartX=-3.00761 StartY=77.8257 StartZ=0 EndX=-3.00761 EndY=78.1743 EndZ=0
    g312: LineSegment [constr] StartX=-5 StartY=78 StartZ=0 EndX=-5 EndY=79 EndZ=0
    g313: LineSegment StartX=-5 StartY=79 StartZ=0 EndX=-3.00761 EndY=79.1743 EndZ=0
    g314: LineSegment StartX=-5 StartY=79 StartZ=0 EndX=-3.00761 EndY=78.8257 EndZ=0
    g315: LineSegment StartX=-3.00761 StartY=78.8257 StartZ=0 EndX=-3.00761 EndY=79.1743 EndZ=0
    g316: LineSegment [constr] StartX=-5 StartY=79 StartZ=0 EndX=-5 EndY=80 EndZ=0
    g317: LineSegment StartX=-5 StartY=80 StartZ=0 EndX=-3.00761 EndY=80.1743 EndZ=0
    g318: LineSegment StartX=-5 StartY=80 StartZ=0 EndX=-3.00761 EndY=79.8257 EndZ=0
    g319: LineSegment StartX=-3.00761 StartY=79.8257 StartZ=0 EndX=-3.00761 EndY=80.1743 EndZ=0
    g320: LineSegment [constr] StartX=-5 StartY=80 StartZ=0 EndX=-5 EndY=81 EndZ=0
    g321: LineSegment StartX=-5 StartY=81 StartZ=0 EndX=-3.00761 EndY=81.1743 EndZ=0
    g322: LineSegment StartX=-5 StartY=81 StartZ=0 EndX=-3.00761 EndY=80.8257 EndZ=0
    g323: LineSegment StartX=-3.00761 StartY=80.8257 StartZ=0 EndX=-3.00761 EndY=81.1743 EndZ=0
    g324: LineSegment [constr] StartX=-5 StartY=81 StartZ=0 EndX=-5 EndY=82 EndZ=0
    g325: LineSegment StartX=-5 StartY=82 StartZ=0 EndX=-3.00761 EndY=82.1743 EndZ=0
    g326: LineSegment StartX=-5 StartY=82 StartZ=0 EndX=-3.00761 EndY=81.8257 EndZ=0
    g327: LineSegment StartX=-3.00761 StartY=81.8257 StartZ=0 EndX=-3.00761 EndY=82.1743 EndZ=0
    g328: LineSegment [constr] StartX=-5 StartY=82 StartZ=0 EndX=-5 EndY=83 EndZ=0
    g329: LineSegment StartX=-5 StartY=83 StartZ=0 EndX=-3.00761 EndY=83.1743 EndZ=0
    g330: LineSegment StartX=-5 StartY=83 StartZ=0 EndX=-3.00761 EndY=82.8257 EndZ=0
    g331: LineSegment StartX=-3.00761 StartY=82.8257 StartZ=0 EndX=-3.00761 EndY=83.1743 EndZ=0
  constraints (339):
    c: Distance(g0) = 1
    c: Coincident(g0,g-4)
    c: PointOnObject(g0,g-3)
    c: Distance(g1) = 2
    c: Angle(g-1,g1) = 0.0872665
    c: Coincident(g1,g0)
    c: Distance(g2) = 2
    c: Angle(g-1,g2) = -0.0872665
    c: Coincident(g2,g0)
    c: Coincident(g3,g2)
    c: Coincident(g3,g1)
    c: Coincident(g5,g4)
    c: Coincident(g9,g8)
    c: Coincident(g13,g12)
    c: Coincident(g17,g16)
    c: Coincident(g21,g20)
    c: Coincident(g25,g24)
    c: Coincident(g29,g28)
    c: Coincident(g33,g32)
    c: Coincident(g37,g36)
    c: Coincident(g41,g40)
    c: Coincident(g45,g44)
    c: Coincident(g49,g48)
    c: Coincident(g53,g52)
    c: Coincident(g57,g56)
    c: Coincident(g61,g60)
    c: Coincident(g65,g64)
    c: Coincident(g69,g68)
    c: Coincident(g73,g72)
    c: Coincident(g77,g76)
    c: Coincident(g81,g80)
    c: Coincident(g85,g84)
    c: Coincident(g89,g88)
    c: Coincident(g93,g92)
    c: Coincident(g97,g96)
    c: Coincident(g101,g100)
    c: Coincident(g105,g104)
    c: Coincident(g109,g108)
    c: Coincident(g113,g112)
    c: Coincident(g117,g116)
    c: Coincident(g121,g120)
    c: Coincident(g125,g124)
    c: Coincident(g129,g128)
    c: Coincident(g133,g132)
    c: Coincident(g137,g136)
    c: Coincident(g141,g140)
    c: Coincident(g145,g144)
    c: Coincident(g149,g148)
    c: Coincident(g153,g152)
    c: Coincident(g157,g156)
    c: Coincident(g161,g160)
    c: Coincident(g165,g164)
    c: Coincident(g169,g168)
    c: Coincident(g173,g172)
    c: Coincident(g177,g176)
    c: Coincident(g181,g180)
    c: Coincident(g185,g184)
    c: Coincident(g189,g188)
    c: Coincident(g193,g192)
    c: Coincident(g197,g196)
    c: Coincident(g201,g200)
    c: Coincident(g205,g204)
    c: Coincident(g209,g208)
    c: Coincident(g213,g212)
    c: Coincident(g217,g216)
    c: Coincident(g221,g220)
    c: Coincident(g225,g224)
    c: Coincident(g229,g228)
    c: Coincident(g233,g232)
    c: Coincident(g237,g236)
    c: Coincident(g241,g240)
    c: Coincident(g245,g244)
    c: Coincident(g249,g248)
    c: Coincident(g253,g252)
    c: Coincident(g257,g256)
    c: Coincident(g261,g260)
    c: Coincident(g265,g264)
    c: Coincident(g269,g268)
    c: Coincident(g273,g272)
    c: Coincident(g277,g276)
    c: Coincident(g281,g280)
    c: Coincident(g285,g284)
    c: Coincident(g289,g288)
    c: Coincident(g293,g292)
    c: Coincident(g297,g296)
    c: Coincident(g301,g300)
    c: Coincident(g305,g304)
    c: Coincident(g309,g308)
    c: Coincident(g313,g312)
    c: Coincident(g317,g316)
    c: Coincident(g321,g320)
    c: Coincident(g325,g324)
    c: Coincident(g329,g328)
    c: Coincident(g6,g4)
    c: Coincident(g10,g8)
    c: Coincident(g14,g12)
    c: Coincident(g18,g16)
    c: Coincident(g22,g20)
    c: Coincident(g26,g24)
    c: Coincident(g30,g28)
    c: Coincident(g34,g32)
    c: Coincident(g38,g36)
    c: Coincident(g42,g40)
    c: Coincident(g46,g44)
    c: Coincident(g50,g48)
    c: Coincident(g54,g52)
    c: Coincident(g58,g56)
    c: Coincident(g62,g60)
    c: Coincident(g66,g64)
    c: Coincident(g70,g68)
    c: Coincident(g74,g72)
    c: Coincident(g78,g76)
    c: Coincident(g82,g80)
    c: Coincident(g86,g84)
    c: Coincident(g90,g88)
    c: Coincident(g94,g92)
    c: Coincident(g98,g96)
    c: Coincident(g102,g100)
    c: Coincident(g106,g104)
    c: Coincident(g110,g108)
    c: Coincident(g114,g112)
    c: Coincident(g118,g116)
    c: Coincident(g122,g120)
    c: Coincident(g126,g124)
    c: Coincident(g130,g128)
    c: Coincident(g134,g132)
    c: Coincident(g138,g136)
    c: Coincident(g142,g140)
    c: Coincident(g146,g144)
    c: Coincident(g150,g148)
    c: Coincident(g154,g152)
    c: Coincident(g158,g156)
    c: Coincident(g162,g160)
    c: Coincident(g166,g164)
    c: Coincident(g170,g168)
    c: Coincident(g174,g172)
    c: Coincident(g178,g176)
    c: Coincident(g182,g180)
    c: Coincident(g186,g184)
    c: Coincident(g190,g188)
    c: Coincident(g194,g192)
    c: Coincident(g198,g196)
    c: Coincident(g202,g200)
    c: Coincident(g206,g204)
    c: Coincident(g210,g208)
    c: Coincident(g214,g212)
    c: Coincident(g218,g216)
    c: Coincident(g222,g220)
    c: Coincident(g226,g224)
    c: Coincident(g230,g228)
    c: Coincident(g234,g232)
    c: Coincident(g238,g236)
    c: Coincident(g242,g240)
    c: Coincident(g246,g244)
    c: Coincident(g250,g248)
    c: Coincident(g254,g252)
    c: Coincident(g258,g256)
    c: Coincident(g262,g260)
    c: Coincident(g266,g264)
    c: Coincident(g270,g268)
    c: Coincident(g274,g272)
    c: Coincident(g278,g276)
    c: Coincident(g282,g280)
    c: Coincident(g286,g284)
    c: Coincident(g290,g288)
    c: Coincident(g294,g292)
    c: Coincident(g298,g296)
    c: Coincident(g302,g300)
    c: Coincident(g306,g304)
    c: Coincident(g310,g308)
    c: Coincident(g314,g312)
    c: Coincident(g318,g316)
    c: Coincident(g322,g320)
    c: Coincident(g326,g324)
    c: Coincident(g330,g328)
    c: Coincident(g7,g6)
    c: Coincident(g11,g10)
    c: Coincident(g15,g14)
    c: Coincident(g19,g18)
    c: Coincident(g23,g22)
    c: Coincident(g27,g26)
    c: Coincident(g31,g30)
    c: Coincident(g35,g34)
    c: Coincident(g39,g38)
    c: Coincident(g43,g42)
    c: Coincident(g47,g46)
    c: Coincident(g51,g50)
    c: Coincident(g55,g54)
    c: Coincident(g59,g58)
    c: Coincident(g63,g62)
    c: Coincident(g67,g66)
    c: Coincident(g71,g70)
    c: Coincident(g75,g74)
    c: Coincident(g79,g78)
    c: Coincident(g83,g82)
    c: Coincident(g87,g86)
    c: Coincident(g91,g90)
    c: Coincident(g95,g94)
    c: Coincident(g99,g98)
    c: Coincident(g103,g102)
    c: Coincident(g107,g106)
    c: Coincident(g111,g110)
    c: Coincident(g115,g114)
    c: Coincident(g119,g118)
    c: Coincident(g123,g122)
    c: Coincident(g127,g126)
    c: Coincident(g131,g130)
    c: Coincident(g135,g134)
    c: Coincident(g139,g138)
    c: Coincident(g143,g142)
    c: Coincident(g147,g146)
    c: Coincident(g151,g150)
    c: Coincident(g155,g154)
    c: Coincident(g159,g158)
    c: Coincident(g163,g162)
    c: Coincident(g167,g166)
    c: Coincident(g171,g170)
    c: Coincident(g175,g174)
    c: Coincident(g179,g178)
    c: Coincident(g183,g182)
    c: Coincident(g187,g186)
    c: Coincident(g191,g190)
    c: Coincident(g195,g194)
    c: Coincident(g199,g198)
    c: Coincident(g203,g202)
    c: Coincident(g207,g206)
    c: Coincident(g211,g210)
    c: Coincident(g215,g214)
    c: Coincident(g219,g218)
    c: Coincident(g223,g222)
    c: Coincident(g227,g226)
    c: Coincident(g231,g230)
    c: Coincident(g235,g234)
    c: Coincident(g239,g238)
    c: Coincident(g243,g242)
    c: Coincident(g247,g246)
    c: Coincident(g251,g250)
    c: Coincident(g255,g254)
    c: Coincident(g259,g258)
    c: Coincident(g263,g262)
    c: Coincident(g267,g266)
    c: Coincident(g271,g270)
    c: Coincident(g275,g274)
    c: Coincident(g279,g278)
    c: Coincident(g283,g282)
    c: Coincident(g287,g286)
    c: Coincident(g291,g290)
    c: Coincident(g295,g294)
    c: Coincident(g299,g298)
    c: Coincident(g303,g302)
    c: Coincident(g307,g306)
    c: Coincident(g311,g310)
    c: Coincident(g315,g314)
    c: Coincident(g319,g318)
    c: Coincident(g323,g322)
    c: Coincident(g327,g326)
    c: Coincident(g331,g330)
    c: Coincident(g7,g5)
    c: Coincident(g11,g9)
    c: Coincident(g15,g13)
    c: Coincident(g19,g17)
    c: Coincident(g23,g21)
    c: Coincident(g27,g25)
    c: Coincident(g31,g29)
    c: Coincident(g35,g33)
    c: Coincident(g39,g37)
    c: Coincident(g43,g41)
    c: Coincident(g47,g45)
    c: Coincident(g51,g49)
    c: Coincident(g55,g53)
    c: Coincident(g59,g57)
    c: Coincident(g63,g61)
    c: Coincident(g67,g65)
    c: Coincident(g71,g69)
    c: Coincident(g75,g73)
    c: Coincident(g79,g77)
    c: Coincident(g83,g81)
    c: Coincident(g87,g85)
    c: Coincident(g91,g89)
    c: Coincident(g95,g93)
    c: Coincident(g99,g97)
    c: Coincident(g103,g101)
    c: Coincident(g107,g105)
    c: Coincident(g111,g109)
    c: Coincident(g115,g113)
    c: Coincident(g119,g117)
    c: Coincident(g123,g121)
    c: Coincident(g127,g125)
    c: Coincident(g131,g129)
    c: Coincident(g135,g133)
    c: Coincident(g139,g137)
    c: Coincident(g143,g141)
    c: Coincident(g147,g145)
    c: Coincident(g151,g149)
    c: Coincident(g155,g153)
    c: Coincident(g159,g157)
    c: Coincident(g163,g161)
    c: Coincident(g167,g165)
    c: Coincident(g171,g169)
    c: Coincident(g175,g173)
    c: Coincident(g179,g177)
    c: Coincident(g183,g181)
    c: Coincident(g187,g185)
    c: Coincident(g191,g189)
    c: Coincident(g195,g193)
    c: Coincident(g199,g197)
    c: Coincident(g203,g201)
    c: Coincident(g207,g205)
    c: Coincident(g211,g209)
    c: Coincident(g215,g213)
    c: Coincident(g219,g217)
    c: Coincident(g223,g221)
    c: Coincident(g227,g225)
    c: Coincident(g231,g229)
    c: Coincident(g235,g233)
    c: Coincident(g239,g237)
    c: Coincident(g243,g241)
    c: Coincident(g247,g245)
    c: Coincident(g251,g249)
    c: Coincident(g255,g253)
    c: Coincident(g259,g257)
    c: Coincident(g263,g261)
    c: Coincident(g267,g265)
    c: Coincident(g271,g269)
    c: Coincident(g275,g273)
    c: Coincident(g279,g277)
    c: Coincident(g283,g281)
    c: Coincident(g287,g285)
    c: Coincident(g291,g289)
    c: Coincident(g295,g293)
    c: Coincident(g299,g297)
    c: Coincident(g303,g301)
    c: Coincident(g307,g305)
    c: Coincident(g311,g309)
    c: Coincident(g315,g313)
    c: Coincident(g319,g317)
    c: Coincident(g323,g321)
    c: Coincident(g327,g325)
    c: Coincident(g331,g329)
FEATURE [PartDesign::Pocket] Pocket016
  BaseFeature = -> Fillet005
  Direction = (1,0,2e-16)
  Length = 0.5
  Length2 = 5
  Placement = pos=(0,0,0) rot=(1,0,0;1.5708rad)
  Profile = -> Sketch038
  ReferenceAxis = -> Sketch038 [N_Axis]
  Refine = true
  Suppressed = false
  Type = 0
FEATURE [PartDesign::Body] Body  label="Base2U"
  AllowCompound = false
  Group = -> [Sketch,Pad,Sketch001,Pad001,Sketch002,Hole,Sketch003,Pad002,DatumPlane,Sketch004,Pad003,DatumPlane001,Sketch005,Pad004,Chamfer,Chamfer001,Chamfer002,Chamfer003,Chamfer004,Chamfer005,Chamfer006,Chamfer007,Chamfer008,Chamfer009,Chamfer010,Chamfer011,Chamfer012,Fillet,Sketch027,Pad015,Fillet005,Sketch038,Pocket016]
  Origin = -> Origin
  Tip = -> Pocket016
FEATURE [PartDesign::FeatureBase] Clone001
  BaseFeature = -> Body
  Suppressed = false
FEATURE [Sketcher::SketchObject] Sketch028
  ArcFitTolerance = 1e-06
  AttachmentSupport = -> [Clone001]
  ExternalGeometry = -> [Clone001]
  FullyConstrained = true
  MakeInternals = false
  MapMode = 5
  Placement = pos=(0,1.7e-15,0) rot=(0,0.707107,0.707107;3.14159rad)
  sketch-geometry (4):
    g0: LineSegment StartX=-84 StartY=0 StartZ=0 EndX=-84 EndY=-7 EndZ=0
    g1: LineSegment StartX=-84 StartY=-7 StartZ=0 EndX=0 EndY=-7 EndZ=0
    g2: LineSegment StartX=0 StartY=-7 StartZ=0 EndX=0 EndY=0 EndZ=0
    g3: LineSegment StartX=0 StartY=0 StartZ=0 EndX=-84 EndY=0 EndZ=0
  constraints (11):
    c: Coincident(g0,g1)
    c: Coincident(g1,g2)
    c: Coincident(g2,g3)
    c: Coincident(g3,g0)
    c: Vertical(g0)
    c: Vertical(g2)
    c: Horizontal(g1)
    c: Horizontal(g3)
    c: Distance(g1,g3) = 7
    c: Coincident(g0,g-4)
    c: PointOnObject(g1,g-2)
FEATURE [PartDesign::Pocket] Pocket009
  BaseFeature = -> Clone001
  Direction = (0,-1,2e-16)
  Length = 5
  Length2 = 5
  Profile = -> Sketch028
  ReferenceAxis = -> Sketch028 [N_Axis]
  Refine = true
  Suppressed = false
  Type = 1
FEATURE [Sketcher::SketchObject] Sketch029
  ArcFitTolerance = 1e-06
  AttachmentSupport = -> [Pocket009]
  ExternalGeometry = -> [Pocket009]
  FullyConstrained = true
  MakeInternals = false
  MapMode = 5
  Placement = pos=(0,0,-5e-16) rot=(1,0,0;3.14159rad)
  sketch-geometry (20):
    g0: LineSegment [constr] StartX=0 StartY=84 StartZ=0 EndX=0 EndY=79 EndZ=0
    g1: LineSegment [constr] StartX=0 StartY=79 StartZ=0 EndX=5 EndY=79 EndZ=0
    g2: LineSegment [constr] StartX=5 StartY=79 StartZ=0 EndX=5 EndY=84 EndZ=0
    g3: LineSegment [constr] StartX=5 StartY=84 StartZ=0 EndX=0 EndY=84 EndZ=0
    g4: LineSegment [constr] StartX=0 StartY=0 StartZ=0 EndX=5 EndY=0 EndZ=0
    g5: LineSegment [constr] StartX=5 StartY=0 StartZ=0 EndX=5 EndY=5 EndZ=0
    g6: LineSegment [constr] StartX=5 StartY=5 StartZ=0 EndX=0 EndY=5 EndZ=0
    g7: LineSegment [constr] StartX=0 StartY=5 StartZ=0 EndX=0 EndY=0 EndZ=0
    g8: LineSegment [constr] StartX=84 StartY=0 StartZ=0 EndX=84 EndY=5 EndZ=0
    g9: LineSegment [constr] StartX=84 StartY=5 StartZ=0 EndX=79 EndY=5 EndZ=0
    g10: LineSegment [constr] StartX=79 StartY=5 StartZ=0 EndX=79 EndY=0 EndZ=0
    g11: LineSegment [constr] StartX=79 StartY=0 StartZ=0 EndX=84 EndY=0 EndZ=0
    g12: LineSegment [constr] StartX=84 StartY=84 StartZ=0 EndX=79 EndY=84 EndZ=0
    g13: LineSegment [constr] StartX=79 StartY=84 StartZ=0 EndX=79 EndY=79 EndZ=0
    g14: LineSegment [constr] StartX=79 StartY=79 StartZ=0 EndX=84 EndY=79 EndZ=0
    g15: LineSegment [constr] StartX=84 StartY=79 StartZ=0 EndX=84 EndY=84 EndZ=0
    g16: Circle CenterX=5 CenterY=79 CenterZ=0 NormalX=0 NormalY=0 NormalZ=1 AngleXU=0 Radius=1.5
    g17: Circle CenterX=5 CenterY=5 CenterZ=0 NormalX=0 NormalY=0 NormalZ=1 AngleXU=0 Radius=1.5
    g18: Circle CenterX=79 CenterY=5 CenterZ=0 NormalX=0 NormalY=0 NormalZ=1 AngleXU=0 Radius=1.5
    g19: Circle CenterX=79 CenterY=79 CenterZ=0 NormalX=0 NormalY=0 NormalZ=1 AngleXU=0 Radius=1.5
  constraints (52):
    c: Coincident(g0,g1)
    c: Coincident(g1,g2)
    c: Coincident(g2,g3)
    c: Coincident(g3,g0)
    c: Vertical(g0)
    c: Vertical(g2)
    c: Horizontal(g1)
    c: Horizontal(g3)
    c: Distance(g0,g2) = 5
    c: Distance(g1,g3) = 5
    c: Coincident(g0,g-4)
    c: Coincident(g4,g5)
    c: Coincident(g5,g6)
    c: Coincident(g6,g7)
    c: Coincident(g7,g4)
    c: Horizontal(g4)
    c: Horizontal(g6)
    c: Vertical(g5)
    c: Vertical(g7)
    c: Distance(g5,g7) = 5
    c: Distance(g4,g6) = 5
    c: Coincident(g4,g-1)
    c: Coincident(g8,g9)
    c: Coincident(g9,g10)
    c: Coincident(g10,g11)
    c: Coincident(g11,g8)
    c: Vertical(g8)
    c: Vertical(g10)
    c: Horizontal(g9)
    c: Horizontal(g11)
    c: Distance(g8,g10) = 5
    c: Distance(g9,g11) = 5
    c: Coincident(g8,g-6)
    c: Coincident(g12,g13)
    c: Coincident(g13,g14)
    c: Coincident(g14,g15)
    c: Coincident(g15,g12)
    c: Horizontal(g12)
    c: Horizontal(g14)
    c: Vertical(g13)
    c: Vertical(g15)
    c: Distance(g13,g15) = 5
    c: Distance(g12,g14) = 5
    c: Coincident(g12,g-6)
    c: Diameter(g16) = 3
    c: Coincident(g16,g1)
    c: Diameter(g17) = 3
    c: Coincident(g17,g5)
    c: Diameter(g18) = 3
    c: Coincident(g18,g9)
    c: Diameter(g19) = 3
    c: Coincident(g19,g13)
FEATURE [PartDesign::Pocket] Pocket010
  BaseFeature = -> Pocket009
  Direction = (0,0,1)
  Length = 4
  Length2 = 5
  Profile = -> Sketch029
  ReferenceAxis = -> Sketch029 [N_Axis]
  Refine = true
  Suppressed = false
  Type = 0
FEATURE [Sketcher::SketchObject] Sketch039
  ArcFitTolerance = 1e-06
  AttachmentSupport = -> [Pocket015]
  ExternalGeometry = -> [Pocket015]
  FullyConstrained = false
  MakeInternals = false
  MapMode = 5
  Placement = pos=(-1.2282e-09,-84,2e-15) rot=(-0.707107,0,0.707107;3.14159rad)
  sketch-geometry (68):
    g0: LineSegment [constr] StartX=-5.35355 StartY=-84 StartZ=0 EndX=-5.35355 EndY=-75 EndZ=0
    g1: LineSegment StartX=-5.35355 StartY=-75 StartZ=0 EndX=-7.34594 EndY=-74.8257 EndZ=0
    g2: LineSegment StartX=-5.35355 StartY=-75 StartZ=0 EndX=-7.34594 EndY=-75.1743 EndZ=0
    g3: LineSegment StartX=-7.34594 StartY=-75.1743 StartZ=0 EndX=-7.34594 EndY=-74.8257 EndZ=0
    g4: LineSegment StartX=-5.35355 StartY=-75.9 StartZ=0 EndX=-7.34594 EndY=-75.7257 EndZ=0
    g5: LineSegment StartX=-5.35355 StartY=-75.9 StartZ=0 EndX=-7.34594 EndY=-76.0743 EndZ=0
    g6: LineSegment StartX=-7.34594 StartY=-76.0743 StartZ=0 EndX=-7.34594 EndY=-75.7257 EndZ=0
    g7: LineSegment StartX=-5.35355 StartY=-76.8 StartZ=0 EndX=-7.34594 EndY=-76.6257 EndZ=0
    g8: LineSegment StartX=-5.35355 StartY=-76.8 StartZ=0 EndX=-7.34594 EndY=-76.9743 EndZ=0
    g9: LineSegment StartX=-7.34594 StartY=-76.9743 StartZ=0 EndX=-7.34594 EndY=-76.6257 EndZ=0
    g10: LineSegment StartX=-5.35355 StartY=-77.7 StartZ=0 EndX=-7.34594 EndY=-77.5257 EndZ=0
    g11: LineSegment StartX=-5.35355 StartY=-77.7 StartZ=0 EndX=-7.34594 EndY=-77.8743 EndZ=0
    g12: LineSegment StartX=-7.34594 StartY=-77.8743 StartZ=0 EndX=-7.34594 EndY=-77.5257 EndZ=0
    g13: LineSegment StartX=-5.35355 StartY=-78.6 StartZ=0 EndX=-7.34594 EndY=-78.4257 EndZ=0
    g14: LineSegment StartX=-5.35355 StartY=-78.6 StartZ=0 EndX=-7.34594 EndY=-78.7743 EndZ=0
    g15: LineSegment StartX=-7.34594 StartY=-78.7743 StartZ=0 EndX=-7.34594 EndY=-78.4257 EndZ=0
    g16: LineSegment StartX=-5.35355 StartY=-79.5 StartZ=0 EndX=-7.34594 EndY=-79.3257 EndZ=0
    g17: LineSegment StartX=-5.35355 StartY=-79.5 StartZ=0 EndX=-7.34594 EndY=-79.6743 EndZ=0
    g18: LineSegment StartX=-7.34594 StartY=-79.6743 StartZ=0 EndX=-7.34594 EndY=-79.3257 EndZ=0
    g19: LineSegment StartX=-5.35355 StartY=-80.4 StartZ=0 EndX=-7.34594 EndY=-80.2257 EndZ=0
    g20: LineSegment StartX=-5.35355 StartY=-80.4 StartZ=0 EndX=-7.34594 EndY=-80.5743 EndZ=0
    g21: LineSegment StartX=-7.34594 StartY=-80.5743 StartZ=0 EndX=-7.34594 EndY=-80.2257 EndZ=0
    g22: LineSegment StartX=-5.35355 StartY=-81.3 StartZ=0 EndX=-7.34594 EndY=-81.1257 EndZ=0
    g23: LineSegment StartX=-5.35355 StartY=-81.3 StartZ=0 EndX=-7.34594 EndY=-81.4743 EndZ=0
    g24: LineSegment StartX=-7.34594 StartY=-81.4743 StartZ=0 EndX=-7.34594 EndY=-81.1257 EndZ=0
    g25: LineSegment StartX=-5.35355 StartY=-82.2 StartZ=0 EndX=-7.34594 EndY=-82.0257 EndZ=0
    g26: LineSegment StartX=-5.35355 StartY=-82.2 StartZ=0 EndX=-7.34594 EndY=-82.3743 EndZ=0
    g27: LineSegment StartX=-7.34594 StartY=-82.3743 StartZ=0 EndX=-7.34594 EndY=-82.0257 EndZ=0
    g28: LineSegment StartX=-5.35355 StartY=-83.1 StartZ=0 EndX=-7.34594 EndY=-82.9257 EndZ=0
    g29: LineSegment StartX=-5.35355 StartY=-83.1 StartZ=0 EndX=-7.34594 EndY=-83.2743 EndZ=0
    g30: LineSegment StartX=-7.34594 StartY=-83.2743 StartZ=0 EndX=-7.34594 EndY=-82.9257 EndZ=0
    g31: LineSegment [constr] StartX=-5.35355 StartY=0 StartZ=0 EndX=-5.35355 EndY=-9 EndZ=0
    g32: LineSegment StartX=-5.35355 StartY=-9 StartZ=0 EndX=-7.34594 EndY=-9.17431 EndZ=0
    g33: LineSegment StartX=-5.35355 StartY=-9 StartZ=0 EndX=-7.34594 EndY=-8.82569 EndZ=0
    g34: LineSegment StartX=-7.34594 StartY=-8.82569 StartZ=0 EndX=-7.34594 EndY=-9.17431 EndZ=0
    g35: LineSegment StartX=-5.35355 StartY=-8.1 StartZ=0 EndX=-7.34594 EndY=-8.27431 EndZ=0
    g36: LineSegment StartX=-5.35355 StartY=-8.1 StartZ=0 EndX=-7.34594 EndY=-7.92569 EndZ=0
    g37: LineSegment StartX=-7.34594 StartY=-7.92569 StartZ=0 EndX=-7.34594 EndY=-8.27431 EndZ=0
    g38: LineSegment StartX=-5.35355 StartY=-7.2 StartZ=0 EndX=-7.34594 EndY=-7.37431 EndZ=0
    g39: LineSegment StartX=-5.35355 StartY=-7.2 StartZ=0 EndX=-7.34594 EndY=-7.02569 EndZ=0
    g40: LineSegment StartX=-7.34594 StartY=-7.02569 StartZ=0 EndX=-7.34594 EndY=-7.37431 EndZ=0
    g41: LineSegment StartX=-5.35355 StartY=-6.3 StartZ=0 EndX=-7.34594 EndY=-6.47431 EndZ=0
    g42: LineSegment StartX=-5.35355 StartY=-6.3 StartZ=0 EndX=-7.34594 EndY=-6.12569 EndZ=0
    g43: LineSegment StartX=-7.34594 StartY=-6.12569 StartZ=0 EndX=-7.34594 EndY=-6.47431 EndZ=0
    g44: LineSegment StartX=-5.35355 StartY=-5.4 StartZ=0 EndX=-7.34594 EndY=-5.57431 EndZ=0
    g45: LineSegment StartX=-5.35355 StartY=-5.4 StartZ=0 EndX=-7.34594 EndY=-5.22569 EndZ=0
    g46: LineSegment StartX=-7.34594 StartY=-5.22569 StartZ=0 EndX=-7.34594 EndY=-5.57431 EndZ=0
    g47: LineSegment StartX=-5.35355 StartY=-4.5 StartZ=0 EndX=-7.34594 EndY=-4.67431 EndZ=0
    g48: LineSegment StartX=-5.35355 StartY=-4.5 StartZ=0 EndX=-7.34594 EndY=-4.32569 EndZ=0
    g49: LineSegment StartX=-7.34594 StartY=-4.32569 StartZ=0 EndX=-7.34594 EndY=-4.67431 EndZ=0
    g50: LineSegment StartX=-5.35355 StartY=-3.6 StartZ=0 EndX=-7.34594 EndY=-3.77431 EndZ=0
    g51: LineSegment StartX=-5.35355 StartY=-3.6 StartZ=0 EndX=-7.34594 EndY=-3.42569 EndZ=0
    g52: LineSegment StartX=-7.34594 StartY=-3.42569 StartZ=0 EndX=-7.34594 EndY=-3.77431 EndZ=0
    g53: LineSegment StartX=-5.35355 StartY=-2.7 StartZ=0 EndX=-7.34594 EndY=-2.87431 EndZ=0
    g54: LineSegment StartX=-5.35355 StartY=-2.7 StartZ=0 EndX=-7.34594 EndY=-2.52569 EndZ=0
    g55: LineSegment StartX=-7.34594 StartY=-2.52569 StartZ=0 EndX=-7.34594 EndY=-2.87431 EndZ=0
    g56: LineSegment StartX=-5.35355 StartY=-1.8 StartZ=0 EndX=-7.34594 EndY=-1.97431 EndZ=0
    g57: LineSegment StartX=-5.35355 StartY=-1.8 StartZ=0 EndX=-7.34594 EndY=-1.62569 EndZ=0
    g58: LineSegment StartX=-7.34594 StartY=-1.62569 StartZ=0 EndX=-7.34594 EndY=-1.97431 EndZ=0
    g59: LineSegment StartX=-5.35355 StartY=-0.9 StartZ=0 EndX=-7.34594 EndY=-1.07431 EndZ=0
    g60: LineSegment StartX=-5.35355 StartY=-0.9 StartZ=0 EndX=-7.34594 EndY=-0.725689 EndZ=0
    g61: LineSegment StartX=-7.34594 StartY=-0.725689 StartZ=0 EndX=-7.34594 EndY=-1.07431 EndZ=0
    g62: LineSegment StartX=-5.35355 StartY=-84 StartZ=0 EndX=-7.34594 EndY=-83.8257 EndZ=0
    g63: LineSegment StartX=-7.34594 StartY=-83.8257 StartZ=0 EndX=-7.34594 EndY=-84 EndZ=0
    g64: LineSegment StartX=-7.34594 StartY=-84 StartZ=0 EndX=-5.35355 EndY=-84 EndZ=0
    g65: LineSegment StartX=-5.35355 StartY=0 StartZ=0 EndX=-7.34594 EndY=-0.174312 EndZ=0
    g66: LineSegment StartX=-7.34594 StartY=-0.174312 StartZ=0 EndX=-7.34594 EndY=0 EndZ=0
    g67: LineSegment StartX=-7.34594 StartY=0 StartZ=0 EndX=-5.35355 EndY=0 EndZ=0
  constraints (74):
    c: Distance(g0) = 9
    c: Coincident(g0,g-4)
    c: PointOnObject(g0,g-3)
    c: Distance(g1) = 2
    c: Angle(g-1,g1) = 3.05433
    c: Coincident(g1,g0)
    c: Distance(g2) = 2
    c: Angle(g-1,g2) = -3.05433
    c: Coincident(g2,g0)
    c: Coincident(g3,g2)
    c: Coincident(g3,g1)
    c: Coincident(g6,g5)
    c: Coincident(g9,g8)
    c: Coincident(g12,g11)
    c: Coincident(g15,g14)
    c: Coincident(g18,g17)
    c: Coincident(g21,g20)
    c: Coincident(g24,g23)
    c: Coincident(g27,g26)
    c: Coincident(g30,g29)
    c: Coincident(g6,g4)
    c: Coincident(g9,g7)
    c: Coincident(g12,g10)
    c: Coincident(g15,g13)
    c: Coincident(g18,g16)
    c: Coincident(g21,g19)
    c: Coincident(g24,g22)
    c: Coincident(g27,g25)
    c: Coincident(g30,g28)
    c: Distance(g31) = 9
    c: Coincident(g31,g-3)
    c: PointOnObject(g31,g-3)
    c: Distance(g32) = 2
    c: Angle(g-1,g32) = -3.05433
    c: Coincident(g32,g31)
    c: Distance(g33) = 2
    c: Angle(g-1,g33) = 3.05433
    c: Coincident(g33,g31)
    c: Coincident(g34,g33)
    c: Coincident(g34,g32)
    c: Coincident(g37,g36)
    c: Coincident(g40,g39)
    c: Coincident(g43,g42)
    c: Coincident(g46,g45)
    c: Coincident(g49,g48)
    c: Coincident(g52,g51)
    c: Coincident(g55,g54)
    c: Coincident(g58,g57)
    c: Coincident(g61,g60)
    c: Coincident(g37,g35)
    c: Coincident(g40,g38)
    c: Coincident(g43,g41)
    c: Coincident(g46,g44)
    c: Coincident(g49,g47)
    c: Coincident(g52,g50)
    c: Coincident(g55,g53)
    c: Coincident(g58,g56)
    c: Coincident(g61,g59)
    c: Distance(g62) = 2
    c: Angle(g-1,g62) = 3.05433
    c: Coincident(g62,g0)
    c: Coincident(g63,g62)
    c: PointOnObject(g63,g-4)
    c: Vertical(g63)
    c: Coincident(g64,g63)
    c: Coincident(g64,g0)
    c: Distance(g65) = 2
    c: Angle(g-1,g65) = -3.05433
    c: Coincident(g65,g31)
    c: Coincident(g66,g65)
    c: Vertical(g66)
    c: Coincident(g67,g66)
    c: Coincident(g67,g31)
    c: Horizontal(g67)
FEATURE [PartDesign::Pocket] Pocket017
  BaseFeature = -> Pocket015
  Direction = (1,0,-2.14311e-10)
  Length = 0.5
  Length2 = 5
  Placement = pos=(0,-84,2e-15) rot=(1,0,0;1.5708rad)
  Profile = -> Sketch039
  ReferenceAxis = -> Sketch039 [N_Axis]
  Refine = true
  Suppressed = false
  Type = 0
FEATURE [Sketcher::SketchObject] Sketch040
  ArcFitTolerance = 1e-06
  AttachmentSupport = -> [Hole002]
  ExternalGeometry = -> [Hole002]
  FullyConstrained = true
  MakeInternals = false
  MapMode = 5
  Placement = pos=(3.7335e-08,0,9.85355) rot=(1,0,0;3.14159rad)
  sketch-geometry (4):
    g0: LineSegment StartX=38.7465 StartY=46.75 StartZ=0 EndX=38.7465 EndY=37.25 EndZ=0
    g1: LineSegment StartX=38.7465 StartY=37.25 StartZ=0 EndX=45.2465 EndY=37.25 EndZ=0
    g2: LineSegment StartX=45.2465 StartY=37.25 StartZ=0 EndX=45.2465 EndY=46.75 EndZ=0
    g3: LineSegment StartX=45.2465 StartY=46.75 StartZ=0 EndX=38.7465 EndY=46.75 EndZ=0
  constraints (10):
    c: Coincident(g0,g1)
    c: Coincident(g1,g2)
    c: Coincident(g2,g3)
    c: Coincident(g3,g0)
    c: Vertical(g0)
    c: Vertical(g2)
    c: Horizontal(g1)
    c: Horizontal(g3)
    c: Coincident(g0,g-5)
    c: Coincident(g1,g-6)
FEATURE [PartDesign::Pad] Pad019
  BaseFeature = -> Hole002
  Direction = (-3.78899e-09,0,-1)
  Length = 4.65
  Length2 = 10
  Profile = -> Sketch040
  ReferenceAxis = -> Sketch040 [N_Axis]
  Refine = true
  Suppressed = false
  Type = 0
FEATURE [PartDesign::Chamfer] Chamfer015
  Angle = 45
  Base = -> Pad019 [Edge6]
  BaseFeature = -> Pad019
  ChamferType = 0
  FlipDirection = false
  Refine = true
  Size = 4
  Size2 = 1
  SupportTransform = false
  Suppressed = false
  UseAllEdges = false
FEATURE [PartDesign::Chamfer] Chamfer016
  Angle = 45
  Base = -> Chamfer015 [Edge47]
  BaseFeature = -> Chamfer015
  ChamferType = 0
  FlipDirection = false
  Refine = true
  Size = 4
  Size2 = 1
  SupportTransform = false
  Suppressed = false
  UseAllEdges = false
FEATURE [Sketcher::SketchObject] Sketch041
  ArcFitTolerance = 1e-06
  AttachmentSupport = -> [Chamfer016]
  ExternalGeometry = -> [Chamfer016]
  FullyConstrained = true
  MakeInternals = false
  MapMode = 5
  Placement = pos=(0,-37.25,-2.38e-14) rot=(0,0.707107,0.707107;3.14159rad)
  sketch-geometry (4):
    g0: LineSegment StartX=-48.2465 StartY=20.8536 StartZ=0 EndX=-48.2465 EndY=6.85355 EndZ=0
    g1: LineSegment StartX=-48.2465 StartY=6.85355 StartZ=0 EndX=-46.2465 EndY=6.85355 EndZ=0
    g2: LineSegment StartX=-46.2465 StartY=6.85355 StartZ=0 EndX=-46.2465 EndY=20.8536 EndZ=0
    g3: LineSegment StartX=-46.2465 StartY=20.8536 StartZ=0 EndX=-48.2465 EndY=20.8536 EndZ=0
  constraints (11):
    c: Coincident(g0,g1)
    c: Coincident(g1,g2)
    c: Coincident(g2,g3)
    c: Coincident(g3,g0)
    c: Vertical(g0)
    c: Vertical(g2)
    c: Horizontal(g1)
    c: Horizontal(g3)
    c: Distance(g0,g2) = 2
    c: Distance(g1,g3) = 14
    c: Coincident(g0,g-11)
FEATURE [PartDesign::Pocket] Pocket018
  BaseFeature = -> Chamfer016
  Direction = (0,-1,2e-16)
  Length = 10
  Length2 = 5
  Profile = -> Sketch041
  ReferenceAxis = -> Sketch041 [N_Axis]
  Refine = true
  Suppressed = false
  Type = 0
FEATURE [Sketcher::SketchObject] Sketch043
  ArcFitTolerance = 1e-06
  AttachmentSupport = -> [Pocket018]
  ExternalGeometry = -> [Pocket018]
  FullyConstrained = true
  MakeInternals = false
  MapMode = 5
  Placement = pos=(0,-37.25,-2.38e-14) rot=(0,0.707107,0.707107;3.14159rad)
  sketch-geometry (4):
    g0: LineSegment StartX=-35.7465 StartY=20.8536 StartZ=0 EndX=-37.7465 EndY=20.8536 EndZ=0
    g1: LineSegment StartX=-37.7465 StartY=20.8536 StartZ=0 EndX=-37.7465 EndY=7.85355 EndZ=0
    g2: LineSegment StartX=-37.7465 StartY=7.85355 StartZ=0 EndX=-35.7465 EndY=7.85355 EndZ=0
    g3: LineSegment StartX=-35.7465 StartY=7.85355 StartZ=0 EndX=-35.7465 EndY=20.8536 EndZ=0
  constraints (11):
    c: Coincident(g0,g1)
    c: Coincident(g1,g2)
    c: Coincident(g2,g3)
    c: Coincident(g3,g0)
    c: Horizontal(g0)
    c: Horizontal(g2)
    c: Vertical(g1)
    c: Vertical(g3)
    c: Distance(g1,g3) = 2
    c: Distance(g0,g2) = 13
    c: Coincident(g0,g-4)
FEATURE [PartDesign::Pocket] Pocket019
  BaseFeature = -> Pocket018
  Direction = (0,-1,0)
  Length = 10
  Length2 = 5
  Profile = -> Sketch043
  ReferenceAxis = -> Sketch043 [N_Axis]
  Refine = true
  Suppressed = false
  Type = 0
FEATURE [Sketcher::SketchObject] Sketch044
  ArcFitTolerance = 1e-06
  AttachmentSupport = -> [Pocket019]
  ExternalGeometry = -> [Pocket019]
  FullyConstrained = true
  MakeInternals = false
  MapMode = 5
  Placement = pos=(0,-37.25,-2.38e-14) rot=(0,0.707107,0.707107;3.14159rad)
  sketch-geometry (4):
    g0: LineSegment StartX=-46.2465 StartY=20.8536 StartZ=0 EndX=-54.2465 EndY=20.8536 EndZ=0
    g1: LineSegment StartX=-54.2465 StartY=20.8536 StartZ=0 EndX=-54.2465 EndY=16.8536 EndZ=0
    g2: LineSegment StartX=-46.2465 StartY=8.26777 StartZ=0 EndX=-46.2465 EndY=20.8536 EndZ=0
    g3: LineSegment StartX=-54.2465 StartY=16.8536 StartZ=0 EndX=-46.2465 EndY=8.26777 EndZ=0
  constraints (10):
    c: Distance(g0) = 8
    c: Coincident(g0,g-4)
    c: Horizontal(g0)
    c: Distance(g1) = 4
    c: Coincident(g1,g0)
    c: Vertical(g1)
    c: Coincident(g2,g0)
    c: Coincident(g3,g1)
    c: Coincident(g3,g2)
    c: Coincident(g-4,g2)
FEATURE [PartDesign::Pad] Pad020
  BaseFeature = -> Pocket019
  Direction = (0,1,0)
  Length = 9.5
  Length2 = 10
  Profile = -> Sketch044
  ReferenceAxis = -> Sketch044 [N_Axis]
  Refine = true
  Reversed = true
  Suppressed = false
  Type = 0
FEATURE [Sketcher::SketchObject] Sketch045
  ArcFitTolerance = 1e-06
  AttachmentSupport = -> [Pad020]
  ExternalGeometry = -> [Pad020]
  FullyConstrained = true
  MakeInternals = false
  MapMode = 5
  Placement = pos=(2.68e-14,-37.25,0) rot=(0,0.707107,0.707107;3.14159rad)
  sketch-geometry (4):
    g0: LineSegment StartX=-37.7465 StartY=20.8536 StartZ=0 EndX=-29.7465 EndY=20.8536 EndZ=0
    g1: LineSegment StartX=-29.7465 StartY=20.8536 StartZ=0 EndX=-29.7465 EndY=16.8536 EndZ=0
    g2: LineSegment StartX=-29.7465 StartY=16.8536 StartZ=0 EndX=-37.7465 EndY=8.26777 EndZ=0
    g3: LineSegment StartX=-37.7465 StartY=8.26777 StartZ=0 EndX=-37.7465 EndY=20.8536 EndZ=0
  constraints (10):
    c: Distance(g0) = 8
    c: Coincident(g0,g-4)
    c: Horizontal(g0)
    c: Distance(g1) = 4
    c: Coincident(g1,g0)
    c: Vertical(g1)
    c: Coincident(g2,g1)
    c: Coincident(g2,g-6)
    c: Coincident(g3,g2)
    c: Coincident(g3,g0)
FEATURE [PartDesign::Pad] Pad021
  BaseFeature = -> Pad020
  Direction = (0,1,0)
  Length = 9.5
  Length2 = 10
  Profile = -> Sketch045
  ReferenceAxis = -> Sketch045 [N_Axis]
  Refine = true
  Reversed = true
  Suppressed = false
  Type = 0
FEATURE [Sketcher::SketchObject] Sketch046
  ArcFitTolerance = 1e-06
  AttachmentSupport = -> [Pad021]
  ExternalGeometry = -> [Pad021]
  FullyConstrained = true
  MakeInternals = false
  MapMode = 5
  Placement = pos=(8.12e-14,-37.25,-9.7e-15) rot=(0,0.707107,0.707107;3.14159rad)
  sketch-geometry (2):
    g0: GeomPoint [constr] X=-54.2465 Y=18.8536 Z=0
    g1: Circle CenterX=-54.2465 CenterY=18.8536 CenterZ=0 NormalX=0 NormalY=0 NormalZ=1 AngleXU=0 Radius=1
  constraints (3):
    c: Symmetric(g-3,g-3,g0)
    c: Diameter(g1) = 2
    c: Coincident(g1,g0)
FEATURE [PartDesign::Pocket] Pocket020
  BaseFeature = -> Pad021
  Direction = (0,-1,0)
  Length = 10
  Length2 = 5
  Profile = -> Sketch046
  ReferenceAxis = -> Sketch046 [N_Axis]
  Refine = true
  Suppressed = false
  Type = 0
FEATURE [Sketcher::SketchObject] Sketch047
  ArcFitTolerance = 1e-06
  AttachmentSupport = -> [Pocket020]
  ExternalGeometry = -> [Pocket020]
  FullyConstrained = true
  MakeInternals = false
  MapMode = 5
  Placement = pos=(8.12e-14,-37.25,-9.7e-15) rot=(0,0.707107,0.707107;3.14159rad)
  sketch-geometry (2):
    g0: GeomPoint X=-29.7465 Y=18.8536 Z=0
    g1: Circle CenterX=-29.7465 CenterY=18.8536 CenterZ=0 NormalX=0 NormalY=0 NormalZ=1 AngleXU=0 Radius=1
  constraints (3):
    c: Symmetric(g-3,g-3,g0)
    c: Diameter(g1) = 2
    c: Coincident(g1,g0)
FEATURE [PartDesign::Pocket] Pocket021
  BaseFeature = -> Pocket020
  Direction = (0,-1,0)
  Length = 11
  Length2 = 5
  Profile = -> Sketch047
  ReferenceAxis = -> Sketch047 [N_Axis]
  Refine = true
  Suppressed = false
  Type = 0
FEATURE [Sketcher::SketchObject] Sketch048
  ArcFitTolerance = 1e-06
  AttachmentSupport = -> [Pocket021]
  ExternalGeometry = -> [Pocket021]
  FullyConstrained = true
  MakeInternals = false
  MapMode = 5
  Placement = pos=(6.7647e-08,0,17.8536) rot=(0,0,1;0rad)
  sketch-geometry (1):
    g0: Circle CenterX=41.9965 CenterY=-42 CenterZ=0 NormalX=0 NormalY=0 NormalZ=1 AngleXU=0 Radius=1.35
  constraints (2):
    c: Coincident(g0,g-3)
    c: Equal(g0,g-3)
FEATURE [PartDesign::Pad] Pad022
  BaseFeature = -> Pocket021
  Direction = (0,0,1)
  Length = 3
  Length2 = 10
  Profile = -> Sketch048
  ReferenceAxis = -> Sketch048 [N_Axis]
  Refine = true
  Suppressed = false
  Type = 0
FEATURE [Sketcher::SketchObject] Sketch049
  ArcFitTolerance = 1e-06
  AttachmentSupport = -> [Pad022]
  ExternalGeometry = -> [Pad022]
  FullyConstrained = true
  MakeInternals = false
  MapMode = 5
  Placement = pos=(3.93837e-08,5.8e-15,20.8536) rot=(0,0,1;0rad)
  sketch-geometry (8):
    g0: GeomPoint X=33.7465 Y=-37.25 Z=0
    g1: GeomPoint X=33.7465 Y=-46.75 Z=0
    g2: GeomPoint X=50.2465 Y=-46.75 Z=0
    g3: GeomPoint X=50.2465 Y=-37.25 Z=0
    g4: LineSegment [constr] StartX=33.7465 StartY=-37.25 StartZ=0 EndX=33.7465 EndY=-46.75 EndZ=0
    g5: LineSegment [constr] StartX=50.2465 StartY=-37.25 StartZ=0 EndX=50.2465 EndY=-46.75 EndZ=0
    g6: Circle CenterX=33.7465 CenterY=-42 CenterZ=0 NormalX=0 NormalY=0 NormalZ=1 AngleXU=0 Radius=1.35
    g7: Circle CenterX=50.2465 CenterY=-42 CenterZ=0 NormalX=0 NormalY=0 NormalZ=1 AngleXU=0 Radius=1.35
  constraints (12):
    c: Symmetric(g-3,g-3,g0)
    c: Symmetric(g-6,g-6,g1)
    c: Symmetric(g-5,g-5,g2)
    c: Symmetric(g-4,g-4,g3)
    c: Coincident(g4,g0)
    c: Coincident(g4,g1)
    c: Coincident(g5,g3)
    c: Coincident(g5,g2)
    c: Diameter(g6) = 2.7
    c: Symmetric(g4,g4,g6)
    c: Diameter(g7) = 2.7
    c: Symmetric(g5,g5,g7)
FEATURE [PartDesign::Pocket] Pocket022
  BaseFeature = -> Pad022
  Direction = (-1.88858e-09,0,-1)
  Length = 13
  Length2 = 5
  Profile = -> Sketch049
  ReferenceAxis = -> Sketch049 [N_Axis]
  Refine = true
  Suppressed = false
  Type = 0
FEATURE [Sketcher::SketchObject] Sketch050
  ArcFitTolerance = 1e-06
  AttachmentSupport = -> [Pocket017]
  ExternalGeometry = -> [Pocket017]
  FullyConstrained = true
  MakeInternals = false
  MapMode = 5
  Placement = pos=(7.71195e-08,-84,20.3536) rot=(1,0,0;3.14159rad)
  sketch-geometry (10):
    g0: LineSegment [constr] StartX=35.4965 StartY=-37 StartZ=0 EndX=29.6465 EndY=-37 EndZ=0
    g1: LineSegment [constr] StartX=48.4965 StartY=-37 StartZ=0 EndX=54.3465 EndY=-37 EndZ=0
    g2: LineSegment StartX=29.6465 StartY=-37 StartZ=0 EndX=29.6465 EndY=-47 EndZ=0
    g3: LineSegment StartX=29.6465 StartY=-47 StartZ=0 EndX=35.4965 EndY=-47 EndZ=0
    g4: LineSegment StartX=35.4965 StartY=-47 StartZ=0 EndX=35.4965 EndY=-37 EndZ=0
    g5: LineSegment StartX=35.4965 StartY=-37 StartZ=0 EndX=29.6465 EndY=-37 EndZ=0
    g6: LineSegment StartX=54.3465 StartY=-37 StartZ=0 EndX=48.4965 EndY=-37 EndZ=0
    g7: LineSegment StartX=48.4965 StartY=-37 StartZ=0 EndX=48.4965 EndY=-47 EndZ=0
    g8: LineSegment StartX=48.4965 StartY=-47 StartZ=0 EndX=54.3465 EndY=-47 EndZ=0
    g9: LineSegment StartX=54.3465 StartY=-47 StartZ=0 EndX=54.3465 EndY=-37 EndZ=0
  constraints (26):
    c: Distance(g0) = 5.85
    c: Coincident(g0,g-4)
    c: Horizontal(g0)
    c: Distance(g1) = 5.85
    c: Coincident(g1,g-5)
    c: Horizontal(g1)
    c: Coincident(g2,g3)
    c: Coincident(g3,g4)
    c: Coincident(g4,g5)
    c: Coincident(g5,g2)
    c: Vertical(g2)
    c: Vertical(g4)
    c: Horizontal(g3)
    c: Horizontal(g5)
    c: Coincident(g2,g0)
    c: Coincident(g3,g-6)
    c: Coincident(g6,g7)
    c: Coincident(g7,g8)
    c: Coincident(g8,g9)
    c: Coincident(g9,g6)
    c: Horizontal(g6)
    c: Horizontal(g8)
    c: Vertical(g7)
    c: Vertical(g9)
    c: Coincident(g6,g1)
    c: Coincident(g7,g-6)
FEATURE [PartDesign::Pocket] Pocket023
  BaseFeature = -> Pocket017
  Direction = (0,0,1)
  Length = 0.5
  Length2 = 5
  Placement = pos=(0,-84,2e-15) rot=(1,0,0;1.5708rad)
  Profile = -> Sketch050
  ReferenceAxis = -> Sketch050 [N_Axis]
  Refine = true
  Suppressed = false
  Type = 0
FEATURE [Sketcher::SketchObject] Sketch051
  ArcFitTolerance = 1e-06
  AttachmentSupport = -> [Pocket023]
  ExternalGeometry = -> [Pocket023]
  FullyConstrained = true
  MakeInternals = false
  MapMode = 5
  Placement = pos=(7.9014e-08,-84,20.8536) rot=(1,0,0;3.14159rad)
  sketch-geometry (4):
    g0: LineSegment [constr] StartX=41.9965 StartY=-42 StartZ=0 EndX=50.2465 EndY=-42 EndZ=0
    g1: LineSegment [constr] StartX=41.9965 StartY=-42 StartZ=0 EndX=33.7465 EndY=-42 EndZ=0
    g2: Circle CenterX=33.7465 CenterY=-42 CenterZ=0 NormalX=0 NormalY=0 NormalZ=1 AngleXU=0 Radius=1.5
    g3: Circle CenterX=50.2465 CenterY=-42 CenterZ=0 NormalX=0 NormalY=0 NormalZ=1 AngleXU=0 Radius=1.5
  constraints (10):
    c: Distance(g0) = 8.25
    c: Coincident(g0,g-3)
    c: Horizontal(g0)
    c: Distance(g1) = 8.25
    c: Coincident(g1,g0)
    c: Horizontal(g1)
    c: Diameter(g2) = 3
    c: Coincident(g2,g1)
    c: Diameter(g3) = 3
    c: Coincident(g3,g0)
FEATURE [PartDesign::Pocket] Pocket024
  BaseFeature = -> Pocket023
  Direction = (0,0,1)
  Length = 11
  Length2 = 5
  Placement = pos=(0,-84,2e-15) rot=(1,0,0;1.5708rad)
  Profile = -> Sketch051
  ReferenceAxis = -> Sketch051 [N_Axis]
  Refine = true
  Suppressed = false
  Type = 0
FEATURE [Sketcher::SketchObject] Sketch052
  ArcFitTolerance = 1e-06
  AttachmentSupport = -> [Pocket024]
  ExternalGeometry = -> [Pocket024]
  FullyConstrained = true
  MakeInternals = false
  MapMode = 5
  Placement = pos=(6.55296e-08,-84,23.3536) rot=(0,0,1;3.14159rad)
  sketch-geometry (2):
    g0: Circle CenterX=-41.9965 CenterY=-42 CenterZ=0 NormalX=0 NormalY=0 NormalZ=1 AngleXU=0 Radius=1.55
    g1: Circle CenterX=-41.9965 CenterY=-42 CenterZ=0 NormalX=0 NormalY=0 NormalZ=1 AngleXU=0 Radius=3
  constraints (4):
    c: Diameter(g0) = 3.1
    c: Coincident(g0,g-4)
    c: Diameter(g1) = 6
    c: Coincident(g1,g0)
FEATURE [PartDesign::Pad] Pad023
  BaseFeature = -> Pocket024
  Direction = (0,0,1)
  Length = 4
  Length2 = 10
  Placement = pos=(0,-84,2e-15) rot=(1,0,0;1.5708rad)
  Profile = -> Sketch052
  ReferenceAxis = -> Sketch052 [N_Axis]
  Refine = true
  Suppressed = false
  Type = 0
FEATURE [Sketcher::SketchObject] Sketch053
  ArcFitTolerance = 1e-06
  AttachmentSupport = -> [Pad023]
  ExternalGeometry = -> [Pad023]
  FullyConstrained = true
  MakeInternals = false
  MapMode = 5
  Placement = pos=(7.67535e-08,-84,27.3536) rot=(0,0,1;3.14159rad)
  sketch-geometry (2):
    g0: Circle CenterX=-50.2465 CenterY=-42 CenterZ=0 NormalX=0 NormalY=0 NormalZ=1 AngleXU=0 Radius=3
    g1: Circle CenterX=-33.7465 CenterY=-42 CenterZ=0 NormalX=0 NormalY=0 NormalZ=1 AngleXU=0 Radius=3
  constraints (4):
    c: Diameter(g0) = 6
    c: Coincident(g0,g-4)
    c: Diameter(g1) = 6
    c: Coincident(g1,g-3)
FEATURE [PartDesign::Pocket] Pocket025
  BaseFeature = -> Pad023
  Direction = (0,0,-1)
  Length = 3.5
  Length2 = 5
  Placement = pos=(0,-84,2e-15) rot=(1,0,0;1.5708rad)
  Profile = -> Sketch053
  ReferenceAxis = -> Sketch053 [N_Axis]
  Refine = true
  Suppressed = false
  Type = 0
FEATURE [PartDesign::Body] Body002  label="TopPlate"
  AllowCompound = false
  Group = -> [ShapeBinder001,DatumPlane004,CopyFillet001,Sketch008,Pad006,Sketch009,Pocket001,Sketch010,Pocket002,Sketch011,Pocket003,Sketch012,Pocket004,Sketch013,Pocket005,Sketch030,Pad016,Sketch031,Pocket011,Sketch037,Pocket015,Sketch039,Pocket017,Sketch050,Pocket023,Sketch051,Pocket024,Sketch052,Pad023,Sketch053,Pocket025]
  Origin = -> Origin002
  Tip = -> Pocket025
FEATURE [Sketcher::SketchObject] Sketch054
  ArcFitTolerance = 1e-06
  AttachmentSupport = -> [Pocket022]
  ExternalGeometry = -> [Pocket022]
  FullyConstrained = true
  MakeInternals = false
  MapMode = 5
  Placement = pos=(3.93837e-08,5.8e-15,20.8536) rot=(0,0,1;0rad)
  sketch-geometry (8):
    g0: GeomPoint X=41.9965 Y=-37.25 Z=0
    g1: GeomPoint X=41.9965 Y=-46.75 Z=0
    g2: LineSegment [constr] StartX=41.9965 StartY=-37.25 StartZ=0 EndX=41.9965 EndY=-46.75 EndZ=0
    g3: GeomPoint [constr] X=41.9965 Y=-42 Z=0
    g4: LineSegment StartX=41.9965 StartY=-41 StartZ=0 EndX=41.1304 EndY=-42.5 EndZ=0
    g5: LineSegment StartX=41.1304 StartY=-42.5 StartZ=0 EndX=42.8625 EndY=-42.5 EndZ=0
    g6: LineSegment StartX=42.8625 StartY=-42.5 StartZ=0 EndX=41.9965 EndY=-41 EndZ=0
    g7: Circle [constr] CenterX=41.9965 CenterY=-42 CenterZ=0 NormalX=0 NormalY=0 NormalZ=1 AngleXU=0 Radius=1
  constraints (16):
    c: Symmetric(g-3,g-3,g0)
    c: Symmetric(g-4,g-4,g1)
    c: Coincident(g2,g0)
    c: Coincident(g2,g1)
    c: Symmetric(g2,g2,g3)
    c: Coincident(g4,g5)
    c: Coincident(g5,g6)
    c: Coincident(g6,g4)
    c: Equal(g4,g5)
    c: Equal(g4,g6)
    c: PointOnObject(g4,g7)
    c: PointOnObject(g5,g7)
    c: PointOnObject(g6,g7)
    c: Radius(g7) = 1
    c: Coincident(g7,g3)
    c: PointOnObject(g6,g2)
FEATURE [PartDesign::Pocket] Pocket026
  BaseFeature = -> Pocket022
  Direction = (0,0,-1)
  Length = 0.5
  Length2 = 5
  Profile = -> Sketch054
  ReferenceAxis = -> Sketch054 [N_Axis]
  Refine = true
  Suppressed = false
  Type = 0
FEATURE [PartDesign::Body] Body004  label="PlateThreadBlockModelled"
  AllowCompound = false
  Group = -> [Clone,Sketch018,Hole002,Sketch040,Pad019,Chamfer015,Chamfer016,Sketch041,Pocket018,Sketch043,Pocket019,Sketch044,Pad020,Sketch045,Pad021,Sketch046,Pocket020,Sketch047,Pocket021,Sketch048,Pad022,Sketch049,Pocket022,Sketch054,Pocket026]
  Origin = -> Origin004
  Placement = pos=(0,-23,0) rot=(0,0,1;0rad)
  Tip = -> Pocket026
FEATURE [Sketcher::SketchObject] Sketch055
  ArcFitTolerance = 1e-06
  AttachmentSupport = -> [Pocket014]
  ExternalGeometry = -> [Pocket014]
  FullyConstrained = true
  MakeInternals = false
  MapMode = 5
  Placement = pos=(42,-84,14) rot=(0.57735,0.57735,0.57735;4.18879rad)
  sketch-geometry (2):
    g0: Circle CenterX=0 CenterY=-0.03 CenterZ=0 NormalX=0 NormalY=0 NormalZ=1 AngleXU=0 Radius=3.03
    g1: Circle CenterX=0 CenterY=-0.03 CenterZ=0 NormalX=0 NormalY=0 NormalZ=1 AngleXU=0 Radius=3.75
  constraints (5):
    c: PointOnObject(g0,g-2)
    c: Tangent(g0,g-3)
    c: Diameter(g0) = 6.06
    c: Diameter(g1) = 7.5
    c: Coincident(g1,g0)
FEATURE [PartDesign::Pad] Pad024
  BaseFeature = -> Pocket014
  Direction = (0,1,0)
  Length = 21
  Length2 = 10
  Placement = pos=(42,-84,14) rot=(0.57735,-0.57735,0.57735;2.0944rad)
  Profile = -> Sketch055
  ReferenceAxis = -> Sketch055 [N_Axis]
  Refine = true
  Reversed = true
  Suppressed = false
  Type = 0
FEATURE [Sketcher::SketchObject] Sketch056
  ArcFitTolerance = 1e-06
  AttachmentSupport = -> [Pad024]
  ExternalGeometry = -> [Pad024]
  FullyConstrained = true
  MakeInternals = false
  MapMode = 5
  Placement = pos=(42,-84,14) rot=(0.57735,0.57735,0.57735;4.18879rad)
  sketch-geometry (2):
    g0: Circle CenterX=0 CenterY=0 CenterZ=0 NormalX=0 NormalY=0 NormalZ=1 AngleXU=0 Radius=2.9
    g1: Circle CenterX=0 CenterY=-0.03 CenterZ=0 NormalX=0 NormalY=0 NormalZ=1 AngleXU=0 Radius=3.75
  constraints (4):
    c: Coincident(g0,g-1)
    c: Diameter(g0) = 5.8
    c: Coincident(g1,g-3)
    c: Equal(g1,g-3)
FEATURE [PartDesign::Pocket] Pocket027
  BaseFeature = -> Pad024
  Direction = (0,-1,0)
  Length = 8
  Length2 = 5
  Placement = pos=(42,-84,14) rot=(0.57735,-0.57735,0.57735;2.0944rad)
  Profile = -> Sketch056
  ReferenceAxis = -> Sketch056 [N_Axis]
  Refine = true
  Suppressed = false
  Type = 0
FEATURE [PartDesign::Body] Body005  label="Adjustor"
  AllowCompound = false
  Group = -> [ShapeBinder003,DatumPlane006,Sketch019,Pad009,Sketch020,Pad010,Sketch021,Pad011,Sketch022,Pocket007,Fillet004,DatumPoint,VThreadProfile,Helix,AdditivePipe,ShapeBinder004,DatumPlane007,Sketch023,Pad012,Sketch035,Pocket013,Sketch036,Pocket014,Sketch055,Pad024,Sketch056,Pocket027]
  Origin = -> Origin005
  Tip = -> Pocket027
FEATURE [Sketcher::SketchObject] Sketch057
  ArcFitTolerance = 1e-06
  AttachmentSupport = -> [Pocket010]
  ExternalGeometry = -> [Pocket010]
  FullyConstrained = true
  MakeInternals = false
  MapMode = 5
  Placement = pos=(0,0,-5e-16) rot=(1,0,0;3.14159rad)
  sketch-geometry (4):
    g0: Circle CenterX=5 CenterY=79 CenterZ=0 NormalX=0 NormalY=0 NormalZ=1 AngleXU=0 Radius=1.5
    g1: Circle CenterX=79 CenterY=79 CenterZ=0 NormalX=0 NormalY=0 NormalZ=1 AngleXU=0 Radius=1.5
    g2: Circle CenterX=79 CenterY=5 CenterZ=0 NormalX=0 NormalY=0 NormalZ=1 AngleXU=0 Radius=1.5
    g3: Circle CenterX=5 CenterY=5 CenterZ=0 NormalX=0 NormalY=0 NormalZ=1 AngleXU=0 Radius=1.5
  constraints (8):
    c: Coincident(g0,g-3)
    c: Equal(g0,g-3)
    c: Coincident(g1,g-4)
    c: Equal(g1,g-4)
    c: Coincident(g2,g-5)
    c: Equal(g2,g-5)
    c: Coincident(g3,g-6)
    c: Equal(g3,g-6)
FEATURE [PartDesign::Pocket] Pocket028
  BaseFeature = -> Pocket010
  Direction = (0,0,1)
  Length = 10
  Length2 = 5
  Profile = -> Sketch057
  ReferenceAxis = -> Sketch057 [N_Axis]
  Refine = true
  Suppressed = false
  Type = 0
FEATURE [Sketcher::SketchObject] Sketch058
  ArcFitTolerance = 1e-06
  AttachmentSupport = -> [Pocket028]
  ExternalGeometry = -> [Pocket028]
  FullyConstrained = true
  MakeInternals = false
  MapMode = 5
  Placement = pos=(0,1.1e-15,5) rot=(0,0,1;0rad)
  sketch-geometry (4):
    g0: Circle CenterX=5 CenterY=-5 CenterZ=0 NormalX=0 NormalY=0 NormalZ=1 AngleXU=0 Radius=3
    g1: Circle CenterX=5 CenterY=-79 CenterZ=0 NormalX=0 NormalY=0 NormalZ=1 AngleXU=0 Radius=3
    g2: Circle CenterX=79 CenterY=-79 CenterZ=0 NormalX=0 NormalY=0 NormalZ=1 AngleXU=0 Radius=3
    g3: Circle CenterX=79 CenterY=-5 CenterZ=0 NormalX=0 NormalY=0 NormalZ=1 AngleXU=0 Radius=3
  constraints (8):
    c: Diameter(g0) = 6
    c: Coincident(g0,g-3)
    c: Diameter(g1) = 6
    c: Coincident(g1,g-4)
    c: Diameter(g2) = 6
    c: Coincident(g2,g-5)
    c: Diameter(g3) = 6
    c: Coincident(g3,g-6)
FEATURE [PartDesign::Pocket] Pocket029
  BaseFeature = -> Pocket028
  Direction = (0,0,-1)
  Length = 3.25
  Length2 = 5
  Profile = -> Sketch058
  ReferenceAxis = -> Sketch058 [N_Axis]
  Refine = true
  Suppressed = false
  Type = 0
FEATURE [Sketcher::SketchObject] Sketch059
  ArcFitTolerance = 1e-06
  AttachmentSupport = -> [Pocket029]
  ExternalGeometry = -> [Pocket029]
  FullyConstrained = true
  MakeInternals = false
  MapMode = 5
  Placement = pos=(0,0,-5e-16) rot=(1,0,0;3.14159rad)
  sketch-geometry (8):
    g0: LineSegment StartX=0 StartY=84 StartZ=0 EndX=0 EndY=0 EndZ=0
    g1: LineSegment StartX=0 StartY=0 StartZ=0 EndX=84 EndY=0 EndZ=0
    g2: LineSegment StartX=84 StartY=0 StartZ=0 EndX=84 EndY=84 EndZ=0
    g3: LineSegment StartX=84 StartY=84 StartZ=0 EndX=0 EndY=84 EndZ=0
    g4: Circle CenterX=5 CenterY=79 CenterZ=0 NormalX=0 NormalY=0 NormalZ=1 AngleXU=0 Radius=1.5
    g5: Circle CenterX=79 CenterY=79 CenterZ=0 NormalX=0 NormalY=0 NormalZ=1 AngleXU=0 Radius=1.5
    g6: Circle CenterX=79 CenterY=5 CenterZ=0 NormalX=0 NormalY=0 NormalZ=1 AngleXU=0 Radius=1.5
    g7: Circle CenterX=5 CenterY=5 CenterZ=0 NormalX=0 NormalY=0 NormalZ=1 AngleXU=0 Radius=1.5
  constraints (18):
    c: Coincident(g0,g1)
    c: Coincident(g1,g2)
    c: Coincident(g2,g3)
    c: Coincident(g3,g0)
    c: Vertical(g0)
    c: Vertical(g2)
    c: Horizontal(g1)
    c: Horizontal(g3)
    c: Coincident(g0,g-3)
    c: Coincident(g1,g-4)
    c: Coincident(g4,g-8)
    c: Equal(g4,g-8)
    c: Coincident(g5,g-5)
    c: Equal(g5,g-5)
    c: Coincident(g6,g-6)
    c: Equal(g6,g-6)
    c: Coincident(g7,g-7)
    c: Equal(g7,g-7)
FEATURE [PartDesign::Pad] Pad025
  BaseFeature = -> Pocket029
  Direction = (0,0,-1)
  Length = 1.25
  Length2 = 10
  Profile = -> Sketch059
  ReferenceAxis = -> Sketch059 [N_Axis]
  Refine = true
  Suppressed = false
  Type = 0
FEATURE [PartDesign::Body] Body007  label="BaseNoGrid"
  AllowCompound = false
  Group = -> [Clone001,Sketch028,Pocket009,Sketch029,Pocket010,Sketch057,Pocket028,Sketch058,Pocket029,Sketch059,Pad025]
  Origin = -> Origin007
  Placement = pos=(-93,0,0) rot=(0,0,1;0rad)
  Tip = -> Pad025
FEATURE [PartDesign::FeaturePython] BinBase  # WARN: FeaturePython — macro-defined, semantics opaque (R4)
  BaseProfileBottomChamfer = 0.8
  BaseProfileHeight = 4.75
  BaseProfileTopChamfer = 2.15
  BaseProfileVerticalSection = 1.8
  BinBottomRadius = 0.8
  BinOuterRadius = 3.75
  BinUnit = 41.5
  BinVerticalRadius = 1.6
  CustomHeight = 42
  GridSize = 42
  HeightUnitValue = 7
  HeightUnits = 1
  MagnetHoleDepth = 2.4
  MagnetHoleDiameter = 6.5
  MagnetHoleDistanceFromEdge = 8
  MagnetHoles = true
  NonStandardHeight = false
  ScrewHoleDepth = 6
  ScrewHoleDiameter = 3
  ScrewHoles = true
  SequentialBridgingLayerHeight = 0.2
  StackingLip = false
  StackingLipBottomChamfer = 0.7
  StackingLipTopChamfer = 1.5
  StackingLipTopLedge = 0.4
  StackingLipVerticalSection = 1.8
  Suppressed = false
  Tolerance = 0.25
  TotalHeight = 7
  WallThickness = 1
  version = 0.6.0
  xGridUnits = 2
  xTotalWidth = 83.5
  yGridUnits = 2
  yTotalWidth = 83.5
FEATURE [Sketcher::SketchObject] Sketch060
  ArcFitTolerance = 1e-06
  AttachmentSupport = -> [BinBase]
  ExternalGeometry = -> [BinBase]
  FullyConstrained = true
  MakeInternals = false
  MapMode = 5
  expr: Constraints[19] = <<GridFinityBaseParams>>.MountingHoleDiameter
  sketch-geometry (15):
    g0: GeomPoint X=21 Y=62.75 Z=0
    g1: GeomPoint X=21 Y=-20.75 Z=0
    g2: GeomPoint X=62.75 Y=21 Z=0
    g3: GeomPoint X=-20.75 Y=21 Z=0
    g4: LineSegment [constr] StartX=-20.75 StartY=21 StartZ=0 EndX=62.75 EndY=21 EndZ=0
    g5: GeomPoint [constr] X=21 Y=21 Z=0
    g6: LineSegment [constr] StartX=-16 StartY=-16 StartZ=0 EndX=58 EndY=-16 EndZ=0
    g7: LineSegment [constr] StartX=58 StartY=-16 StartZ=0 EndX=58 EndY=58 EndZ=0
    g8: LineSegment [constr] StartX=58 StartY=58 StartZ=0 EndX=-16 EndY=58 EndZ=0
    g9: LineSegment [constr] StartX=-16 StartY=58 StartZ=0 EndX=-16 EndY=-16 EndZ=0
    g10: GeomPoint [constr] X=21 Y=21 Z=0
    g11: Circle CenterX=-16 CenterY=58 CenterZ=0 NormalX=0 NormalY=0 NormalZ=1 AngleXU=0 Radius=1.3
    g12: Circle CenterX=58 CenterY=58 CenterZ=0 NormalX=0 NormalY=0 NormalZ=1 AngleXU=0 Radius=1.3
    g13: Circle CenterX=58 CenterY=-16 CenterZ=0 NormalX=0 NormalY=0 NormalZ=1 AngleXU=0 Radius=1.3
    g14: Circle CenterX=-16 CenterY=-16 CenterZ=0 NormalX=0 NormalY=0 NormalZ=1 AngleXU=0 Radius=1.3
  constraints (27):
    c: Symmetric(g-3,g-3,g0)
    c: Symmetric(g-5,g-5,g1)
    c: Symmetric(g-6,g-6,g2)
    c: Symmetric(g-4,g-4,g3)
    c: Coincident(g4,g3)
    c: Coincident(g4,g2)
    c: Symmetric(g4,g4,g5)
    c: Coincident(g6,g7)
    c: Coincident(g7,g8)
    c: Coincident(g8,g9)
    c: Coincident(g9,g6)
    c: Horizontal(g6)
    c: Horizontal(g8)
    c: Vertical(g7)
    c: Vertical(g9)
    c: Symmetric(g8,g6,g10)
    c: Distance(g7,g9) = 74
    c: Distance(g6,g8) = 74
    c: Coincident(g10,g5)
    c: Diameter(g11) = 2.6
    c: Coincident(g11,g8)
    c: Coincident(g12,g7)
    c: Coincident(g13,g6)
    c: Coincident(g14,g6)
    c: Equal(g11,g12)
    c: Equal(g12,g13)
    c: Equal(g13,g14)
FEATURE [App::VarSet] VarSet  label="GridFinityBaseParams"
  HolePocketDepth = 5
  MountingHoleDiameter = 2.6
FEATURE [PartDesign::Pocket] Pocket030
  BaseFeature = -> BinBase
  Direction = (0,0,-1)
  Length = 5
  Length2 = 5
  Profile = -> Sketch060
  ReferenceAxis = -> Sketch060 [N_Axis]
  Refine = true
  Suppressed = false
  Type = 0
  expr: Length = <<GridFinityBaseParams>>.HolePocketDepth
FEATURE [PartDesign::Body] Body009  label="GridFinity Base"
  AllowCompound = false
  Group = -> [BinBase,Sketch060,VarSet,Pocket030]
  Origin = -> Origin009
  Placement = pos=(-71,35,0) rot=(0,0,1;0rad)
  Tip = -> Pocket030
